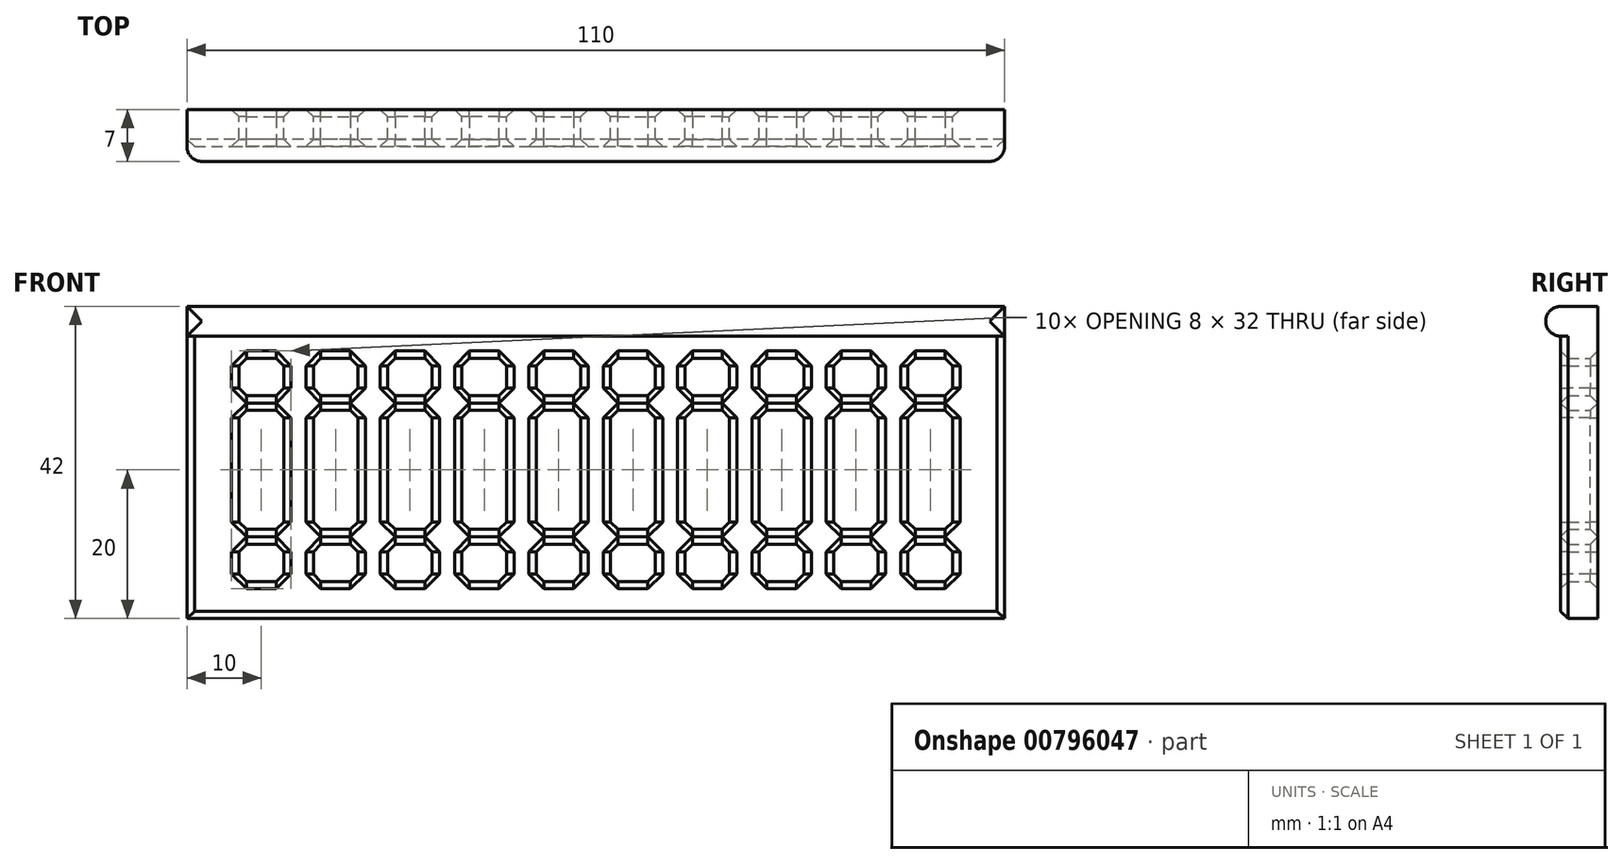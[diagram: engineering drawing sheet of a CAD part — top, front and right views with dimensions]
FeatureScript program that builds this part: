
annotation { "Feature Type Name" : "Feature", "Feature Type Description" : "" }
export const myFeature = defineFeature(function(context is Context, id is Id, definition is map)
    precondition{}
    {
        {
            var Q0;
            Q0=qCreatedBy(makeId("Front.planeOp"),FACE);
            var sketch = newSketch(context, id + "F0", { "sketchPlane" : qUnion([Q0])});
            skLineSegment(sketch, "E0.bottom", {"start": v(0, 0) * mm, "end": v(110, 0) * mm});
            skLineSegment(sketch, "E0.top", {"start": v(0, 40) * mm, "end": v(110, 40) * mm});
            skLineSegment(sketch, "E0.left", {"start": v(0, 0) * mm, "end": v(0, 40) * mm});
            skLineSegment(sketch, "E0.right", {"start": v(110, 0) * mm, "end": v(110, 40) * mm});
            skLineSegment(sketch, "E1.left", {"start": v(7, 35) * mm, "end": v(7, 5) * mm});
            skLineSegment(sketch, "E1.right", {"start": v(103, 35) * mm, "end": v(103, 5) * mm});
            skLineSegment(sketch, "E2.left", {"start": v(13, 35) * mm, "end": v(13, 5) * mm});
            skLineSegment(sketch, "E2.right", {"start": v(17, 35) * mm, "end": v(17, 5) * mm});
            skLineSegment(sketch, "E3.bottom", {"start": v(17, 5) * mm, "end": v(23, 5) * mm});
            skLineSegment(sketch, "E3.left", {"start": v(17, 5) * mm, "end": v(17, 35) * mm});
            skLineSegment(sketch, "E3.right", {"start": v(23, 5) * mm, "end": v(23, 35) * mm});
            skLineSegment(sketch, "E4.right", {"start": v(27, 5) * mm, "end": v(27, 35) * mm});
            skLineSegment(sketch, "E5.right", {"start": v(33, 35) * mm, "end": v(33, 5) * mm});
            skLineSegment(sketch, "E6.top", {"start": v(37, 5) * mm, "end": v(43, 5) * mm});
            skLineSegment(sketch, "E6.left", {"start": v(37, 35) * mm, "end": v(37, 5) * mm});
            skLineSegment(sketch, "E6.right", {"start": v(43, 35) * mm, "end": v(43, 5) * mm});
            skLineSegment(sketch, "E7.right", {"start": v(97, 35) * mm, "end": v(97, 5) * mm});
            skLineSegment(sketch, "E8.left", {"start": v(47, 35) * mm, "end": v(47, 5) * mm});
            skLineSegment(sketch, "E9.right", {"start": v(57, 35) * mm, "end": v(57, 5) * mm});
            skLineSegment(sketch, "E10.bottom", {"start": v(77, 35) * mm, "end": v(83, 35) * mm});
            skLineSegment(sketch, "E10.top", {"start": v(77, 5) * mm, "end": v(83, 5) * mm});
            skLineSegment(sketch, "E10.left", {"start": v(77, 35) * mm, "end": v(77, 5) * mm});
            skLineSegment(sketch, "E10.right", {"start": v(83, 35) * mm, "end": v(83, 5) * mm});
            skLineSegment(sketch, "E11.bottom", {"start": v(87, 35) * mm, "end": v(93, 35) * mm});
            skLineSegment(sketch, "E11.top", {"start": v(87, 5) * mm, "end": v(93, 5) * mm});
            skLineSegment(sketch, "E11.left", {"start": v(87, 35) * mm, "end": v(87, 5) * mm});
            skLineSegment(sketch, "E11.right", {"start": v(93, 35) * mm, "end": v(93, 5) * mm});
            skLineSegment(sketch, "E12.bottom", {"start": v(2, 37) * mm, "end": v(108, 37) * mm});
            skLineSegment(sketch, "E12.top", {"start": v(2, 3) * mm, "end": v(108, 3) * mm});
            skLineSegment(sketch, "E12.left", {"start": v(2, 37) * mm, "end": v(2, 3) * mm});
            skLineSegment(sketch, "E12.right", {"start": v(108, 37) * mm, "end": v(108, 3) * mm});
            skLineSegment(sketch, "E13.bottom", {"start": v(7, 30) * mm, "end": v(103, 30) * mm});
            skLineSegment(sketch, "E13.top", {"start": v(7, 10) * mm, "end": v(103, 10) * mm});
            skLineSegment(sketch, "E13.left", {"start": v(7, 30) * mm, "end": v(7, 10) * mm});
            skLineSegment(sketch, "E13.right", {"start": v(103, 30) * mm, "end": v(103, 10) * mm});
            skLineSegment(sketch, "E14.bottom", {"start": v(7, 28) * mm, "end": v(103, 28) * mm});
            skLineSegment(sketch, "E14.top", {"start": v(7, 12) * mm, "end": v(103, 12) * mm});
            skLineSegment(sketch, "E14.left", {"start": v(7, 28) * mm, "end": v(7, 12) * mm});
            skLineSegment(sketch, "E14.right", {"start": v(103, 28) * mm, "end": v(103, 12) * mm});
            skLineSegment(sketch, "E15", {"start": v(67, 35) * mm, "end": v(67, 5) * mm});
            skLineSegment(sketch, "E16", {"start": v(53, 35) * mm, "end": v(53, 5) * mm});
            skLineSegment(sketch, "E17", {"start": v(47, 35) * mm, "end": v(53, 35) * mm});
            skLineSegment(sketch, "E18", {"start": v(7, 35) * mm, "end": v(13, 35) * mm});
            skLineSegment(sketch, "E19", {"start": v(17, 35) * mm, "end": v(23, 35) * mm});
            skLineSegment(sketch, "E20", {"start": v(27, 35) * mm, "end": v(33, 35) * mm});
            skLineSegment(sketch, "E21", {"start": v(37, 35) * mm, "end": v(43, 35) * mm});
            skLineSegment(sketch, "E22", {"start": v(97, 35) * mm, "end": v(103, 35) * mm});
            skLineSegment(sketch, "E23", {"start": v(63, 35) * mm, "end": v(63, 5) * mm});
            skLineSegment(sketch, "E24", {"start": v(73, 35) * mm, "end": v(73, 5) * mm});
            skLineSegment(sketch, "E25", {"start": v(57, 35) * mm, "end": v(63, 35) * mm});
            skLineSegment(sketch, "E26", {"start": v(67, 35) * mm, "end": v(73, 35) * mm});
            skLineSegment(sketch, "E27", {"start": v(47, 5) * mm, "end": v(53, 5) * mm});
            skLineSegment(sketch, "E28", {"start": v(27, 5) * mm, "end": v(33, 5) * mm});
            skLineSegment(sketch, "E29", {"start": v(7, 5) * mm, "end": v(13, 5) * mm});
            skLineSegment(sketch, "E30", {"start": v(57, 5) * mm, "end": v(63, 5) * mm});
            skLineSegment(sketch, "E31", {"start": v(67, 5) * mm, "end": v(73, 5) * mm});
            skLineSegment(sketch, "E32", {"start": v(97, 5) * mm, "end": v(103, 5) * mm});
            skSolve(sketch);
        }
        {
            var Q0;
            {var subQ0=sQuery(id+"F0.wireOp",EDGE,"E2.top");Q0=makeQuery(id+"F0.imprint","IMPRINT",FACE,{"disambiguationData":[TD([[makeQuery(id+"F0.imprint","IMPRINT",EDGE,{"derivedFrom":subQ0}),1.0]])]});}
            var Q1;
            {var subQ0=sQuery(id+"F0.wireOp",EDGE,"E4.bottom");Q1=makeQuery(id+"F0.imprint","IMPRINT",FACE,{"disambiguationData":[TD([[makeQuery(id+"F0.imprint","IMPRINT",EDGE,{"derivedFrom":subQ0}),1.0]])]});}
            var Q2;
            {var subQ76=sQuery(id+"F0.wireOp",EDGE,"E3.bottom");Q2=makeQuery(id+"F0.imprint","IMPRINT",FACE,{"disambiguationData":[TD([[makeQuery(id+"F0.imprint","IMPRINT",EDGE,{"derivedFrom":subQ76}),-1.0]])]});}
            var Q3;
            {var subQ76=sQuery(id+"F0.wireOp",EDGE,"E3.bottom");Q3=makeQuery(id+"F0.imprint","IMPRINT",FACE,{"disambiguationData":[TD([[makeQuery(id+"F0.imprint","IMPRINT",EDGE,{"derivedFrom":subQ76}),-1.0]])]});}
            var Q4;
            {var subQ76=sQuery(id+"F0.wireOp",EDGE,"E3.bottom");Q4=makeQuery(id+"F0.imprint","IMPRINT",FACE,{"disambiguationData":[TD([[makeQuery(id+"F0.imprint","IMPRINT",EDGE,{"derivedFrom":subQ76}),-1.0]])]});}
            var Q5;
            {var subQ76=sQuery(id+"F0.wireOp",EDGE,"E3.bottom");Q5=makeQuery(id+"F0.imprint","IMPRINT",FACE,{"disambiguationData":[TD([[makeQuery(id+"F0.imprint","IMPRINT",EDGE,{"derivedFrom":subQ76}),-1.0]])]});}
            var Q6;
            {var subQ0=sQuery(id+"F0.wireOp",EDGE,"E15");var subQ1=sQuery(id+"F0.wireOp",EDGE,"E9.top");var subQ2=makeQuery(id+"F0.imprint","INTERSECT",VERTEX,{"derivedFrom":[subQ1,subQ0]});Q6=makeQuery(id+"F0.imprint","IMPRINT",FACE,{"disambiguationData":[TD([[makeQuery(id+"F0.imprint","IMPRINT",EDGE,{"disambiguationData":[TD([[subQ2,-1.0]])],"derivedFrom":subQ1}),-1.0]])]});}
            var Q7;
            Q7=makeQuery(id+"F0.imprint","IMPRINT",FACE,{"disambiguationData":[TD([[makeQuery(id+"F0.imprint","IMPRINT",EDGE,{"derivedFrom":sQuery(id+"F0.wireOp",EDGE,"E0.bottom")}),1.0]])]});
            var Q8;
            {var subQ0=sQuery(id+"F0.wireOp",EDGE,"E14.bottom");var subQ1=sQuery(id+"F0.wireOp",EDGE,"E2.left");var subQ2=makeQuery(id+"F0.imprint","INTERSECT",VERTEX,{"derivedFrom":[subQ1,subQ0]});Q8=makeQuery(id+"F0.imprint","IMPRINT",FACE,{"disambiguationData":[TD([[makeQuery(id+"F0.imprint","IMPRINT",EDGE,{"disambiguationData":[TD([[subQ2,1.0]])],"derivedFrom":subQ1}),1.0]])]});}
            var Q9;
            {var subQ0=sQuery(id+"F0.wireOp",EDGE,"E14.bottom");var subQ1=sQuery(id+"F0.wireOp",EDGE,"E1.left");var subQ2=makeQuery(id+"F0.imprint","INTERSECT",VERTEX,{"derivedFrom":[subQ1,subQ0]});Q9=makeQuery(id+"F0.imprint","IMPRINT",FACE,{"disambiguationData":[TD([[makeQuery(id+"F0.imprint","IMPRINT",EDGE,{"disambiguationData":[TD([[subQ2,1.0]])],"derivedFrom":subQ1}),1.0]])]});}
            var Q10;
            {var subQ0=sQuery(id+"F0.wireOp",EDGE,"E13.top");var subQ1=sQuery(id+"F0.wireOp",EDGE,"E2.left");var subQ2=makeQuery(id+"F0.imprint","INTERSECT",VERTEX,{"derivedFrom":[subQ1,subQ0]});Q10=makeQuery(id+"F0.imprint","IMPRINT",FACE,{"disambiguationData":[TD([[makeQuery(id+"F0.imprint","IMPRINT",EDGE,{"disambiguationData":[TD([[subQ2,1.0]])],"derivedFrom":subQ1}),1.0]])]});}
            var Q11;
            {var subQ0=sQuery(id+"F0.wireOp",EDGE,"E14.top");var subQ1=sQuery(id+"F0.wireOp",EDGE,"E1.left");var subQ2=makeQuery(id+"F0.imprint","INTERSECT",VERTEX,{"derivedFrom":[subQ1,subQ0]});Q11=makeQuery(id+"F0.imprint","IMPRINT",FACE,{"disambiguationData":[TD([[makeQuery(id+"F0.imprint","IMPRINT",EDGE,{"disambiguationData":[TD([[subQ2,-1.0]])],"derivedFrom":subQ1}),1.0]])]});}
            var Q12;
            {var subQ0=sQuery(id+"F0.wireOp",EDGE,"E14.top");var subQ1=sQuery(id+"F0.wireOp",EDGE,"E2.right");var subQ2=makeQuery(id+"F0.imprint","INTERSECT",VERTEX,{"derivedFrom":[subQ1,subQ0]});Q12=makeQuery(id+"F0.imprint","IMPRINT",FACE,{"disambiguationData":[TD([[makeQuery(id+"F0.imprint","IMPRINT",EDGE,{"disambiguationData":[TD([[subQ2,-1.0]])],"derivedFrom":subQ1}),1.0]])]});}
            var Q13;
            {var subQ0=sQuery(id+"F0.wireOp",EDGE,"E14.top");var subQ1=sQuery(id+"F0.wireOp",EDGE,"E3.right");var subQ2=makeQuery(id+"F0.imprint","INTERSECT",VERTEX,{"derivedFrom":[subQ1,subQ0]});Q13=makeQuery(id+"F0.imprint","IMPRINT",FACE,{"disambiguationData":[TD([[makeQuery(id+"F0.imprint","IMPRINT",EDGE,{"disambiguationData":[TD([[subQ2,1.0]])],"derivedFrom":subQ1}),-1.0]])]});}
            var Q14;
            {var subQ0=sQuery(id+"F0.wireOp",EDGE,"E14.top");var subQ1=sQuery(id+"F0.wireOp",EDGE,"E3.right");var subQ2=makeQuery(id+"F0.imprint","INTERSECT",VERTEX,{"derivedFrom":[subQ1,subQ0]});Q14=makeQuery(id+"F0.imprint","IMPRINT",FACE,{"disambiguationData":[TD([[makeQuery(id+"F0.imprint","IMPRINT",EDGE,{"disambiguationData":[TD([[subQ2,-1.0]])],"derivedFrom":subQ1}),-1.0]])]});}
            var Q15;
            {var subQ0=sQuery(id+"F0.wireOp",EDGE,"E13.bottom");var subQ1=sQuery(id+"F0.wireOp",EDGE,"E3.right");var subQ2=makeQuery(id+"F0.imprint","INTERSECT",VERTEX,{"derivedFrom":[subQ1,subQ0]});Q15=makeQuery(id+"F0.imprint","IMPRINT",FACE,{"disambiguationData":[TD([[makeQuery(id+"F0.imprint","IMPRINT",EDGE,{"disambiguationData":[TD([[subQ2,1.0]])],"derivedFrom":subQ1}),-1.0]])]});}
            var Q16;
            {var subQ0=sQuery(id+"F0.wireOp",EDGE,"E14.bottom");var subQ1=sQuery(id+"F0.wireOp",EDGE,"E2.right");var subQ2=makeQuery(id+"F0.imprint","INTERSECT",VERTEX,{"derivedFrom":[subQ1,subQ0]});Q16=makeQuery(id+"F0.imprint","IMPRINT",FACE,{"disambiguationData":[TD([[makeQuery(id+"F0.imprint","IMPRINT",EDGE,{"disambiguationData":[TD([[subQ2,1.0]])],"derivedFrom":subQ1}),1.0]])]});}
            var Q17;
            {var subQ0=sQuery(id+"F0.wireOp",EDGE,"E14.bottom");var subQ1=sQuery(id+"F0.wireOp",EDGE,"E2.left");var subQ2=makeQuery(id+"F0.imprint","INTERSECT",VERTEX,{"derivedFrom":[subQ1,subQ0]});Q17=makeQuery(id+"F0.imprint","IMPRINT",FACE,{"disambiguationData":[TD([[makeQuery(id+"F0.imprint","IMPRINT",EDGE,{"disambiguationData":[TD([[subQ2,-1.0]])],"derivedFrom":subQ1}),1.0]])]});}
            var Q18;
            {var subQ0=sQuery(id+"F0.wireOp",EDGE,"E14.top");var subQ1=sQuery(id+"F0.wireOp",EDGE,"E4.right");var subQ2=makeQuery(id+"F0.imprint","INTERSECT",VERTEX,{"derivedFrom":[subQ1,subQ0]});Q18=makeQuery(id+"F0.imprint","IMPRINT",FACE,{"disambiguationData":[TD([[makeQuery(id+"F0.imprint","IMPRINT",EDGE,{"disambiguationData":[TD([[subQ2,1.0]])],"derivedFrom":subQ1}),-1.0]])]});}
            var Q19;
            {var subQ0=sQuery(id+"F0.wireOp",EDGE,"E13.top");var subQ1=sQuery(id+"F0.wireOp",EDGE,"E5.right");var subQ2=makeQuery(id+"F0.imprint","INTERSECT",VERTEX,{"derivedFrom":[subQ1,subQ0]});Q19=makeQuery(id+"F0.imprint","IMPRINT",FACE,{"disambiguationData":[TD([[makeQuery(id+"F0.imprint","IMPRINT",EDGE,{"disambiguationData":[TD([[subQ2,1.0]])],"derivedFrom":subQ1}),1.0]])]});}
            var Q20;
            {var subQ0=sQuery(id+"F0.wireOp",EDGE,"E14.bottom");var subQ1=sQuery(id+"F0.wireOp",EDGE,"E5.right");var subQ2=makeQuery(id+"F0.imprint","INTERSECT",VERTEX,{"derivedFrom":[subQ1,subQ0]});Q20=makeQuery(id+"F0.imprint","IMPRINT",FACE,{"disambiguationData":[TD([[makeQuery(id+"F0.imprint","IMPRINT",EDGE,{"disambiguationData":[TD([[subQ2,-1.0]])],"derivedFrom":subQ1}),1.0]])]});}
            var Q21;
            {var subQ0=sQuery(id+"F0.wireOp",EDGE,"E14.bottom");var subQ1=sQuery(id+"F0.wireOp",EDGE,"E5.right");var subQ2=makeQuery(id+"F0.imprint","INTERSECT",VERTEX,{"derivedFrom":[subQ1,subQ0]});Q21=makeQuery(id+"F0.imprint","IMPRINT",FACE,{"disambiguationData":[TD([[makeQuery(id+"F0.imprint","IMPRINT",EDGE,{"disambiguationData":[TD([[subQ2,1.0]])],"derivedFrom":subQ1}),1.0]])]});}
            var Q22;
            {var subQ0=sQuery(id+"F0.wireOp",EDGE,"E13.bottom");var subQ1=sQuery(id+"F0.wireOp",EDGE,"E4.right");var subQ2=makeQuery(id+"F0.imprint","INTERSECT",VERTEX,{"derivedFrom":[subQ1,subQ0]});Q22=makeQuery(id+"F0.imprint","IMPRINT",FACE,{"disambiguationData":[TD([[makeQuery(id+"F0.imprint","IMPRINT",EDGE,{"disambiguationData":[TD([[subQ2,1.0]])],"derivedFrom":subQ1}),-1.0]])]});}
            var Q23;
            {var subQ0=sQuery(id+"F0.wireOp",EDGE,"E14.bottom");var subQ1=sQuery(id+"F0.wireOp",EDGE,"E6.left");var subQ2=makeQuery(id+"F0.imprint","INTERSECT",VERTEX,{"derivedFrom":[subQ1,subQ0]});Q23=makeQuery(id+"F0.imprint","IMPRINT",FACE,{"disambiguationData":[TD([[makeQuery(id+"F0.imprint","IMPRINT",EDGE,{"disambiguationData":[TD([[subQ2,1.0]])],"derivedFrom":subQ1}),1.0]])]});}
            var Q24;
            {var subQ0=sQuery(id+"F0.wireOp",EDGE,"E14.bottom");var subQ1=sQuery(id+"F0.wireOp",EDGE,"E6.right");var subQ2=makeQuery(id+"F0.imprint","INTERSECT",VERTEX,{"derivedFrom":[subQ1,subQ0]});Q24=makeQuery(id+"F0.imprint","IMPRINT",FACE,{"disambiguationData":[TD([[makeQuery(id+"F0.imprint","IMPRINT",EDGE,{"disambiguationData":[TD([[subQ2,1.0]])],"derivedFrom":subQ1}),1.0]])]});}
            var Q25;
            {var subQ0=sQuery(id+"F0.wireOp",EDGE,"E14.bottom");var subQ1=sQuery(id+"F0.wireOp",EDGE,"E6.right");var subQ2=makeQuery(id+"F0.imprint","INTERSECT",VERTEX,{"derivedFrom":[subQ1,subQ0]});Q25=makeQuery(id+"F0.imprint","IMPRINT",FACE,{"disambiguationData":[TD([[makeQuery(id+"F0.imprint","IMPRINT",EDGE,{"disambiguationData":[TD([[subQ2,-1.0]])],"derivedFrom":subQ1}),1.0]])]});}
            var Q26;
            {var subQ0=sQuery(id+"F0.wireOp",EDGE,"E14.top");var subQ1=sQuery(id+"F0.wireOp",EDGE,"E6.right");var subQ2=makeQuery(id+"F0.imprint","INTERSECT",VERTEX,{"derivedFrom":[subQ1,subQ0]});Q26=makeQuery(id+"F0.imprint","IMPRINT",FACE,{"disambiguationData":[TD([[makeQuery(id+"F0.imprint","IMPRINT",EDGE,{"disambiguationData":[TD([[subQ2,-1.0]])],"derivedFrom":subQ1}),1.0]])]});}
            var Q27;
            {var subQ0=sQuery(id+"F0.wireOp",EDGE,"E14.top");var subQ1=sQuery(id+"F0.wireOp",EDGE,"E6.left");var subQ2=makeQuery(id+"F0.imprint","INTERSECT",VERTEX,{"derivedFrom":[subQ1,subQ0]});Q27=makeQuery(id+"F0.imprint","IMPRINT",FACE,{"disambiguationData":[TD([[makeQuery(id+"F0.imprint","IMPRINT",EDGE,{"disambiguationData":[TD([[subQ2,-1.0]])],"derivedFrom":subQ1}),1.0]])]});}
            var Q28;
            {var subQ76=sQuery(id+"F0.wireOp",EDGE,"E3.bottom");Q28=makeQuery(id+"F0.imprint","IMPRINT",FACE,{"disambiguationData":[TD([[makeQuery(id+"F0.imprint","IMPRINT",EDGE,{"derivedFrom":subQ76}),-1.0]])]});}
            var Q29;
            {var subQ0=sQuery(id+"F0.wireOp",EDGE,"E13.top");var subQ1=sQuery(id+"F0.wireOp",EDGE,"E8.left");var subQ2=makeQuery(id+"F0.imprint","INTERSECT",VERTEX,{"derivedFrom":[subQ1,subQ0]});Q29=makeQuery(id+"F0.imprint","IMPRINT",FACE,{"disambiguationData":[TD([[makeQuery(id+"F0.imprint","IMPRINT",EDGE,{"disambiguationData":[TD([[subQ2,1.0]])],"derivedFrom":subQ1}),1.0]])]});}
            var Q30;
            {var subQ0=sQuery(id+"F0.wireOp",EDGE,"E14.bottom");var subQ1=sQuery(id+"F0.wireOp",EDGE,"E8.left");var subQ2=makeQuery(id+"F0.imprint","INTERSECT",VERTEX,{"derivedFrom":[subQ1,subQ0]});Q30=makeQuery(id+"F0.imprint","IMPRINT",FACE,{"disambiguationData":[TD([[makeQuery(id+"F0.imprint","IMPRINT",EDGE,{"disambiguationData":[TD([[subQ2,1.0]])],"derivedFrom":subQ1}),1.0]])]});}
            var Q31;
            {var subQ0=sQuery(id+"F0.wireOp",EDGE,"E14.bottom");var subQ1=sQuery(id+"F0.wireOp",EDGE,"E10.left");var subQ2=makeQuery(id+"F0.imprint","INTERSECT",VERTEX,{"derivedFrom":[subQ1,subQ0]});Q31=makeQuery(id+"F0.imprint","IMPRINT",FACE,{"disambiguationData":[TD([[makeQuery(id+"F0.imprint","IMPRINT",EDGE,{"disambiguationData":[TD([[subQ2,1.0]])],"derivedFrom":subQ1}),1.0]])]});}
            var Q32;
            {var subQ0=sQuery(id+"F0.wireOp",EDGE,"E14.bottom");var subQ1=sQuery(id+"F0.wireOp",EDGE,"E10.right");var subQ2=makeQuery(id+"F0.imprint","INTERSECT",VERTEX,{"derivedFrom":[subQ1,subQ0]});Q32=makeQuery(id+"F0.imprint","IMPRINT",FACE,{"disambiguationData":[TD([[makeQuery(id+"F0.imprint","IMPRINT",EDGE,{"disambiguationData":[TD([[subQ2,1.0]])],"derivedFrom":subQ1}),1.0]])]});}
            var Q33;
            {var subQ0=sQuery(id+"F0.wireOp",EDGE,"E14.bottom");var subQ1=sQuery(id+"F0.wireOp",EDGE,"E10.right");var subQ2=makeQuery(id+"F0.imprint","INTERSECT",VERTEX,{"derivedFrom":[subQ1,subQ0]});Q33=makeQuery(id+"F0.imprint","IMPRINT",FACE,{"disambiguationData":[TD([[makeQuery(id+"F0.imprint","IMPRINT",EDGE,{"disambiguationData":[TD([[subQ2,-1.0]])],"derivedFrom":subQ1}),1.0]])]});}
            var Q34;
            {var subQ0=sQuery(id+"F0.wireOp",EDGE,"E14.top");var subQ1=sQuery(id+"F0.wireOp",EDGE,"E10.right");var subQ2=makeQuery(id+"F0.imprint","INTERSECT",VERTEX,{"derivedFrom":[subQ1,subQ0]});Q34=makeQuery(id+"F0.imprint","IMPRINT",FACE,{"disambiguationData":[TD([[makeQuery(id+"F0.imprint","IMPRINT",EDGE,{"disambiguationData":[TD([[subQ2,-1.0]])],"derivedFrom":subQ1}),1.0]])]});}
            var Q35;
            {var subQ0=sQuery(id+"F0.wireOp",EDGE,"E14.top");var subQ1=sQuery(id+"F0.wireOp",EDGE,"E10.left");var subQ2=makeQuery(id+"F0.imprint","INTERSECT",VERTEX,{"derivedFrom":[subQ1,subQ0]});Q35=makeQuery(id+"F0.imprint","IMPRINT",FACE,{"disambiguationData":[TD([[makeQuery(id+"F0.imprint","IMPRINT",EDGE,{"disambiguationData":[TD([[subQ2,-1.0]])],"derivedFrom":subQ1}),1.0]])]});}
            var Q36;
            {var subQ0=sQuery(id+"F0.wireOp",EDGE,"E13.top");var subQ1=sQuery(id+"F0.wireOp",EDGE,"E11.left");var subQ2=makeQuery(id+"F0.imprint","INTERSECT",VERTEX,{"derivedFrom":[subQ1,subQ0]});Q36=makeQuery(id+"F0.imprint","IMPRINT",FACE,{"disambiguationData":[TD([[makeQuery(id+"F0.imprint","IMPRINT",EDGE,{"disambiguationData":[TD([[subQ2,1.0]])],"derivedFrom":subQ1}),1.0]])]});}
            var Q37;
            {var subQ0=sQuery(id+"F0.wireOp",EDGE,"E14.bottom");var subQ1=sQuery(id+"F0.wireOp",EDGE,"E11.left");var subQ2=makeQuery(id+"F0.imprint","INTERSECT",VERTEX,{"derivedFrom":[subQ1,subQ0]});Q37=makeQuery(id+"F0.imprint","IMPRINT",FACE,{"disambiguationData":[TD([[makeQuery(id+"F0.imprint","IMPRINT",EDGE,{"disambiguationData":[TD([[subQ2,1.0]])],"derivedFrom":subQ1}),1.0]])]});}
            var Q38;
            {var subQ0=sQuery(id+"F0.wireOp",EDGE,"E14.bottom");var subQ1=sQuery(id+"F0.wireOp",EDGE,"E7.right");var subQ2=makeQuery(id+"F0.imprint","INTERSECT",VERTEX,{"derivedFrom":[subQ1,subQ0]});Q38=makeQuery(id+"F0.imprint","IMPRINT",FACE,{"disambiguationData":[TD([[makeQuery(id+"F0.imprint","IMPRINT",EDGE,{"disambiguationData":[TD([[subQ2,1.0]])],"derivedFrom":subQ1}),-1.0]])]});}
            var Q39;
            {var subQ0=sQuery(id+"F0.wireOp",EDGE,"E14.bottom");var subQ1=sQuery(id+"F0.wireOp",EDGE,"E7.right");var subQ2=makeQuery(id+"F0.imprint","INTERSECT",VERTEX,{"derivedFrom":[subQ1,subQ0]});Q39=makeQuery(id+"F0.imprint","IMPRINT",FACE,{"disambiguationData":[TD([[makeQuery(id+"F0.imprint","IMPRINT",EDGE,{"disambiguationData":[TD([[subQ2,-1.0]])],"derivedFrom":subQ1}),-1.0]])]});}
            var Q40;
            {var subQ0=sQuery(id+"F0.wireOp",EDGE,"E13.top");var subQ1=sQuery(id+"F0.wireOp",EDGE,"E7.right");var subQ2=makeQuery(id+"F0.imprint","INTERSECT",VERTEX,{"derivedFrom":[subQ1,subQ0]});Q40=makeQuery(id+"F0.imprint","IMPRINT",FACE,{"disambiguationData":[TD([[makeQuery(id+"F0.imprint","IMPRINT",EDGE,{"disambiguationData":[TD([[subQ2,1.0]])],"derivedFrom":subQ1}),-1.0]])]});}
            var Q41;
            {var subQ0=sQuery(id+"F0.wireOp",EDGE,"E14.bottom");var subQ1=sQuery(id+"F0.wireOp",EDGE,"E1.right");var subQ2=makeQuery(id+"F0.imprint","INTERSECT",VERTEX,{"derivedFrom":[subQ1,subQ0]});Q41=makeQuery(id+"F0.imprint","IMPRINT",FACE,{"disambiguationData":[TD([[makeQuery(id+"F0.imprint","IMPRINT",EDGE,{"disambiguationData":[TD([[subQ2,1.0]])],"derivedFrom":subQ1}),-1.0]])]});}
            var Q42;
            {var subQ0=sQuery(id+"F0.wireOp",EDGE,"E13.top");var subQ1=sQuery(id+"F0.wireOp",EDGE,"E1.right");var subQ2=makeQuery(id+"F0.imprint","INTERSECT",VERTEX,{"derivedFrom":[subQ1,subQ0]});Q42=makeQuery(id+"F0.imprint","IMPRINT",FACE,{"disambiguationData":[TD([[makeQuery(id+"F0.imprint","IMPRINT",EDGE,{"disambiguationData":[TD([[subQ2,1.0]])],"derivedFrom":subQ1}),-1.0]])]});}
            var Q43;
            {var subQ0=sQuery(id+"F0.wireOp",EDGE,"E14.bottom");var subQ1=sQuery(id+"F0.wireOp",EDGE,"E9.right");var subQ2=makeQuery(id+"F0.imprint","INTERSECT",VERTEX,{"derivedFrom":[subQ1,subQ0]});Q43=makeQuery(id+"F0.imprint","IMPRINT",FACE,{"disambiguationData":[TD([[makeQuery(id+"F0.imprint","IMPRINT",EDGE,{"disambiguationData":[TD([[subQ2,-1.0]])],"derivedFrom":subQ1}),-1.0]])]});}
            var Q44;
            {var subQ0=sQuery(id+"F0.wireOp",EDGE,"E14.bottom");var subQ1=sQuery(id+"F0.wireOp",EDGE,"E9.right");var subQ2=makeQuery(id+"F0.imprint","INTERSECT",VERTEX,{"derivedFrom":[subQ1,subQ0]});Q44=makeQuery(id+"F0.imprint","IMPRINT",FACE,{"disambiguationData":[TD([[makeQuery(id+"F0.imprint","IMPRINT",EDGE,{"disambiguationData":[TD([[subQ2,1.0]])],"derivedFrom":subQ1}),-1.0]])]});}
            var Q45;
            {var subQ0=sQuery(id+"F0.wireOp",EDGE,"E14.bottom");var subQ1=sQuery(id+"F0.wireOp",EDGE,"E9.right");var subQ2=makeQuery(id+"F0.imprint","INTERSECT",VERTEX,{"derivedFrom":[subQ1,subQ0]});Q45=makeQuery(id+"F0.imprint","IMPRINT",FACE,{"disambiguationData":[TD([[makeQuery(id+"F0.imprint","IMPRINT",EDGE,{"disambiguationData":[TD([[subQ2,1.0]])],"derivedFrom":subQ1}),1.0]])]});}
            var Q46;
            {var subQ0=sQuery(id+"F0.wireOp",EDGE,"E14.top");var subQ1=sQuery(id+"F0.wireOp",EDGE,"E9.right");var subQ2=makeQuery(id+"F0.imprint","INTERSECT",VERTEX,{"derivedFrom":[subQ1,subQ0]});Q46=makeQuery(id+"F0.imprint","IMPRINT",FACE,{"disambiguationData":[TD([[makeQuery(id+"F0.imprint","IMPRINT",EDGE,{"disambiguationData":[TD([[subQ2,-1.0]])],"derivedFrom":subQ1}),-1.0]])]});}
            var Q47;
            {var subQ0=sQuery(id+"F0.wireOp",EDGE,"E14.top");var subQ1=sQuery(id+"F0.wireOp",EDGE,"E9.right");var subQ2=makeQuery(id+"F0.imprint","INTERSECT",VERTEX,{"derivedFrom":[subQ1,subQ0]});Q47=makeQuery(id+"F0.imprint","IMPRINT",FACE,{"disambiguationData":[TD([[makeQuery(id+"F0.imprint","IMPRINT",EDGE,{"disambiguationData":[TD([[subQ2,-1.0]])],"derivedFrom":subQ1}),1.0]])]});}
            var Q48;
            {var subQ1=sQuery(id+"F0.wireOp",EDGE,"E7.top");var subQ7=sQuery(id+"F0.wireOp",EDGE,"E8.top");var subQ8=makeQuery(id+"F0.imprint","INTERSECT",VERTEX,{"derivedFrom":[subQ1,subQ7]});Q48=makeQuery(id+"F0.imprint","IMPRINT",FACE,{"disambiguationData":[TD([[makeQuery(id+"F0.imprint","IMPRINT",EDGE,{"disambiguationData":[TD([[subQ8,1.0]])],"derivedFrom":subQ7}),1.0]])]});}
            var Q49;
            {var subQ0=sQuery(id+"F0.wireOp",EDGE,"E15");var subQ1=sQuery(id+"F0.wireOp",EDGE,"E13.top");var subQ2=makeQuery(id+"F0.imprint","INTERSECT",VERTEX,{"derivedFrom":[subQ1,subQ0]});Q49=makeQuery(id+"F0.imprint","IMPRINT",FACE,{"disambiguationData":[TD([[makeQuery(id+"F0.imprint","IMPRINT",EDGE,{"disambiguationData":[TD([[subQ2,1.0]])],"derivedFrom":subQ1}),1.0]])]});}
            var Q50;
            {var subQ0=sQuery(id+"F0.wireOp",EDGE,"E15");var subQ1=sQuery(id+"F0.wireOp",EDGE,"E13.top");var subQ2=makeQuery(id+"F0.imprint","INTERSECT",VERTEX,{"derivedFrom":[subQ1,subQ0]});Q50=makeQuery(id+"F0.imprint","IMPRINT",FACE,{"disambiguationData":[TD([[makeQuery(id+"F0.imprint","IMPRINT",EDGE,{"disambiguationData":[TD([[subQ2,-1.0]])],"derivedFrom":subQ1}),1.0]])]});}
            var Q51;
            {var subQ0=sQuery(id+"F0.wireOp",EDGE,"E14.top");var subQ1=sQuery(id+"F0.wireOp",EDGE,"E10.left");var subQ2=makeQuery(id+"F0.imprint","INTERSECT",VERTEX,{"derivedFrom":[subQ1,subQ0]});Q51=makeQuery(id+"F0.imprint","IMPRINT",FACE,{"disambiguationData":[TD([[makeQuery(id+"F0.imprint","IMPRINT",EDGE,{"disambiguationData":[TD([[subQ2,-1.0]])],"derivedFrom":subQ1}),-1.0]])]});}
            var Q52;
            {var subQ0=sQuery(id+"F0.wireOp",EDGE,"E15");var subQ1=sQuery(id+"F0.wireOp",EDGE,"E14.bottom");var subQ2=makeQuery(id+"F0.imprint","INTERSECT",VERTEX,{"derivedFrom":[subQ1,subQ0]});Q52=makeQuery(id+"F0.imprint","IMPRINT",FACE,{"disambiguationData":[TD([[makeQuery(id+"F0.imprint","IMPRINT",EDGE,{"disambiguationData":[TD([[subQ2,1.0]])],"derivedFrom":subQ1}),-1.0]])]});}
            var Q53;
            {var subQ0=sQuery(id+"F0.wireOp",EDGE,"E14.bottom");var subQ1=sQuery(id+"F0.wireOp",EDGE,"E10.left");var subQ2=makeQuery(id+"F0.imprint","INTERSECT",VERTEX,{"derivedFrom":[subQ1,subQ0]});Q53=makeQuery(id+"F0.imprint","IMPRINT",FACE,{"disambiguationData":[TD([[makeQuery(id+"F0.imprint","IMPRINT",EDGE,{"disambiguationData":[TD([[subQ2,-1.0]])],"derivedFrom":subQ1}),-1.0]])]});}
            var Q54;
            {var subQ0=sQuery(id+"F0.wireOp",EDGE,"E15");var subQ1=sQuery(id+"F0.wireOp",EDGE,"E13.bottom");var subQ2=makeQuery(id+"F0.imprint","INTERSECT",VERTEX,{"derivedFrom":[subQ1,subQ0]});Q54=makeQuery(id+"F0.imprint","IMPRINT",FACE,{"disambiguationData":[TD([[makeQuery(id+"F0.imprint","IMPRINT",EDGE,{"disambiguationData":[TD([[subQ2,1.0]])],"derivedFrom":subQ1}),-1.0]])]});}
            var Q55;
            {var subQ76=sQuery(id+"F0.wireOp",EDGE,"E3.bottom");Q55=makeQuery(id+"F0.imprint","IMPRINT",FACE,{"disambiguationData":[TD([[makeQuery(id+"F0.imprint","IMPRINT",EDGE,{"derivedFrom":subQ76}),-1.0]])]});}
            var Q56;
            {var subQ0=sQuery(id+"F0.wireOp",EDGE,"E14.bottom");var subQ1=sQuery(id+"F0.wireOp",EDGE,"E2.right");var subQ2=makeQuery(id+"F0.imprint","INTERSECT",VERTEX,{"derivedFrom":[subQ1,subQ0]});var subQ3=sQuery(id+"F0.wireOp",EDGE,"E13.bottom");var subQ5=makeQuery(id+"F0.imprint","IMPRINT",EDGE,{"disambiguationData":[TD([[subQ2,1.0]])],"derivedFrom":subQ1});var subQ6=sQuery(id+"F0.wireOp",EDGE,"E3.right");var subQ8=makeQuery(id+"F0.imprint","INTERSECT",VERTEX,{"derivedFrom":[subQ6,subQ3]});var subQ9=makeQuery(id+"F0.imprint","IMPRINT",EDGE,{"disambiguationData":[TD([[subQ8,1.0]])],"derivedFrom":subQ6});var subQ10=sQuery(id+"F0.wireOp",EDGE,"E10.left");var subQ11=makeQuery(id+"F0.imprint","INTERSECT",VERTEX,{"derivedFrom":[subQ10,subQ0]});var subQ13=makeQuery(id+"F0.imprint","IMPRINT",EDGE,{"disambiguationData":[TD([[subQ11,1.0]])],"derivedFrom":subQ10});var subQ14=sQuery(id+"F0.wireOp",EDGE,"E10.right");var subQ15=makeQuery(id+"F0.imprint","INTERSECT",VERTEX,{"derivedFrom":[subQ14,subQ0]});var subQ17=makeQuery(id+"F0.imprint","IMPRINT",EDGE,{"disambiguationData":[TD([[subQ15,1.0]])],"derivedFrom":subQ14});var subQ18=sQuery(id+"F0.wireOp",EDGE,"E4.right");var subQ19=makeQuery(id+"F0.imprint","INTERSECT",VERTEX,{"derivedFrom":[subQ18,subQ3]});var subQ21=makeQuery(id+"F0.imprint","IMPRINT",EDGE,{"disambiguationData":[TD([[subQ19,1.0]])],"derivedFrom":subQ18});var subQ22=sQuery(id+"F0.wireOp",EDGE,"E5.right");var subQ23=makeQuery(id+"F0.imprint","INTERSECT",VERTEX,{"derivedFrom":[subQ22,subQ0]});var subQ25=makeQuery(id+"F0.imprint","IMPRINT",EDGE,{"disambiguationData":[TD([[subQ23,1.0]])],"derivedFrom":subQ22});var subQ26=sQuery(id+"F0.wireOp",EDGE,"E15");var subQ27=makeQuery(id+"F0.imprint","INTERSECT",VERTEX,{"derivedFrom":[subQ3,subQ26]});var subQ34=sQuery(id+"F0.wireOp",EDGE,"E7.right");var subQ35=makeQuery(id+"F0.imprint","INTERSECT",VERTEX,{"derivedFrom":[subQ34,subQ0]});var subQ41=sQuery(id+"F0.wireOp",EDGE,"E1.left");var subQ42=makeQuery(id+"F0.imprint","INTERSECT",VERTEX,{"derivedFrom":[subQ41,subQ0]});var subQ44=sQuery(id+"F0.wireOp",EDGE,"E2.left");var subQ45=makeQuery(id+"F0.imprint","INTERSECT",VERTEX,{"derivedFrom":[subQ44,subQ0]});var subQ47=makeQuery(id+"F0.imprint","IMPRINT",EDGE,{"disambiguationData":[TD([[subQ45,1.0]])],"derivedFrom":subQ44});var subQ52=sQuery(id+"F0.wireOp",EDGE,"E6.right");var subQ53=makeQuery(id+"F0.imprint","INTERSECT",VERTEX,{"derivedFrom":[subQ52,subQ0]});var subQ55=makeQuery(id+"F0.imprint","IMPRINT",EDGE,{"disambiguationData":[TD([[subQ53,1.0]])],"derivedFrom":subQ52});var subQ56=sQuery(id+"F0.wireOp",EDGE,"E8.left");var subQ57=makeQuery(id+"F0.imprint","INTERSECT",VERTEX,{"derivedFrom":[subQ56,subQ0]});var subQ59=makeQuery(id+"F0.imprint","IMPRINT",EDGE,{"disambiguationData":[TD([[subQ57,1.0]])],"derivedFrom":subQ56});var subQ60=sQuery(id+"F0.wireOp",EDGE,"E6.left");var subQ61=makeQuery(id+"F0.imprint","INTERSECT",VERTEX,{"derivedFrom":[subQ60,subQ0]});var subQ63=makeQuery(id+"F0.imprint","IMPRINT",EDGE,{"disambiguationData":[TD([[subQ61,1.0]])],"derivedFrom":subQ60});var subQ64=sQuery(id+"F0.wireOp",EDGE,"E11.left");var subQ65=makeQuery(id+"F0.imprint","INTERSECT",VERTEX,{"derivedFrom":[subQ64,subQ0]});var subQ67=makeQuery(id+"F0.imprint","IMPRINT",EDGE,{"disambiguationData":[TD([[subQ65,1.0]])],"derivedFrom":subQ64});var subQ68=sQuery(id+"F0.wireOp",EDGE,"E9.right");var subQ69=makeQuery(id+"F0.imprint","INTERSECT",VERTEX,{"derivedFrom":[subQ68,subQ0]});var subQ71=makeQuery(id+"F0.imprint","IMPRINT",EDGE,{"disambiguationData":[TD([[subQ69,1.0]])],"derivedFrom":subQ68});Q56=qUnion([makeQuery(id+"F0.imprint","IMPRINT",FACE,{"disambiguationData":[TD([[subQ67,1.0]])]}),makeQuery(id+"F0.imprint","IMPRINT",FACE,{"disambiguationData":[TD([[subQ63,1.0]])]}),makeQuery(id+"F0.imprint","IMPRINT",FACE,{"disambiguationData":[TD([[subQ47,1.0]])]}),makeQuery(id+"F0.imprint","IMPRINT",FACE,{"disambiguationData":[TD([[subQ71,-1.0]])]}),makeQuery(id+"F0.imprint","IMPRINT",FACE,{"disambiguationData":[TD([[subQ59,1.0]])]}),makeQuery(id+"F0.imprint","IMPRINT",FACE,{"disambiguationData":[TD([[subQ71,1.0]])]}),makeQuery(id+"F0.imprint","IMPRINT",FACE,{"disambiguationData":[TD([[subQ17,1.0]])]}),makeQuery(id+"F0.imprint","IMPRINT",FACE,{"disambiguationData":[TD([[subQ9,-1.0]])]}),makeQuery(id+"F0.imprint","IMPRINT",FACE,{"disambiguationData":[TD([[subQ25,1.0]])]}),makeQuery(id+"F0.imprint","IMPRINT",FACE,{"disambiguationData":[TD([[subQ55,1.0]])]}),makeQuery(id+"F0.imprint","IMPRINT",FACE,{"disambiguationData":[TD([[makeQuery(id+"F0.imprint","IMPRINT",EDGE,{"disambiguationData":[TD([[subQ27,1.0]])],"derivedFrom":subQ3}),-1.0]])]}),makeQuery(id+"F0.imprint","IMPRINT",FACE,{"disambiguationData":[TD([[subQ13,-1.0]])]}),makeQuery(id+"F0.imprint","IMPRINT",FACE,{"disambiguationData":[TD([[makeQuery(id+"F0.imprint","IMPRINT",EDGE,{"disambiguationData":[TD([[subQ42,1.0]])],"derivedFrom":subQ41}),1.0]])]}),makeQuery(id+"F0.imprint","IMPRINT",FACE,{"disambiguationData":[TD([[makeQuery(id+"F0.imprint","IMPRINT",EDGE,{"disambiguationData":[TD([[subQ35,1.0]])],"derivedFrom":subQ34}),-1.0]])]}),makeQuery(id+"F0.imprint","IMPRINT",FACE,{"disambiguationData":[TD([[makeQuery(id+"F0.imprint","IMPRINT",EDGE,{"disambiguationData":[TD([[subQ27,-1.0]])],"derivedFrom":subQ3}),-1.0]])]}),makeQuery(id+"F0.imprint","IMPRINT",FACE,{"disambiguationData":[TD([[subQ21,-1.0]])]}),makeQuery(id+"F0.imprint","IMPRINT",FACE,{"disambiguationData":[TD([[subQ13,1.0]])]}),makeQuery(id+"F0.imprint","IMPRINT",FACE,{"disambiguationData":[TD([[subQ5,1.0]])]})]);}
            var Q57;
            {var subQ0=sQuery(id+"F0.wireOp",EDGE,"E14.bottom");var subQ1=sQuery(id+"F0.wireOp",EDGE,"E10.left");var subQ2=makeQuery(id+"F0.imprint","INTERSECT",VERTEX,{"derivedFrom":[subQ1,subQ0]});Q57=makeQuery(id+"F0.imprint","IMPRINT",FACE,{"disambiguationData":[TD([[makeQuery(id+"F0.imprint","IMPRINT",EDGE,{"disambiguationData":[TD([[subQ2,1.0]])],"derivedFrom":subQ1}),-1.0]])]});}
            extrude(context, id + "F1", {"entities" : qUnion([Q0, Q1, Q2, Q3, Q4, Q5, Q6, Q7, Q8, Q9, Q10, Q11, Q12, Q13, Q14, Q15, Q16, Q17, Q18, Q19, Q20, Q21, Q22, Q23, Q24, Q25, Q26, Q27, Q28, Q29, Q30, Q31, Q32, Q33, Q34, Q35, Q36, Q37, Q38, Q39, Q40, Q41, Q42, Q43, Q44, Q45, Q46, Q47, Q48, Q49, Q50, Q51, Q52, Q53, Q54, Q55, Q56, Q57]), "depth" : 5 * mm, "offsetDistance" : 25 * mm});
        }
        {
            var Q0;
            {var subQ0=sQuery(id+"F0.wireOp",EDGE,"E8.left");Q0=makeQuery(id+"F1.opExtrude","CAP_EDGE",EDGE,{"disambiguationData":[OSD([subQ0]),TDD([makeQuery(id+"F0.imprint","IMPRINT",EDGE,{"disambiguationData":[TD([[makeQuery(id+"F0.imprint","INTERSECT",VERTEX,{"derivedFrom":[subQ0,sQuery(id+"F0.wireOp",EDGE,"E17")]}),-1.0]])],"derivedFrom":subQ0})])],"isStart":true});}
            var Q1;
            {var subQ0=sQuery(id+"F0.wireOp",EDGE,"E14.bottom");Q1=makeQuery(id+"F1.opExtrude","CAP_EDGE",EDGE,{"disambiguationData":[OSD([subQ0]),TDD([makeQuery(id+"F0.imprint","IMPRINT",EDGE,{"disambiguationData":[TD([[makeQuery(id+"F0.imprint","INTERSECT",VERTEX,{"derivedFrom":[sQuery(id+"F0.wireOp",EDGE,"E9.right"),subQ0]}),-1.0]])],"derivedFrom":subQ0})])],"isStart":true});}
            var Q2;
            {var subQ0=sQuery(id+"F0.wireOp",EDGE,"E14.bottom");Q2=makeQuery(id+"F1.opExtrude","CAP_EDGE",EDGE,{"disambiguationData":[OSD([subQ0]),TDD([makeQuery(id+"F0.imprint","IMPRINT",EDGE,{"disambiguationData":[TD([[makeQuery(id+"F0.imprint","INTERSECT",VERTEX,{"derivedFrom":[sQuery(id+"F0.wireOp",EDGE,"E8.left"),subQ0]}),-1.0]])],"derivedFrom":subQ0})])],"isStart":true});}
            var Q3;
            {var subQ0=sQuery(id+"F0.wireOp",EDGE,"E14.bottom");Q3=makeQuery(id+"F1.opExtrude","CAP_EDGE",EDGE,{"disambiguationData":[OSD([subQ0]),TDD([makeQuery(id+"F0.imprint","IMPRINT",EDGE,{"disambiguationData":[TD([[makeQuery(id+"F0.imprint","INTERSECT",VERTEX,{"derivedFrom":[sQuery(id+"F0.wireOp",EDGE,"E8.left"),subQ0]}),-1.0]])],"derivedFrom":subQ0})])],"isStart":false});}
            var Q4;
            {var subQ0=sQuery(id+"F0.wireOp",EDGE,"E8.left");Q4=makeQuery(id+"F1.opExtrude","CAP_EDGE",EDGE,{"disambiguationData":[OSD([subQ0]),TDD([makeQuery(id+"F0.imprint","IMPRINT",EDGE,{"disambiguationData":[TD([[makeQuery(id+"F0.imprint","INTERSECT",VERTEX,{"derivedFrom":[subQ0,sQuery(id+"F0.wireOp",EDGE,"E14.bottom")]}),-1.0]])],"derivedFrom":subQ0})])],"isStart":false});}
            var Q5;
            {var subQ0=sQuery(id+"F0.wireOp",EDGE,"E14.top");Q5=makeQuery(id+"F1.opExtrude","CAP_EDGE",EDGE,{"disambiguationData":[OSD([subQ0]),TDD([makeQuery(id+"F0.imprint","IMPRINT",EDGE,{"disambiguationData":[TD([[makeQuery(id+"F0.imprint","INTERSECT",VERTEX,{"derivedFrom":[sQuery(id+"F0.wireOp",EDGE,"E8.left"),subQ0]}),-1.0]])],"derivedFrom":subQ0})])],"isStart":false});}
            var Q6;
            {var subQ0=sQuery(id+"F0.wireOp",EDGE,"E16");Q6=makeQuery(id+"F1.opExtrude","CAP_EDGE",EDGE,{"disambiguationData":[OSD([subQ0]),TDD([makeQuery(id+"F0.imprint","IMPRINT",EDGE,{"disambiguationData":[TD([[makeQuery(id+"F0.imprint","INTERSECT",VERTEX,{"derivedFrom":[sQuery(id+"F0.wireOp",EDGE,"E14.bottom"),subQ0]}),-1.0]])],"derivedFrom":subQ0})])],"isStart":false});}
            var Q7;
            {var subQ0=sQuery(id+"F0.wireOp",EDGE,"E13.bottom");Q7=makeQuery(id+"F1.opExtrude","CAP_EDGE",EDGE,{"disambiguationData":[OSD([subQ0]),TDD([makeQuery(id+"F0.imprint","IMPRINT",EDGE,{"disambiguationData":[TD([[makeQuery(id+"F0.imprint","INTERSECT",VERTEX,{"derivedFrom":[sQuery(id+"F0.wireOp",EDGE,"E8.left"),subQ0]}),-1.0]])],"derivedFrom":subQ0})])],"isStart":false});}
            var Q8;
            {var subQ0=sQuery(id+"F0.wireOp",EDGE,"E16");Q8=makeQuery(id+"F1.opExtrude","CAP_EDGE",EDGE,{"disambiguationData":[OSD([subQ0]),TDD([makeQuery(id+"F0.imprint","IMPRINT",EDGE,{"disambiguationData":[TD([[makeQuery(id+"F0.imprint","INTERSECT",VERTEX,{"derivedFrom":[subQ0,sQuery(id+"F0.wireOp",EDGE,"E17")]}),-1.0]])],"derivedFrom":subQ0})])],"isStart":false});}
            var Q9;
            Q9=makeQuery(id+"F1.opExtrude","CAP_EDGE",EDGE,{"disambiguationData":[OSD([sQuery(id+"F0.wireOp",EDGE,"E17")])],"isStart":false});
            var Q10;
            {var subQ0=sQuery(id+"F0.wireOp",EDGE,"E8.left");Q10=makeQuery(id+"F1.opExtrude","CAP_EDGE",EDGE,{"disambiguationData":[OSD([subQ0]),TDD([makeQuery(id+"F0.imprint","IMPRINT",EDGE,{"disambiguationData":[TD([[makeQuery(id+"F0.imprint","INTERSECT",VERTEX,{"derivedFrom":[subQ0,sQuery(id+"F0.wireOp",EDGE,"E17")]}),-1.0]])],"derivedFrom":subQ0})])],"isStart":false});}
            var Q11;
            {var subQ0=sQuery(id+"F0.wireOp",EDGE,"E13.top");Q11=makeQuery(id+"F1.opExtrude","CAP_EDGE",EDGE,{"disambiguationData":[OSD([subQ0]),TDD([makeQuery(id+"F0.imprint","IMPRINT",EDGE,{"disambiguationData":[TD([[makeQuery(id+"F0.imprint","INTERSECT",VERTEX,{"derivedFrom":[sQuery(id+"F0.wireOp",EDGE,"E8.left"),subQ0]}),-1.0]])],"derivedFrom":subQ0})])],"isStart":false});}
            var Q12;
            {var subQ0=sQuery(id+"F0.wireOp",EDGE,"E16");Q12=makeQuery(id+"F1.opExtrude","CAP_EDGE",EDGE,{"disambiguationData":[OSD([subQ0]),TDD([makeQuery(id+"F0.imprint","IMPRINT",EDGE,{"disambiguationData":[TD([[makeQuery(id+"F0.imprint","INTERSECT",VERTEX,{"derivedFrom":[subQ0,sQuery(id+"F0.wireOp",EDGE,"E27")]}),1.0]])],"derivedFrom":subQ0})])],"isStart":false});}
            var Q13;
            Q13=makeQuery(id+"F1.opExtrude","CAP_EDGE",EDGE,{"disambiguationData":[OSD([sQuery(id+"F0.wireOp",EDGE,"E27")])],"isStart":false});
            var Q14;
            {var subQ0=sQuery(id+"F0.wireOp",EDGE,"E8.left");Q14=makeQuery(id+"F1.opExtrude","CAP_EDGE",EDGE,{"disambiguationData":[OSD([subQ0]),TDD([makeQuery(id+"F0.imprint","IMPRINT",EDGE,{"disambiguationData":[TD([[makeQuery(id+"F0.imprint","INTERSECT",VERTEX,{"derivedFrom":[subQ0,sQuery(id+"F0.wireOp",EDGE,"E13.top")]}),-1.0]])],"derivedFrom":subQ0})])],"isStart":false});}
            var Q15;
            {var subQ0=sQuery(id+"F0.wireOp",EDGE,"E6.right");Q15=makeQuery(id+"F1.opExtrude","CAP_EDGE",EDGE,{"disambiguationData":[OSD([subQ0]),TDD([makeQuery(id+"F0.imprint","IMPRINT",EDGE,{"disambiguationData":[TD([[makeQuery(id+"F0.imprint","INTERSECT",VERTEX,{"derivedFrom":[sQuery(id+"F0.wireOp",EDGE,"E6.top"),subQ0]}),1.0]])],"derivedFrom":subQ0})])],"isStart":false});}
            var Q16;
            {var subQ0=sQuery(id+"F0.wireOp",EDGE,"E6.left");Q16=makeQuery(id+"F1.opExtrude","CAP_EDGE",EDGE,{"disambiguationData":[OSD([subQ0]),TDD([makeQuery(id+"F0.imprint","IMPRINT",EDGE,{"disambiguationData":[TD([[makeQuery(id+"F0.imprint","INTERSECT",VERTEX,{"derivedFrom":[sQuery(id+"F0.wireOp",EDGE,"E6.top"),subQ0]}),1.0]])],"derivedFrom":subQ0})])],"isStart":false});}
            var Q17;
            {var subQ0=sQuery(id+"F0.wireOp",EDGE,"E13.top");Q17=makeQuery(id+"F1.opExtrude","CAP_EDGE",EDGE,{"disambiguationData":[OSD([subQ0]),TDD([makeQuery(id+"F0.imprint","IMPRINT",EDGE,{"disambiguationData":[TD([[makeQuery(id+"F0.imprint","INTERSECT",VERTEX,{"derivedFrom":[sQuery(id+"F0.wireOp",EDGE,"E6.left"),subQ0]}),-1.0]])],"derivedFrom":subQ0})])],"isStart":false});}
            var Q18;
            Q18=makeQuery(id+"F1.opExtrude","CAP_EDGE",EDGE,{"disambiguationData":[OSD([sQuery(id+"F0.wireOp",EDGE,"E6.top")])],"isStart":false});
            var Q19;
            {var subQ0=sQuery(id+"F0.wireOp",EDGE,"E14.top");Q19=makeQuery(id+"F1.opExtrude","CAP_EDGE",EDGE,{"disambiguationData":[OSD([subQ0]),TDD([makeQuery(id+"F0.imprint","IMPRINT",EDGE,{"disambiguationData":[TD([[makeQuery(id+"F0.imprint","INTERSECT",VERTEX,{"derivedFrom":[sQuery(id+"F0.wireOp",EDGE,"E6.left"),subQ0]}),-1.0]])],"derivedFrom":subQ0})])],"isStart":false});}
            var Q20;
            {var subQ0=sQuery(id+"F0.wireOp",EDGE,"E6.right");Q20=makeQuery(id+"F1.opExtrude","CAP_EDGE",EDGE,{"disambiguationData":[OSD([subQ0]),TDD([makeQuery(id+"F0.imprint","IMPRINT",EDGE,{"disambiguationData":[TD([[makeQuery(id+"F0.imprint","INTERSECT",VERTEX,{"derivedFrom":[subQ0,sQuery(id+"F0.wireOp",EDGE,"E14.bottom")]}),-1.0]])],"derivedFrom":subQ0})])],"isStart":false});}
            var Q21;
            {var subQ0=sQuery(id+"F0.wireOp",EDGE,"E6.left");Q21=makeQuery(id+"F1.opExtrude","CAP_EDGE",EDGE,{"disambiguationData":[OSD([subQ0]),TDD([makeQuery(id+"F0.imprint","IMPRINT",EDGE,{"disambiguationData":[TD([[makeQuery(id+"F0.imprint","INTERSECT",VERTEX,{"derivedFrom":[subQ0,sQuery(id+"F0.wireOp",EDGE,"E14.bottom")]}),-1.0]])],"derivedFrom":subQ0})])],"isStart":false});}
            var Q22;
            {var subQ0=sQuery(id+"F0.wireOp",EDGE,"E14.bottom");Q22=makeQuery(id+"F1.opExtrude","CAP_EDGE",EDGE,{"disambiguationData":[OSD([subQ0]),TDD([makeQuery(id+"F0.imprint","IMPRINT",EDGE,{"disambiguationData":[TD([[makeQuery(id+"F0.imprint","INTERSECT",VERTEX,{"derivedFrom":[sQuery(id+"F0.wireOp",EDGE,"E6.left"),subQ0]}),-1.0]])],"derivedFrom":subQ0})])],"isStart":false});}
            var Q23;
            {var subQ0=sQuery(id+"F0.wireOp",EDGE,"E13.bottom");Q23=makeQuery(id+"F1.opExtrude","CAP_EDGE",EDGE,{"disambiguationData":[OSD([subQ0]),TDD([makeQuery(id+"F0.imprint","IMPRINT",EDGE,{"disambiguationData":[TD([[makeQuery(id+"F0.imprint","INTERSECT",VERTEX,{"derivedFrom":[sQuery(id+"F0.wireOp",EDGE,"E6.left"),subQ0]}),-1.0]])],"derivedFrom":subQ0})])],"isStart":false});}
            var Q24;
            {var subQ0=sQuery(id+"F0.wireOp",EDGE,"E5.right");Q24=makeQuery(id+"F1.opExtrude","CAP_EDGE",EDGE,{"disambiguationData":[OSD([subQ0]),TDD([makeQuery(id+"F0.imprint","IMPRINT",EDGE,{"disambiguationData":[TD([[makeQuery(id+"F0.imprint","INTERSECT",VERTEX,{"derivedFrom":[subQ0,sQuery(id+"F0.wireOp",EDGE,"E13.top")]}),-1.0]])],"derivedFrom":subQ0})])],"isStart":false});}
            var Q25;
            Q25=makeQuery(id+"F1.opExtrude","CAP_EDGE",EDGE,{"disambiguationData":[OSD([sQuery(id+"F0.wireOp",EDGE,"E28")])],"isStart":false});
            var Q26;
            {var subQ0=sQuery(id+"F0.wireOp",EDGE,"E4.right");Q26=makeQuery(id+"F1.opExtrude","CAP_EDGE",EDGE,{"disambiguationData":[OSD([subQ0]),TDD([makeQuery(id+"F0.imprint","IMPRINT",EDGE,{"disambiguationData":[TD([[makeQuery(id+"F0.imprint","INTERSECT",VERTEX,{"derivedFrom":[subQ0,sQuery(id+"F0.wireOp",EDGE,"E28")]}),-1.0]])],"derivedFrom":subQ0})])],"isStart":false});}
            var Q27;
            {var subQ0=sQuery(id+"F0.wireOp",EDGE,"E13.top");Q27=makeQuery(id+"F1.opExtrude","CAP_EDGE",EDGE,{"disambiguationData":[OSD([subQ0]),TDD([makeQuery(id+"F0.imprint","IMPRINT",EDGE,{"disambiguationData":[TD([[makeQuery(id+"F0.imprint","INTERSECT",VERTEX,{"derivedFrom":[sQuery(id+"F0.wireOp",EDGE,"E5.right"),subQ0]}),1.0]])],"derivedFrom":subQ0})])],"isStart":false});}
            var Q28;
            {var subQ0=sQuery(id+"F0.wireOp",EDGE,"E14.top");Q28=makeQuery(id+"F1.opExtrude","CAP_EDGE",EDGE,{"disambiguationData":[OSD([subQ0]),TDD([makeQuery(id+"F0.imprint","IMPRINT",EDGE,{"disambiguationData":[TD([[makeQuery(id+"F0.imprint","INTERSECT",VERTEX,{"derivedFrom":[sQuery(id+"F0.wireOp",EDGE,"E4.right"),subQ0]}),-1.0]])],"derivedFrom":subQ0})])],"isStart":false});}
            var Q29;
            {var subQ0=sQuery(id+"F0.wireOp",EDGE,"E5.right");Q29=makeQuery(id+"F1.opExtrude","CAP_EDGE",EDGE,{"disambiguationData":[OSD([subQ0]),TDD([makeQuery(id+"F0.imprint","IMPRINT",EDGE,{"disambiguationData":[TD([[makeQuery(id+"F0.imprint","INTERSECT",VERTEX,{"derivedFrom":[subQ0,sQuery(id+"F0.wireOp",EDGE,"E14.bottom")]}),-1.0]])],"derivedFrom":subQ0})])],"isStart":false});}
            var Q30;
            {var subQ0=sQuery(id+"F0.wireOp",EDGE,"E4.right");Q30=makeQuery(id+"F1.opExtrude","CAP_EDGE",EDGE,{"disambiguationData":[OSD([subQ0]),TDD([makeQuery(id+"F0.imprint","IMPRINT",EDGE,{"disambiguationData":[TD([[makeQuery(id+"F0.imprint","INTERSECT",VERTEX,{"derivedFrom":[subQ0,sQuery(id+"F0.wireOp",EDGE,"E14.top")]}),-1.0]])],"derivedFrom":subQ0})])],"isStart":false});}
            var Q31;
            {var subQ0=sQuery(id+"F0.wireOp",EDGE,"E14.bottom");Q31=makeQuery(id+"F1.opExtrude","CAP_EDGE",EDGE,{"disambiguationData":[OSD([subQ0]),TDD([makeQuery(id+"F0.imprint","IMPRINT",EDGE,{"disambiguationData":[TD([[makeQuery(id+"F0.imprint","INTERSECT",VERTEX,{"derivedFrom":[sQuery(id+"F0.wireOp",EDGE,"E5.right"),subQ0]}),1.0]])],"derivedFrom":subQ0})])],"isStart":false});}
            var Q32;
            {var subQ0=sQuery(id+"F0.wireOp",EDGE,"E13.bottom");Q32=makeQuery(id+"F1.opExtrude","CAP_EDGE",EDGE,{"disambiguationData":[OSD([subQ0]),TDD([makeQuery(id+"F0.imprint","IMPRINT",EDGE,{"disambiguationData":[TD([[makeQuery(id+"F0.imprint","INTERSECT",VERTEX,{"derivedFrom":[sQuery(id+"F0.wireOp",EDGE,"E4.right"),subQ0]}),-1.0]])],"derivedFrom":subQ0})])],"isStart":false});}
            var Q33;
            Q33=makeQuery(id+"F1.opExtrude","CAP_EDGE",EDGE,{"disambiguationData":[OSD([sQuery(id+"F0.wireOp",EDGE,"E0.right")])],"isStart":false});
            var Q34;
            Q34=makeQuery(id+"F1.opExtrude","CAP_EDGE",EDGE,{"disambiguationData":[OSD([sQuery(id+"F0.wireOp",EDGE,"E0.top")])],"isStart":false});
            var Q35;
            Q35=makeQuery(id+"F1.opExtrude","CAP_EDGE",EDGE,{"disambiguationData":[OSD([sQuery(id+"F0.wireOp",EDGE,"E0.left")])],"isStart":false});
            var Q36;
            Q36=makeQuery(id+"F1.opExtrude","CAP_EDGE",EDGE,{"disambiguationData":[OSD([sQuery(id+"F0.wireOp",EDGE,"E0.bottom")])],"isStart":false});
            var Q37;
            {var subQ0=sQuery(id+"F0.wireOp",EDGE,"E14.top");Q37=makeQuery(id+"F1.opExtrude","CAP_EDGE",EDGE,{"disambiguationData":[OSD([subQ0]),TDD([makeQuery(id+"F0.imprint","IMPRINT",EDGE,{"disambiguationData":[TD([[makeQuery(id+"F0.imprint","INTERSECT",VERTEX,{"derivedFrom":[sQuery(id+"F0.wireOp",EDGE,"E3.right"),subQ0]}),1.0]])],"derivedFrom":subQ0})])],"isStart":false});}
            var Q38;
            Q38=makeQuery(id+"F1.opExtrude","SWEPT_EDGE",EDGE,{"disambiguationData":[OSD([sQuery(id+"F0.wireOp",EDGE,"E10.right"),sQuery(id+"F0.wireOp",EDGE,"E14.bottom")])]});
            var Q39;
            {var subQ0=sQuery(id+"F0.wireOp",EDGE,"E23");Q39=makeQuery(id+"F1.opExtrude","CAP_EDGE",EDGE,{"disambiguationData":[OSD([subQ0]),TDD([makeQuery(id+"F0.imprint","IMPRINT",EDGE,{"disambiguationData":[TD([[makeQuery(id+"F0.imprint","INTERSECT",VERTEX,{"derivedFrom":[subQ0,sQuery(id+"F0.wireOp",EDGE,"E30")]}),1.0]])],"derivedFrom":subQ0})])],"isStart":false});}
            var Q40;
            {var subQ0=sQuery(id+"F0.wireOp",EDGE,"E2.right");Q40=makeQuery(id+"F1.opExtrude","CAP_EDGE",EDGE,{"disambiguationData":[OSD([subQ0]),TDD([makeQuery(id+"F0.imprint","IMPRINT",EDGE,{"disambiguationData":[TD([[makeQuery(id+"F0.imprint","INTERSECT",VERTEX,{"derivedFrom":[subQ0,sQuery(id+"F0.wireOp",EDGE,"E3.bottom")]}),1.0]])],"derivedFrom":subQ0})])],"isStart":false});}
            var Q41;
            {var subQ0=sQuery(id+"F0.wireOp",EDGE,"E1.left");Q41=makeQuery(id+"F1.opExtrude","CAP_EDGE",EDGE,{"disambiguationData":[OSD([subQ0]),TDD([makeQuery(id+"F0.imprint","IMPRINT",EDGE,{"disambiguationData":[TD([[makeQuery(id+"F0.imprint","INTERSECT",VERTEX,{"derivedFrom":[subQ0,sQuery(id+"F0.wireOp",EDGE,"E13.bottom")]}),1.0]])],"derivedFrom":subQ0})])],"isStart":false});}
            var Q42;
            {var subQ0=sQuery(id+"F0.wireOp",EDGE,"E2.right");Q42=makeQuery(id+"F1.opExtrude","CAP_EDGE",EDGE,{"disambiguationData":[OSD([subQ0]),TDD([makeQuery(id+"F0.imprint","IMPRINT",EDGE,{"disambiguationData":[TD([[makeQuery(id+"F0.imprint","INTERSECT",VERTEX,{"derivedFrom":[subQ0,sQuery(id+"F0.wireOp",EDGE,"E14.bottom")]}),-1.0]])],"derivedFrom":subQ0})])],"isStart":false});}
            var Q43;
            Q43=makeQuery(id+"F1.opExtrude","CAP_EDGE",EDGE,{"disambiguationData":[OSD([sQuery(id+"F0.wireOp",EDGE,"E3.bottom")])],"isStart":false});
            var Q44;
            Q44=makeQuery(id+"F1.opExtrude","SWEPT_EDGE",EDGE,{"disambiguationData":[OSD([sQuery(id+"F0.wireOp",EDGE,"E9.right"),sQuery(id+"F0.wireOp",EDGE,"E13.top")])]});
            var Q45;
            {var subQ0=sQuery(id+"F0.wireOp",EDGE,"E13.top");Q45=makeQuery(id+"F1.opExtrude","CAP_EDGE",EDGE,{"disambiguationData":[OSD([subQ0]),TDD([makeQuery(id+"F0.imprint","IMPRINT",EDGE,{"disambiguationData":[TD([[makeQuery(id+"F0.imprint","INTERSECT",VERTEX,{"derivedFrom":[sQuery(id+"F0.wireOp",EDGE,"E9.right"),subQ0]}),-1.0]])],"derivedFrom":subQ0})])],"isStart":false});}
            var Q46;
            {var subQ0=sQuery(id+"F0.wireOp",EDGE,"E11.left");Q46=makeQuery(id+"F1.opExtrude","CAP_EDGE",EDGE,{"disambiguationData":[OSD([subQ0]),TDD([makeQuery(id+"F0.imprint","IMPRINT",EDGE,{"disambiguationData":[TD([[makeQuery(id+"F0.imprint","INTERSECT",VERTEX,{"derivedFrom":[subQ0,sQuery(id+"F0.wireOp",EDGE,"E14.bottom")]}),-1.0]])],"derivedFrom":subQ0})])],"isStart":false});}
            var Q47;
            {var subQ0=sQuery(id+"F0.wireOp",EDGE,"E10.left");Q47=makeQuery(id+"F1.opExtrude","CAP_EDGE",EDGE,{"disambiguationData":[OSD([subQ0]),TDD([makeQuery(id+"F0.imprint","IMPRINT",EDGE,{"disambiguationData":[TD([[makeQuery(id+"F0.imprint","INTERSECT",VERTEX,{"derivedFrom":[sQuery(id+"F0.wireOp",EDGE,"E10.bottom"),subQ0]}),-1.0]])],"derivedFrom":subQ0})])],"isStart":false});}
            var Q48;
            {var subQ0=sQuery(id+"F0.wireOp",EDGE,"E9.right");Q48=makeQuery(id+"F1.opExtrude","CAP_EDGE",EDGE,{"disambiguationData":[OSD([subQ0]),TDD([makeQuery(id+"F0.imprint","IMPRINT",EDGE,{"disambiguationData":[TD([[makeQuery(id+"F0.imprint","INTERSECT",VERTEX,{"derivedFrom":[subQ0,sQuery(id+"F0.wireOp",EDGE,"E30")]}),1.0]])],"derivedFrom":subQ0})])],"isStart":false});}
            var Q49;
            Q49=makeQuery(id+"F1.opExtrude","CAP_EDGE",EDGE,{"disambiguationData":[OSD([sQuery(id+"F0.wireOp",EDGE,"E22")])],"isStart":false});
            var Q50;
            {var subQ0=sQuery(id+"F0.wireOp",EDGE,"E6.right");Q50=makeQuery(id+"F1.opExtrude","CAP_EDGE",EDGE,{"disambiguationData":[OSD([subQ0]),TDD([makeQuery(id+"F0.imprint","IMPRINT",EDGE,{"disambiguationData":[TD([[makeQuery(id+"F0.imprint","INTERSECT",VERTEX,{"derivedFrom":[subQ0,sQuery(id+"F0.wireOp",EDGE,"E21")]}),-1.0]])],"derivedFrom":subQ0})])],"isStart":false});}
            var Q51;
            Q51=makeQuery(id+"F1.opExtrude","CAP_EDGE",EDGE,{"disambiguationData":[OSD([sQuery(id+"F0.wireOp",EDGE,"E20")])],"isStart":false});
            var Q52;
            {var subQ0=sQuery(id+"F0.wireOp",EDGE,"E3.right");Q52=makeQuery(id+"F1.opExtrude","CAP_EDGE",EDGE,{"disambiguationData":[OSD([subQ0]),TDD([makeQuery(id+"F0.imprint","IMPRINT",EDGE,{"disambiguationData":[TD([[makeQuery(id+"F0.imprint","INTERSECT",VERTEX,{"derivedFrom":[subQ0,sQuery(id+"F0.wireOp",EDGE,"E14.top")]}),-1.0]])],"derivedFrom":subQ0})])],"isStart":false});}
            var Q53;
            {var subQ0=sQuery(id+"F0.wireOp",EDGE,"E13.top");Q53=makeQuery(id+"F1.opExtrude","CAP_EDGE",EDGE,{"disambiguationData":[OSD([subQ0]),TDD([makeQuery(id+"F0.imprint","IMPRINT",EDGE,{"disambiguationData":[TD([[makeQuery(id+"F0.imprint","INTERSECT",VERTEX,{"derivedFrom":[sQuery(id+"F0.wireOp",EDGE,"E10.left"),subQ0]}),-1.0]])],"derivedFrom":subQ0})])],"isStart":false});}
            var Q54;
            Q54=makeQuery(id+"F1.opExtrude","CAP_EDGE",EDGE,{"disambiguationData":[OSD([sQuery(id+"F0.wireOp",EDGE,"E31")])],"isStart":false});
            var Q55;
            {var subQ0=sQuery(id+"F0.wireOp",EDGE,"E14.bottom");Q55=makeQuery(id+"F1.opExtrude","CAP_EDGE",EDGE,{"disambiguationData":[OSD([subQ0]),TDD([makeQuery(id+"F0.imprint","IMPRINT",EDGE,{"disambiguationData":[TD([[makeQuery(id+"F0.imprint","INTERSECT",VERTEX,{"derivedFrom":[sQuery(id+"F0.wireOp",EDGE,"E10.left"),subQ0]}),-1.0]])],"derivedFrom":subQ0})])],"isStart":false});}
            var Q56;
            {var subQ0=sQuery(id+"F0.wireOp",EDGE,"E24");Q56=makeQuery(id+"F1.opExtrude","CAP_EDGE",EDGE,{"disambiguationData":[OSD([subQ0]),TDD([makeQuery(id+"F0.imprint","IMPRINT",EDGE,{"disambiguationData":[TD([[makeQuery(id+"F0.imprint","INTERSECT",VERTEX,{"derivedFrom":[subQ0,sQuery(id+"F0.wireOp",EDGE,"E31")]}),1.0]])],"derivedFrom":subQ0})])],"isStart":false});}
            var Q57;
            Q57=makeQuery(id+"F1.opExtrude","SWEPT_EDGE",EDGE,{"disambiguationData":[OSD([sQuery(id+"F0.wireOp",EDGE,"E3.right"),sQuery(id+"F0.wireOp",EDGE,"E14.top")])]});
            var Q58;
            {var subQ0=sQuery(id+"F0.wireOp",EDGE,"E10.right");Q58=makeQuery(id+"F1.opExtrude","CAP_EDGE",EDGE,{"disambiguationData":[OSD([subQ0]),TDD([makeQuery(id+"F0.imprint","IMPRINT",EDGE,{"disambiguationData":[TD([[makeQuery(id+"F0.imprint","INTERSECT",VERTEX,{"derivedFrom":[sQuery(id+"F0.wireOp",EDGE,"E10.bottom"),subQ0]}),-1.0]])],"derivedFrom":subQ0})])],"isStart":false});}
            var Q59;
            {var subQ0=sQuery(id+"F0.wireOp",EDGE,"E13.bottom");Q59=makeQuery(id+"F1.opExtrude","CAP_EDGE",EDGE,{"disambiguationData":[OSD([subQ0]),TDD([makeQuery(id+"F0.imprint","IMPRINT",EDGE,{"disambiguationData":[TD([[makeQuery(id+"F0.imprint","INTERSECT",VERTEX,{"derivedFrom":[subQ0,sQuery(id+"F0.wireOp",EDGE,"E15")]}),-1.0]])],"derivedFrom":subQ0})])],"isStart":false});}
            var Q60;
            {var subQ0=sQuery(id+"F0.wireOp",EDGE,"E4.right");Q60=makeQuery(id+"F1.opExtrude","CAP_EDGE",EDGE,{"disambiguationData":[OSD([subQ0]),TDD([makeQuery(id+"F0.imprint","IMPRINT",EDGE,{"disambiguationData":[TD([[makeQuery(id+"F0.imprint","INTERSECT",VERTEX,{"derivedFrom":[subQ0,sQuery(id+"F0.wireOp",EDGE,"E13.bottom")]}),-1.0]])],"derivedFrom":subQ0})])],"isStart":false});}
            var Q61;
            {var subQ0=sQuery(id+"F0.wireOp",EDGE,"E15");Q61=makeQuery(id+"F1.opExtrude","CAP_EDGE",EDGE,{"disambiguationData":[OSD([subQ0]),TDD([makeQuery(id+"F0.imprint","IMPRINT",EDGE,{"disambiguationData":[TD([[makeQuery(id+"F0.imprint","INTERSECT",VERTEX,{"derivedFrom":[sQuery(id+"F0.wireOp",EDGE,"E14.bottom"),subQ0]}),-1.0]])],"derivedFrom":subQ0})])],"isStart":false});}
            var Q62;
            {var subQ0=sQuery(id+"F0.wireOp",EDGE,"E2.left");Q62=makeQuery(id+"F1.opExtrude","CAP_EDGE",EDGE,{"disambiguationData":[OSD([subQ0]),TDD([makeQuery(id+"F0.imprint","IMPRINT",EDGE,{"disambiguationData":[TD([[makeQuery(id+"F0.imprint","INTERSECT",VERTEX,{"derivedFrom":[subQ0,sQuery(id+"F0.wireOp",EDGE,"E14.bottom")]}),-1.0]])],"derivedFrom":subQ0})])],"isStart":false});}
            var Q63;
            {var subQ0=sQuery(id+"F0.wireOp",EDGE,"E11.right");Q63=makeQuery(id+"F1.opExtrude","CAP_EDGE",EDGE,{"disambiguationData":[OSD([subQ0]),TDD([makeQuery(id+"F0.imprint","IMPRINT",EDGE,{"disambiguationData":[TD([[makeQuery(id+"F0.imprint","INTERSECT",VERTEX,{"derivedFrom":[subQ0,sQuery(id+"F0.wireOp",EDGE,"E14.bottom")]}),-1.0]])],"derivedFrom":subQ0})])],"isStart":false});}
            var Q64;
            {var subQ0=sQuery(id+"F0.wireOp",EDGE,"E14.top");Q64=makeQuery(id+"F1.opExtrude","CAP_EDGE",EDGE,{"disambiguationData":[OSD([subQ0]),TDD([makeQuery(id+"F0.imprint","IMPRINT",EDGE,{"disambiguationData":[TD([[makeQuery(id+"F0.imprint","INTERSECT",VERTEX,{"derivedFrom":[sQuery(id+"F0.wireOp",EDGE,"E10.left"),subQ0]}),-1.0]])],"derivedFrom":subQ0})])],"isStart":false});}
            var Q65;
            {var subQ0=sQuery(id+"F0.wireOp",EDGE,"E2.right");Q65=makeQuery(id+"F1.opExtrude","CAP_EDGE",EDGE,{"disambiguationData":[OSD([subQ0]),TDD([makeQuery(id+"F0.imprint","IMPRINT",EDGE,{"disambiguationData":[TD([[makeQuery(id+"F0.imprint","INTERSECT",VERTEX,{"derivedFrom":[subQ0,sQuery(id+"F0.wireOp",EDGE,"E19")]}),-1.0]])],"derivedFrom":subQ0})])],"isStart":false});}
            var Q66;
            {var subQ0=sQuery(id+"F0.wireOp",EDGE,"E11.right");Q66=makeQuery(id+"F1.opExtrude","CAP_EDGE",EDGE,{"disambiguationData":[OSD([subQ0]),TDD([makeQuery(id+"F0.imprint","IMPRINT",EDGE,{"disambiguationData":[TD([[makeQuery(id+"F0.imprint","INTERSECT",VERTEX,{"derivedFrom":[sQuery(id+"F0.wireOp",EDGE,"E11.bottom"),subQ0]}),-1.0]])],"derivedFrom":subQ0})])],"isStart":false});}
            var Q67;
            {var subQ0=sQuery(id+"F0.wireOp",EDGE,"E5.right");Q67=makeQuery(id+"F1.opExtrude","CAP_EDGE",EDGE,{"disambiguationData":[OSD([subQ0]),TDD([makeQuery(id+"F0.imprint","IMPRINT",EDGE,{"disambiguationData":[TD([[makeQuery(id+"F0.imprint","INTERSECT",VERTEX,{"derivedFrom":[subQ0,sQuery(id+"F0.wireOp",EDGE,"E20")]}),-1.0]])],"derivedFrom":subQ0})])],"isStart":false});}
            var Q68;
            {var subQ0=sQuery(id+"F0.wireOp",EDGE,"E14.bottom");Q68=makeQuery(id+"F1.opExtrude","CAP_EDGE",EDGE,{"disambiguationData":[OSD([subQ0]),TDD([makeQuery(id+"F0.imprint","IMPRINT",EDGE,{"disambiguationData":[TD([[makeQuery(id+"F0.imprint","INTERSECT",VERTEX,{"derivedFrom":[sQuery(id+"F0.wireOp",EDGE,"E2.right"),subQ0]}),-1.0]])],"derivedFrom":subQ0})])],"isStart":false});}
            var Q69;
            {var subQ0=sQuery(id+"F0.wireOp",EDGE,"E11.right");Q69=makeQuery(id+"F1.opExtrude","CAP_EDGE",EDGE,{"disambiguationData":[OSD([subQ0]),TDD([makeQuery(id+"F0.imprint","IMPRINT",EDGE,{"disambiguationData":[TD([[makeQuery(id+"F0.imprint","INTERSECT",VERTEX,{"derivedFrom":[sQuery(id+"F0.wireOp",EDGE,"E11.top"),subQ0]}),1.0]])],"derivedFrom":subQ0})])],"isStart":false});}
            var Q70;
            {var subQ0=sQuery(id+"F0.wireOp",EDGE,"E14.bottom");Q70=makeQuery(id+"F1.opExtrude","CAP_EDGE",EDGE,{"disambiguationData":[OSD([subQ0]),TDD([makeQuery(id+"F0.imprint","IMPRINT",EDGE,{"disambiguationData":[TD([[makeQuery(id+"F0.imprint","INTERSECT",VERTEX,{"derivedFrom":[sQuery(id+"F0.wireOp",EDGE,"E1.left"),subQ0]}),-1.0]])],"derivedFrom":subQ0})])],"isStart":false});}
            var Q71;
            {var subQ0=sQuery(id+"F0.wireOp",EDGE,"E2.left");Q71=makeQuery(id+"F1.opExtrude","CAP_EDGE",EDGE,{"disambiguationData":[OSD([subQ0]),TDD([makeQuery(id+"F0.imprint","IMPRINT",EDGE,{"disambiguationData":[TD([[makeQuery(id+"F0.imprint","INTERSECT",VERTEX,{"derivedFrom":[subQ0,sQuery(id+"F0.wireOp",EDGE,"E13.top")]}),-1.0]])],"derivedFrom":subQ0})])],"isStart":false});}
            var Q72;
            Q72=makeQuery(id+"F1.opExtrude","SWEPT_EDGE",EDGE,{"disambiguationData":[OSD([sQuery(id+"F0.wireOp",EDGE,"E6.right"),sQuery(id+"F0.wireOp",EDGE,"E14.top")])]});
            var Q73;
            Q73=makeQuery(id+"F1.opExtrude","SWEPT_EDGE",EDGE,{"disambiguationData":[OSD([sQuery(id+"F0.wireOp",EDGE,"E10.right"),sQuery(id+"F0.wireOp",EDGE,"E13.bottom")])]});
            var Q74;
            {var subQ0=sQuery(id+"F0.wireOp",EDGE,"E11.left");Q74=makeQuery(id+"F1.opExtrude","CAP_EDGE",EDGE,{"disambiguationData":[OSD([subQ0]),TDD([makeQuery(id+"F0.imprint","IMPRINT",EDGE,{"disambiguationData":[TD([[makeQuery(id+"F0.imprint","INTERSECT",VERTEX,{"derivedFrom":[sQuery(id+"F0.wireOp",EDGE,"E11.top"),subQ0]}),1.0]])],"derivedFrom":subQ0})])],"isStart":false});}
            var Q75;
            {var subQ0=sQuery(id+"F0.wireOp",EDGE,"E1.right");Q75=makeQuery(id+"F1.opExtrude","CAP_EDGE",EDGE,{"disambiguationData":[OSD([subQ0]),TDD([makeQuery(id+"F0.imprint","IMPRINT",EDGE,{"disambiguationData":[TD([[makeQuery(id+"F0.imprint","INTERSECT",VERTEX,{"derivedFrom":[subQ0,sQuery(id+"F0.wireOp",EDGE,"E13.top")]}),-1.0]])],"derivedFrom":subQ0})])],"isStart":false});}
            var Q76;
            {var subQ0=sQuery(id+"F0.wireOp",EDGE,"E1.right");Q76=makeQuery(id+"F1.opExtrude","CAP_EDGE",EDGE,{"disambiguationData":[OSD([subQ0]),TDD([makeQuery(id+"F0.imprint","IMPRINT",EDGE,{"disambiguationData":[TD([[makeQuery(id+"F0.imprint","INTERSECT",VERTEX,{"derivedFrom":[subQ0,sQuery(id+"F0.wireOp",EDGE,"E14.bottom")]}),-1.0]])],"derivedFrom":subQ0})])],"isStart":false});}
            var Q77;
            {var subQ0=sQuery(id+"F0.wireOp",EDGE,"E13.bottom");Q77=makeQuery(id+"F1.opExtrude","CAP_EDGE",EDGE,{"disambiguationData":[OSD([subQ0]),TDD([makeQuery(id+"F0.imprint","IMPRINT",EDGE,{"disambiguationData":[TD([[makeQuery(id+"F0.imprint","INTERSECT",VERTEX,{"derivedFrom":[sQuery(id+"F0.wireOp",EDGE,"E11.left"),subQ0]}),-1.0]])],"derivedFrom":subQ0})])],"isStart":false});}
            var Q78;
            {var subQ0=sQuery(id+"F0.wireOp",EDGE,"E3.right");Q78=makeQuery(id+"F1.opExtrude","CAP_EDGE",EDGE,{"disambiguationData":[OSD([subQ0]),TDD([makeQuery(id+"F0.imprint","IMPRINT",EDGE,{"disambiguationData":[TD([[makeQuery(id+"F0.imprint","INTERSECT",VERTEX,{"derivedFrom":[sQuery(id+"F0.wireOp",EDGE,"E3.bottom"),subQ0]}),-1.0]])],"derivedFrom":subQ0})])],"isStart":false});}
            var Q79;
            {var subQ0=sQuery(id+"F0.wireOp",EDGE,"E11.left");Q79=makeQuery(id+"F1.opExtrude","CAP_EDGE",EDGE,{"disambiguationData":[OSD([subQ0]),TDD([makeQuery(id+"F0.imprint","IMPRINT",EDGE,{"disambiguationData":[TD([[makeQuery(id+"F0.imprint","INTERSECT",VERTEX,{"derivedFrom":[sQuery(id+"F0.wireOp",EDGE,"E11.bottom"),subQ0]}),-1.0]])],"derivedFrom":subQ0})])],"isStart":false});}
            var Q80;
            {var subQ0=sQuery(id+"F0.wireOp",EDGE,"E15");Q80=makeQuery(id+"F1.opExtrude","CAP_EDGE",EDGE,{"disambiguationData":[OSD([subQ0]),TDD([makeQuery(id+"F0.imprint","IMPRINT",EDGE,{"disambiguationData":[TD([[makeQuery(id+"F0.imprint","INTERSECT",VERTEX,{"derivedFrom":[subQ0,sQuery(id+"F0.wireOp",EDGE,"E26")]}),-1.0]])],"derivedFrom":subQ0})])],"isStart":false});}
            var Q81;
            {var subQ0=sQuery(id+"F0.wireOp",EDGE,"E7.right");Q81=makeQuery(id+"F1.opExtrude","CAP_EDGE",EDGE,{"disambiguationData":[OSD([subQ0]),TDD([makeQuery(id+"F0.imprint","IMPRINT",EDGE,{"disambiguationData":[TD([[makeQuery(id+"F0.imprint","INTERSECT",VERTEX,{"derivedFrom":[subQ0,sQuery(id+"F0.wireOp",EDGE,"E13.top")]}),-1.0]])],"derivedFrom":subQ0})])],"isStart":false});}
            var Q82;
            {var subQ0=sQuery(id+"F0.wireOp",EDGE,"E13.bottom");Q82=makeQuery(id+"F1.opExtrude","CAP_EDGE",EDGE,{"disambiguationData":[OSD([subQ0]),TDD([makeQuery(id+"F0.imprint","IMPRINT",EDGE,{"disambiguationData":[TD([[makeQuery(id+"F0.imprint","INTERSECT",VERTEX,{"derivedFrom":[sQuery(id+"F0.wireOp",EDGE,"E10.left"),subQ0]}),-1.0]])],"derivedFrom":subQ0})])],"isStart":false});}
            var Q83;
            Q83=makeQuery(id+"F1.opExtrude","SWEPT_EDGE",EDGE,{"disambiguationData":[OSD([sQuery(id+"F0.wireOp",EDGE,"E6.right"),sQuery(id+"F0.wireOp",EDGE,"E14.bottom")])]});
            var Q84;
            {var subQ0=sQuery(id+"F0.wireOp",EDGE,"E23");Q84=makeQuery(id+"F1.opExtrude","CAP_EDGE",EDGE,{"disambiguationData":[OSD([subQ0]),TDD([makeQuery(id+"F0.imprint","IMPRINT",EDGE,{"disambiguationData":[TD([[makeQuery(id+"F0.imprint","INTERSECT",VERTEX,{"derivedFrom":[subQ0,sQuery(id+"F0.wireOp",EDGE,"E25")]}),-1.0]])],"derivedFrom":subQ0})])],"isStart":false});}
            var Q85;
            Q85=makeQuery(id+"F1.opExtrude","CAP_EDGE",EDGE,{"disambiguationData":[OSD([sQuery(id+"F0.wireOp",EDGE,"E29")])],"isStart":false});
            var Q86;
            {var subQ0=sQuery(id+"F0.wireOp",EDGE,"E13.top");Q86=makeQuery(id+"F1.opExtrude","CAP_EDGE",EDGE,{"disambiguationData":[OSD([subQ0]),TDD([makeQuery(id+"F0.imprint","IMPRINT",EDGE,{"disambiguationData":[TD([[makeQuery(id+"F0.imprint","INTERSECT",VERTEX,{"derivedFrom":[subQ0,sQuery(id+"F0.wireOp",EDGE,"E15")]}),-1.0]])],"derivedFrom":subQ0})])],"isStart":false});}
            var Q87;
            {var subQ0=sQuery(id+"F0.wireOp",EDGE,"E1.left");Q87=makeQuery(id+"F1.opExtrude","CAP_EDGE",EDGE,{"disambiguationData":[OSD([subQ0]),TDD([makeQuery(id+"F0.imprint","IMPRINT",EDGE,{"disambiguationData":[TD([[makeQuery(id+"F0.imprint","INTERSECT",VERTEX,{"derivedFrom":[subQ0,sQuery(id+"F0.wireOp",EDGE,"E29")]}),1.0]])],"derivedFrom":subQ0})])],"isStart":false});}
            var Q88;
            {var subQ0=sQuery(id+"F0.wireOp",EDGE,"E6.left");Q88=makeQuery(id+"F1.opExtrude","CAP_EDGE",EDGE,{"disambiguationData":[OSD([subQ0]),TDD([makeQuery(id+"F0.imprint","IMPRINT",EDGE,{"disambiguationData":[TD([[makeQuery(id+"F0.imprint","INTERSECT",VERTEX,{"derivedFrom":[subQ0,sQuery(id+"F0.wireOp",EDGE,"E21")]}),-1.0]])],"derivedFrom":subQ0})])],"isStart":false});}
            var Q89;
            {var subQ0=sQuery(id+"F0.wireOp",EDGE,"E10.left");Q89=makeQuery(id+"F1.opExtrude","CAP_EDGE",EDGE,{"disambiguationData":[OSD([subQ0]),TDD([makeQuery(id+"F0.imprint","IMPRINT",EDGE,{"disambiguationData":[TD([[makeQuery(id+"F0.imprint","INTERSECT",VERTEX,{"derivedFrom":[sQuery(id+"F0.wireOp",EDGE,"E10.top"),subQ0]}),1.0]])],"derivedFrom":subQ0})])],"isStart":false});}
            var Q90;
            {var subQ0=sQuery(id+"F0.wireOp",EDGE,"E14.bottom");Q90=makeQuery(id+"F1.opExtrude","CAP_EDGE",EDGE,{"disambiguationData":[OSD([subQ0]),TDD([makeQuery(id+"F0.imprint","IMPRINT",EDGE,{"disambiguationData":[TD([[makeQuery(id+"F0.imprint","INTERSECT",VERTEX,{"derivedFrom":[subQ0,sQuery(id+"F0.wireOp",EDGE,"E15")]}),-1.0]])],"derivedFrom":subQ0})])],"isStart":false});}
            var Q91;
            {var subQ0=sQuery(id+"F0.wireOp",EDGE,"E10.left");Q91=makeQuery(id+"F1.opExtrude","CAP_EDGE",EDGE,{"disambiguationData":[OSD([subQ0]),TDD([makeQuery(id+"F0.imprint","IMPRINT",EDGE,{"disambiguationData":[TD([[makeQuery(id+"F0.imprint","INTERSECT",VERTEX,{"derivedFrom":[subQ0,sQuery(id+"F0.wireOp",EDGE,"E14.bottom")]}),-1.0]])],"derivedFrom":subQ0})])],"isStart":false});}
            var Q92;
            {var subQ0=sQuery(id+"F0.wireOp",EDGE,"E14.bottom");Q92=makeQuery(id+"F1.opExtrude","CAP_EDGE",EDGE,{"disambiguationData":[OSD([subQ0]),TDD([makeQuery(id+"F0.imprint","IMPRINT",EDGE,{"disambiguationData":[TD([[makeQuery(id+"F0.imprint","INTERSECT",VERTEX,{"derivedFrom":[sQuery(id+"F0.wireOp",EDGE,"E9.right"),subQ0]}),-1.0]])],"derivedFrom":subQ0})])],"isStart":false});}
            var Q93;
            {var subQ0=sQuery(id+"F0.wireOp",EDGE,"E24");Q93=makeQuery(id+"F1.opExtrude","CAP_EDGE",EDGE,{"disambiguationData":[OSD([subQ0]),TDD([makeQuery(id+"F0.imprint","IMPRINT",EDGE,{"disambiguationData":[TD([[makeQuery(id+"F0.imprint","INTERSECT",VERTEX,{"derivedFrom":[sQuery(id+"F0.wireOp",EDGE,"E14.bottom"),subQ0]}),-1.0]])],"derivedFrom":subQ0})])],"isStart":false});}
            var Q94;
            {var subQ0=sQuery(id+"F0.wireOp",EDGE,"E15");Q94=makeQuery(id+"F1.opExtrude","CAP_EDGE",EDGE,{"disambiguationData":[OSD([subQ0]),TDD([makeQuery(id+"F0.imprint","IMPRINT",EDGE,{"disambiguationData":[TD([[makeQuery(id+"F0.imprint","INTERSECT",VERTEX,{"derivedFrom":[sQuery(id+"F0.wireOp",EDGE,"E13.top"),subQ0]}),-1.0]])],"derivedFrom":subQ0})])],"isStart":false});}
            var Q95;
            Q95=makeQuery(id+"F1.opExtrude","SWEPT_EDGE",EDGE,{"disambiguationData":[OSD([sQuery(id+"F0.wireOp",EDGE,"E10.right"),sQuery(id+"F0.wireOp",EDGE,"E14.top")])]});
            var Q96;
            {var subQ0=sQuery(id+"F0.wireOp",EDGE,"E10.right");Q96=makeQuery(id+"F1.opExtrude","CAP_EDGE",EDGE,{"disambiguationData":[OSD([subQ0]),TDD([makeQuery(id+"F0.imprint","IMPRINT",EDGE,{"disambiguationData":[TD([[makeQuery(id+"F0.imprint","INTERSECT",VERTEX,{"derivedFrom":[subQ0,sQuery(id+"F0.wireOp",EDGE,"E14.bottom")]}),-1.0]])],"derivedFrom":subQ0})])],"isStart":false});}
            var Q97;
            {var subQ0=sQuery(id+"F0.wireOp",EDGE,"E13.bottom");Q97=makeQuery(id+"F1.opExtrude","CAP_EDGE",EDGE,{"disambiguationData":[OSD([subQ0]),TDD([makeQuery(id+"F0.imprint","IMPRINT",EDGE,{"disambiguationData":[TD([[makeQuery(id+"F0.imprint","INTERSECT",VERTEX,{"derivedFrom":[sQuery(id+"F0.wireOp",EDGE,"E9.right"),subQ0]}),-1.0]])],"derivedFrom":subQ0})])],"isStart":false});}
            var Q98;
            {var subQ0=sQuery(id+"F0.wireOp",EDGE,"E14.bottom");Q98=makeQuery(id+"F1.opExtrude","CAP_EDGE",EDGE,{"disambiguationData":[OSD([subQ0]),TDD([makeQuery(id+"F0.imprint","IMPRINT",EDGE,{"disambiguationData":[TD([[makeQuery(id+"F0.imprint","INTERSECT",VERTEX,{"derivedFrom":[sQuery(id+"F0.wireOp",EDGE,"E11.left"),subQ0]}),-1.0]])],"derivedFrom":subQ0})])],"isStart":false});}
            var Q99;
            {var subQ0=sQuery(id+"F0.wireOp",EDGE,"E7.right");Q99=makeQuery(id+"F1.opExtrude","CAP_EDGE",EDGE,{"disambiguationData":[OSD([subQ0]),TDD([makeQuery(id+"F0.imprint","IMPRINT",EDGE,{"disambiguationData":[TD([[makeQuery(id+"F0.imprint","INTERSECT",VERTEX,{"derivedFrom":[subQ0,sQuery(id+"F0.wireOp",EDGE,"E22")]}),-1.0]])],"derivedFrom":subQ0})])],"isStart":false});}
            var Q100;
            Q100=makeQuery(id+"F1.opExtrude","CAP_EDGE",EDGE,{"disambiguationData":[OSD([sQuery(id+"F0.wireOp",EDGE,"E32")])],"isStart":false});
            var Q101;
            {var subQ0=sQuery(id+"F0.wireOp",EDGE,"E14.top");Q101=makeQuery(id+"F1.opExtrude","CAP_EDGE",EDGE,{"disambiguationData":[OSD([subQ0]),TDD([makeQuery(id+"F0.imprint","IMPRINT",EDGE,{"disambiguationData":[TD([[makeQuery(id+"F0.imprint","INTERSECT",VERTEX,{"derivedFrom":[subQ0,sQuery(id+"F0.wireOp",EDGE,"E24")]}),1.0]])],"derivedFrom":subQ0})])],"isStart":false});}
            var Q102;
            {var subQ0=sQuery(id+"F0.wireOp",EDGE,"E9.right");Q102=makeQuery(id+"F1.opExtrude","CAP_EDGE",EDGE,{"disambiguationData":[OSD([subQ0]),TDD([makeQuery(id+"F0.imprint","IMPRINT",EDGE,{"disambiguationData":[TD([[makeQuery(id+"F0.imprint","INTERSECT",VERTEX,{"derivedFrom":[subQ0,sQuery(id+"F0.wireOp",EDGE,"E13.bottom")]}),1.0]])],"derivedFrom":subQ0})])],"isStart":false});}
            var Q103;
            {var subQ0=sQuery(id+"F0.wireOp",EDGE,"E9.right");Q103=makeQuery(id+"F1.opExtrude","CAP_EDGE",EDGE,{"disambiguationData":[OSD([subQ0]),TDD([makeQuery(id+"F0.imprint","IMPRINT",EDGE,{"disambiguationData":[TD([[makeQuery(id+"F0.imprint","INTERSECT",VERTEX,{"derivedFrom":[subQ0,sQuery(id+"F0.wireOp",EDGE,"E14.bottom")]}),-1.0]])],"derivedFrom":subQ0})])],"isStart":false});}
            var Q104;
            Q104=makeQuery(id+"F1.opExtrude","SWEPT_EDGE",EDGE,{"disambiguationData":[OSD([sQuery(id+"F0.wireOp",EDGE,"E6.right"),sQuery(id+"F0.wireOp",EDGE,"E13.top")])]});
            var Q105;
            Q105=makeQuery(id+"F1.opExtrude","CAP_EDGE",EDGE,{"disambiguationData":[OSD([sQuery(id+"F0.wireOp",EDGE,"E11.bottom")])],"isStart":false});
            var Q106;
            Q106=makeQuery(id+"F1.opExtrude","CAP_EDGE",EDGE,{"disambiguationData":[OSD([sQuery(id+"F0.wireOp",EDGE,"E18")])],"isStart":false});
            var Q107;
            Q107=makeQuery(id+"F1.opExtrude","SWEPT_EDGE",EDGE,{"disambiguationData":[OSD([sQuery(id+"F0.wireOp",EDGE,"E5.right"),sQuery(id+"F0.wireOp",EDGE,"E14.bottom")])]});
            var Q108;
            {var subQ0=sQuery(id+"F0.wireOp",EDGE,"E24");Q108=makeQuery(id+"F1.opExtrude","CAP_EDGE",EDGE,{"disambiguationData":[OSD([subQ0]),TDD([makeQuery(id+"F0.imprint","IMPRINT",EDGE,{"disambiguationData":[TD([[makeQuery(id+"F0.imprint","INTERSECT",VERTEX,{"derivedFrom":[subQ0,sQuery(id+"F0.wireOp",EDGE,"E26")]}),-1.0]])],"derivedFrom":subQ0})])],"isStart":false});}
            var Q109;
            Q109=makeQuery(id+"F1.opExtrude","CAP_EDGE",EDGE,{"disambiguationData":[OSD([sQuery(id+"F0.wireOp",EDGE,"E10.bottom")])],"isStart":false});
            var Q110;
            {var subQ0=sQuery(id+"F0.wireOp",EDGE,"E1.left");Q110=makeQuery(id+"F1.opExtrude","CAP_EDGE",EDGE,{"disambiguationData":[OSD([subQ0]),TDD([makeQuery(id+"F0.imprint","IMPRINT",EDGE,{"disambiguationData":[TD([[makeQuery(id+"F0.imprint","INTERSECT",VERTEX,{"derivedFrom":[subQ0,sQuery(id+"F0.wireOp",EDGE,"E14.bottom")]}),-1.0]])],"derivedFrom":subQ0})])],"isStart":false});}
            var Q111;
            Q111=makeQuery(id+"F1.opExtrude","SWEPT_EDGE",EDGE,{"disambiguationData":[OSD([sQuery(id+"F0.wireOp",EDGE,"E3.right"),sQuery(id+"F0.wireOp",EDGE,"E13.bottom")])]});
            var Q112;
            {var subQ0=sQuery(id+"F0.wireOp",EDGE,"E13.top");Q112=makeQuery(id+"F1.opExtrude","CAP_EDGE",EDGE,{"disambiguationData":[OSD([subQ0]),TDD([makeQuery(id+"F0.imprint","IMPRINT",EDGE,{"disambiguationData":[TD([[makeQuery(id+"F0.imprint","INTERSECT",VERTEX,{"derivedFrom":[sQuery(id+"F0.wireOp",EDGE,"E2.left"),subQ0]}),1.0]])],"derivedFrom":subQ0})])],"isStart":false});}
            var Q113;
            Q113=makeQuery(id+"F1.opExtrude","CAP_EDGE",EDGE,{"disambiguationData":[OSD([sQuery(id+"F0.wireOp",EDGE,"E25")])],"isStart":false});
            var Q114;
            Q114=makeQuery(id+"F1.opExtrude","CAP_EDGE",EDGE,{"disambiguationData":[OSD([sQuery(id+"F0.wireOp",EDGE,"E26")])],"isStart":false});
            var Q115;
            {var subQ0=sQuery(id+"F0.wireOp",EDGE,"E23");Q115=makeQuery(id+"F1.opExtrude","CAP_EDGE",EDGE,{"disambiguationData":[OSD([subQ0]),TDD([makeQuery(id+"F0.imprint","IMPRINT",EDGE,{"disambiguationData":[TD([[makeQuery(id+"F0.imprint","INTERSECT",VERTEX,{"derivedFrom":[sQuery(id+"F0.wireOp",EDGE,"E14.bottom"),subQ0]}),-1.0]])],"derivedFrom":subQ0})])],"isStart":false});}
            var Q116;
            Q116=makeQuery(id+"F1.opExtrude","CAP_EDGE",EDGE,{"disambiguationData":[OSD([sQuery(id+"F0.wireOp",EDGE,"E19")])],"isStart":false});
            var Q117;
            Q117=makeQuery(id+"F1.opExtrude","CAP_EDGE",EDGE,{"disambiguationData":[OSD([sQuery(id+"F0.wireOp",EDGE,"E10.top")])],"isStart":false});
            var Q118;
            {var subQ0=sQuery(id+"F0.wireOp",EDGE,"E13.bottom");Q118=makeQuery(id+"F1.opExtrude","CAP_EDGE",EDGE,{"disambiguationData":[OSD([subQ0]),TDD([makeQuery(id+"F0.imprint","IMPRINT",EDGE,{"disambiguationData":[TD([[makeQuery(id+"F0.imprint","INTERSECT",VERTEX,{"derivedFrom":[sQuery(id+"F0.wireOp",EDGE,"E3.right"),subQ0]}),1.0]])],"derivedFrom":subQ0})])],"isStart":false});}
            var Q119;
            {var subQ0=sQuery(id+"F0.wireOp",EDGE,"E2.left");Q119=makeQuery(id+"F1.opExtrude","CAP_EDGE",EDGE,{"disambiguationData":[OSD([subQ0]),TDD([makeQuery(id+"F0.imprint","IMPRINT",EDGE,{"disambiguationData":[TD([[makeQuery(id+"F0.imprint","INTERSECT",VERTEX,{"derivedFrom":[subQ0,sQuery(id+"F0.wireOp",EDGE,"E18")]}),-1.0]])],"derivedFrom":subQ0})])],"isStart":false});}
            var Q120;
            {var subQ0=sQuery(id+"F0.wireOp",EDGE,"E13.top");Q120=makeQuery(id+"F1.opExtrude","CAP_EDGE",EDGE,{"disambiguationData":[OSD([subQ0]),TDD([makeQuery(id+"F0.imprint","IMPRINT",EDGE,{"disambiguationData":[TD([[makeQuery(id+"F0.imprint","INTERSECT",VERTEX,{"derivedFrom":[sQuery(id+"F0.wireOp",EDGE,"E11.left"),subQ0]}),-1.0]])],"derivedFrom":subQ0})])],"isStart":false});}
            var Q121;
            {var subQ0=sQuery(id+"F0.wireOp",EDGE,"E13.bottom");Q121=makeQuery(id+"F1.opExtrude","CAP_EDGE",EDGE,{"disambiguationData":[OSD([subQ0]),TDD([makeQuery(id+"F0.imprint","IMPRINT",EDGE,{"disambiguationData":[TD([[makeQuery(id+"F0.imprint","INTERSECT",VERTEX,{"derivedFrom":[sQuery(id+"F0.wireOp",EDGE,"E1.right"),subQ0]}),1.0]])],"derivedFrom":subQ0})])],"isStart":false});}
            var Q122;
            {var subQ0=sQuery(id+"F0.wireOp",EDGE,"E13.top");Q122=makeQuery(id+"F1.opExtrude","CAP_EDGE",EDGE,{"disambiguationData":[OSD([subQ0]),TDD([makeQuery(id+"F0.imprint","IMPRINT",EDGE,{"disambiguationData":[TD([[makeQuery(id+"F0.imprint","INTERSECT",VERTEX,{"derivedFrom":[sQuery(id+"F0.wireOp",EDGE,"E1.right"),subQ0]}),1.0]])],"derivedFrom":subQ0})])],"isStart":false});}
            var Q123;
            Q123=makeQuery(id+"F1.opExtrude","CAP_EDGE",EDGE,{"disambiguationData":[OSD([sQuery(id+"F0.wireOp",EDGE,"E11.top")])],"isStart":false});
            var Q124;
            {var subQ0=sQuery(id+"F0.wireOp",EDGE,"E13.top");Q124=makeQuery(id+"F1.opExtrude","CAP_EDGE",EDGE,{"disambiguationData":[OSD([subQ0]),TDD([makeQuery(id+"F0.imprint","IMPRINT",EDGE,{"disambiguationData":[TD([[makeQuery(id+"F0.imprint","INTERSECT",VERTEX,{"derivedFrom":[sQuery(id+"F0.wireOp",EDGE,"E2.right"),subQ0]}),-1.0]])],"derivedFrom":subQ0})])],"isStart":false});}
            var Q125;
            {var subQ0=sQuery(id+"F0.wireOp",EDGE,"E10.right");Q125=makeQuery(id+"F1.opExtrude","CAP_EDGE",EDGE,{"disambiguationData":[OSD([subQ0]),TDD([makeQuery(id+"F0.imprint","IMPRINT",EDGE,{"disambiguationData":[TD([[makeQuery(id+"F0.imprint","INTERSECT",VERTEX,{"derivedFrom":[sQuery(id+"F0.wireOp",EDGE,"E10.top"),subQ0]}),1.0]])],"derivedFrom":subQ0})])],"isStart":false});}
            var Q126;
            {var subQ0=sQuery(id+"F0.wireOp",EDGE,"E14.top");Q126=makeQuery(id+"F1.opExtrude","CAP_EDGE",EDGE,{"disambiguationData":[OSD([subQ0]),TDD([makeQuery(id+"F0.imprint","IMPRINT",EDGE,{"disambiguationData":[TD([[makeQuery(id+"F0.imprint","INTERSECT",VERTEX,{"derivedFrom":[sQuery(id+"F0.wireOp",EDGE,"E11.left"),subQ0]}),-1.0]])],"derivedFrom":subQ0})])],"isStart":false});}
            var Q127;
            {var subQ0=sQuery(id+"F0.wireOp",EDGE,"E3.right");Q127=makeQuery(id+"F1.opExtrude","CAP_EDGE",EDGE,{"disambiguationData":[OSD([subQ0]),TDD([makeQuery(id+"F0.imprint","IMPRINT",EDGE,{"disambiguationData":[TD([[makeQuery(id+"F0.imprint","INTERSECT",VERTEX,{"derivedFrom":[subQ0,sQuery(id+"F0.wireOp",EDGE,"E13.bottom")]}),-1.0]])],"derivedFrom":subQ0})])],"isStart":false});}
            var Q128;
            {var subQ0=sQuery(id+"F0.wireOp",EDGE,"E7.right");Q128=makeQuery(id+"F1.opExtrude","CAP_EDGE",EDGE,{"disambiguationData":[OSD([subQ0]),TDD([makeQuery(id+"F0.imprint","IMPRINT",EDGE,{"disambiguationData":[TD([[makeQuery(id+"F0.imprint","INTERSECT",VERTEX,{"derivedFrom":[subQ0,sQuery(id+"F0.wireOp",EDGE,"E14.bottom")]}),-1.0]])],"derivedFrom":subQ0})])],"isStart":false});}
            var Q129;
            Q129=makeQuery(id+"F1.opExtrude","CAP_EDGE",EDGE,{"disambiguationData":[OSD([sQuery(id+"F0.wireOp",EDGE,"E30")])],"isStart":false});
            var Q130;
            {var subQ0=sQuery(id+"F0.wireOp",EDGE,"E14.top");Q130=makeQuery(id+"F1.opExtrude","CAP_EDGE",EDGE,{"disambiguationData":[OSD([subQ0]),TDD([makeQuery(id+"F0.imprint","IMPRINT",EDGE,{"disambiguationData":[TD([[makeQuery(id+"F0.imprint","INTERSECT",VERTEX,{"derivedFrom":[sQuery(id+"F0.wireOp",EDGE,"E7.right"),subQ0]}),-1.0]])],"derivedFrom":subQ0})])],"isStart":false});}
            var Q131;
            {var subQ0=sQuery(id+"F0.wireOp",EDGE,"E13.top");Q131=makeQuery(id+"F1.opExtrude","CAP_EDGE",EDGE,{"disambiguationData":[OSD([subQ0]),TDD([makeQuery(id+"F0.imprint","IMPRINT",EDGE,{"disambiguationData":[TD([[makeQuery(id+"F0.imprint","INTERSECT",VERTEX,{"derivedFrom":[sQuery(id+"F0.wireOp",EDGE,"E10.left"),subQ0]}),-1.0]])],"derivedFrom":subQ0})])],"isStart":true});}
            var Q132;
            {var subQ0=sQuery(id+"F0.wireOp",EDGE,"E5.right");Q132=makeQuery(id+"F1.opExtrude","CAP_EDGE",EDGE,{"disambiguationData":[OSD([subQ0]),TDD([makeQuery(id+"F0.imprint","IMPRINT",EDGE,{"disambiguationData":[TD([[makeQuery(id+"F0.imprint","INTERSECT",VERTEX,{"derivedFrom":[subQ0,sQuery(id+"F0.wireOp",EDGE,"E13.top")]}),-1.0]])],"derivedFrom":subQ0})])],"isStart":true});}
            var Q133;
            {var subQ0=sQuery(id+"F0.wireOp",EDGE,"E6.left");Q133=makeQuery(id+"F1.opExtrude","CAP_EDGE",EDGE,{"disambiguationData":[OSD([subQ0]),TDD([makeQuery(id+"F0.imprint","IMPRINT",EDGE,{"disambiguationData":[TD([[makeQuery(id+"F0.imprint","INTERSECT",VERTEX,{"derivedFrom":[sQuery(id+"F0.wireOp",EDGE,"E6.top"),subQ0]}),1.0]])],"derivedFrom":subQ0})])],"isStart":true});}
            var Q134;
            Q134=makeQuery(id+"F1.opExtrude","SWEPT_EDGE",EDGE,{"disambiguationData":[OSD([sQuery(id+"F0.wireOp",EDGE,"E11.left"),sQuery(id+"F0.wireOp",EDGE,"E13.bottom")])]});
            var Q135;
            Q135=makeQuery(id+"F1.opExtrude","SWEPT_EDGE",EDGE,{"disambiguationData":[OSD([sQuery(id+"F0.wireOp",EDGE,"E1.left"),sQuery(id+"F0.wireOp",EDGE,"E13.top")])]});
            var Q136;
            Q136=makeQuery(id+"F1.opExtrude","SWEPT_EDGE",EDGE,{"disambiguationData":[OSD([sQuery(id+"F0.wireOp",EDGE,"E3.right"),sQuery(id+"F0.wireOp",EDGE,"E19")])]});
            var Q137;
            Q137=makeQuery(id+"F1.opExtrude","SWEPT_EDGE",EDGE,{"disambiguationData":[OSD([sQuery(id+"F0.wireOp",EDGE,"E11.left"),sQuery(id+"F0.wireOp",EDGE,"E14.bottom")])]});
            var Q138;
            Q138=makeQuery(id+"F1.opExtrude","SWEPT_EDGE",EDGE,{"disambiguationData":[OSD([sQuery(id+"F0.wireOp",EDGE,"E7.right"),sQuery(id+"F0.wireOp",EDGE,"E32")])]});
            var Q139;
            Q139=makeQuery(id+"F1.opExtrude","CAP_EDGE",EDGE,{"disambiguationData":[OSD([sQuery(id+"F0.wireOp",EDGE,"E17")])],"isStart":true});
            var Q140;
            {var subQ0=sQuery(id+"F0.wireOp",EDGE,"E2.right");Q140=makeQuery(id+"F1.opExtrude","CAP_EDGE",EDGE,{"disambiguationData":[OSD([subQ0]),TDD([makeQuery(id+"F0.imprint","IMPRINT",EDGE,{"disambiguationData":[TD([[makeQuery(id+"F0.imprint","INTERSECT",VERTEX,{"derivedFrom":[subQ0,sQuery(id+"F0.wireOp",EDGE,"E19")]}),-1.0]])],"derivedFrom":subQ0})])],"isStart":true});}
            var Q141;
            Q141=makeQuery(id+"F1.opExtrude","SWEPT_EDGE",EDGE,{"disambiguationData":[OSD([sQuery(id+"F0.wireOp",EDGE,"E1.right"),sQuery(id+"F0.wireOp",EDGE,"E14.top")])]});
            var Q142;
            Q142=makeQuery(id+"F1.opExtrude","SWEPT_EDGE",EDGE,{"disambiguationData":[OSD([sQuery(id+"F0.wireOp",EDGE,"E5.right"),sQuery(id+"F0.wireOp",EDGE,"E28")])]});
            var Q143;
            Q143=makeQuery(id+"F1.opExtrude","CAP_EDGE",EDGE,{"disambiguationData":[OSD([sQuery(id+"F0.wireOp",EDGE,"E18")])],"isStart":true});
            var Q144;
            {var subQ0=sQuery(id+"F0.wireOp",EDGE,"E13.bottom");Q144=makeQuery(id+"F1.opExtrude","CAP_EDGE",EDGE,{"disambiguationData":[OSD([subQ0]),TDD([makeQuery(id+"F0.imprint","IMPRINT",EDGE,{"disambiguationData":[TD([[makeQuery(id+"F0.imprint","INTERSECT",VERTEX,{"derivedFrom":[sQuery(id+"F0.wireOp",EDGE,"E9.right"),subQ0]}),-1.0]])],"derivedFrom":subQ0})])],"isStart":true});}
            var Q145;
            Q145=makeQuery(id+"F1.opExtrude","SWEPT_EDGE",EDGE,{"disambiguationData":[OSD([sQuery(id+"F0.wireOp",EDGE,"E6.left"),sQuery(id+"F0.wireOp",EDGE,"E14.top")])]});
            var Q146;
            Q146=makeQuery(id+"F1.opExtrude","SWEPT_EDGE",EDGE,{"disambiguationData":[OSD([sQuery(id+"F0.wireOp",EDGE,"E8.left"),sQuery(id+"F0.wireOp",EDGE,"E14.bottom")])]});
            var Q147;
            Q147=makeQuery(id+"F1.opExtrude","SWEPT_EDGE",EDGE,{"disambiguationData":[OSD([sQuery(id+"F0.wireOp",EDGE,"E2.right"),sQuery(id+"F0.wireOp",EDGE,"E13.top")])]});
            var Q148;
            {var subQ0=sQuery(id+"F0.wireOp",EDGE,"E14.bottom");Q148=makeQuery(id+"F1.opExtrude","CAP_EDGE",EDGE,{"disambiguationData":[OSD([subQ0]),TDD([makeQuery(id+"F0.imprint","IMPRINT",EDGE,{"disambiguationData":[TD([[makeQuery(id+"F0.imprint","INTERSECT",VERTEX,{"derivedFrom":[sQuery(id+"F0.wireOp",EDGE,"E2.right"),subQ0]}),-1.0]])],"derivedFrom":subQ0})])],"isStart":true});}
            var Q149;
            {var subQ0=sQuery(id+"F0.wireOp",EDGE,"E14.bottom");Q149=makeQuery(id+"F1.opExtrude","CAP_EDGE",EDGE,{"disambiguationData":[OSD([subQ0]),TDD([makeQuery(id+"F0.imprint","IMPRINT",EDGE,{"disambiguationData":[TD([[makeQuery(id+"F0.imprint","INTERSECT",VERTEX,{"derivedFrom":[subQ0,sQuery(id+"F0.wireOp",EDGE,"E15")]}),-1.0]])],"derivedFrom":subQ0})])],"isStart":true});}
            var Q150;
            {var subQ0=sQuery(id+"F0.wireOp",EDGE,"E14.top");Q150=makeQuery(id+"F1.opExtrude","CAP_EDGE",EDGE,{"disambiguationData":[OSD([subQ0]),TDD([makeQuery(id+"F0.imprint","IMPRINT",EDGE,{"disambiguationData":[TD([[makeQuery(id+"F0.imprint","INTERSECT",VERTEX,{"derivedFrom":[subQ0,sQuery(id+"F0.wireOp",EDGE,"E24")]}),1.0]])],"derivedFrom":subQ0})])],"isStart":true});}
            var Q151;
            {var subQ0=sQuery(id+"F0.wireOp",EDGE,"E14.bottom");Q151=makeQuery(id+"F1.opExtrude","CAP_EDGE",EDGE,{"disambiguationData":[OSD([subQ0]),TDD([makeQuery(id+"F0.imprint","IMPRINT",EDGE,{"disambiguationData":[TD([[makeQuery(id+"F0.imprint","INTERSECT",VERTEX,{"derivedFrom":[sQuery(id+"F0.wireOp",EDGE,"E10.left"),subQ0]}),-1.0]])],"derivedFrom":subQ0})])],"isStart":true});}
            var Q152;
            Q152=makeQuery(id+"F1.opExtrude","SWEPT_EDGE",EDGE,{"disambiguationData":[OSD([sQuery(id+"F0.wireOp",EDGE,"E13.bottom"),sQuery(id+"F0.wireOp",EDGE,"E23")])]});
            var Q153;
            Q153=makeQuery(id+"F1.opExtrude","CAP_EDGE",EDGE,{"disambiguationData":[OSD([sQuery(id+"F0.wireOp",EDGE,"E32")])],"isStart":true});
            var Q154;
            Q154=makeQuery(id+"F1.opExtrude","SWEPT_EDGE",EDGE,{"disambiguationData":[OSD([sQuery(id+"F0.wireOp",EDGE,"E3.bottom"),sQuery(id+"F0.wireOp",EDGE,"E3.right")])]});
            var Q155;
            {var subQ0=sQuery(id+"F0.wireOp",EDGE,"E13.top");Q155=makeQuery(id+"F1.opExtrude","CAP_EDGE",EDGE,{"disambiguationData":[OSD([subQ0]),TDD([makeQuery(id+"F0.imprint","IMPRINT",EDGE,{"disambiguationData":[TD([[makeQuery(id+"F0.imprint","INTERSECT",VERTEX,{"derivedFrom":[sQuery(id+"F0.wireOp",EDGE,"E1.right"),subQ0]}),1.0]])],"derivedFrom":subQ0})])],"isStart":true});}
            var Q156;
            {var subQ0=sQuery(id+"F0.wireOp",EDGE,"E23");Q156=makeQuery(id+"F1.opExtrude","CAP_EDGE",EDGE,{"disambiguationData":[OSD([subQ0]),TDD([makeQuery(id+"F0.imprint","IMPRINT",EDGE,{"disambiguationData":[TD([[makeQuery(id+"F0.imprint","INTERSECT",VERTEX,{"derivedFrom":[sQuery(id+"F0.wireOp",EDGE,"E14.bottom"),subQ0]}),-1.0]])],"derivedFrom":subQ0})])],"isStart":true});}
            var Q157;
            Q157=makeQuery(id+"F1.opExtrude","CAP_EDGE",EDGE,{"disambiguationData":[OSD([sQuery(id+"F0.wireOp",EDGE,"E10.top")])],"isStart":true});
            var Q158;
            Q158=makeQuery(id+"F1.opExtrude","CAP_EDGE",EDGE,{"disambiguationData":[OSD([sQuery(id+"F0.wireOp",EDGE,"E19")])],"isStart":true});
            var Q159;
            Q159=makeQuery(id+"F1.opExtrude","SWEPT_EDGE",EDGE,{"disambiguationData":[OSD([sQuery(id+"F0.wireOp",EDGE,"E11.bottom"),sQuery(id+"F0.wireOp",EDGE,"E11.right")])]});
            var Q160;
            Q160=makeQuery(id+"F1.opExtrude","SWEPT_EDGE",EDGE,{"disambiguationData":[OSD([sQuery(id+"F0.wireOp",EDGE,"E11.right"),sQuery(id+"F0.wireOp",EDGE,"E13.top")])]});
            var Q161;
            Q161=makeQuery(id+"F1.opExtrude","SWEPT_EDGE",EDGE,{"disambiguationData":[OSD([sQuery(id+"F0.wireOp",EDGE,"E10.right"),sQuery(id+"F0.wireOp",EDGE,"E13.top")])]});
            var Q162;
            {var subQ0=sQuery(id+"F0.wireOp",EDGE,"E9.right");Q162=makeQuery(id+"F1.opExtrude","CAP_EDGE",EDGE,{"disambiguationData":[OSD([subQ0]),TDD([makeQuery(id+"F0.imprint","IMPRINT",EDGE,{"disambiguationData":[TD([[makeQuery(id+"F0.imprint","INTERSECT",VERTEX,{"derivedFrom":[subQ0,sQuery(id+"F0.wireOp",EDGE,"E14.bottom")]}),-1.0]])],"derivedFrom":subQ0})])],"isStart":true});}
            var Q163;
            {var subQ0=sQuery(id+"F0.wireOp",EDGE,"E6.left");Q163=makeQuery(id+"F1.opExtrude","CAP_EDGE",EDGE,{"disambiguationData":[OSD([subQ0]),TDD([makeQuery(id+"F0.imprint","IMPRINT",EDGE,{"disambiguationData":[TD([[makeQuery(id+"F0.imprint","INTERSECT",VERTEX,{"derivedFrom":[subQ0,sQuery(id+"F0.wireOp",EDGE,"E14.bottom")]}),-1.0]])],"derivedFrom":subQ0})])],"isStart":true});}
            var Q164;
            {var subQ0=sQuery(id+"F0.wireOp",EDGE,"E14.bottom");Q164=makeQuery(id+"F1.opExtrude","CAP_EDGE",EDGE,{"disambiguationData":[OSD([subQ0]),TDD([makeQuery(id+"F0.imprint","IMPRINT",EDGE,{"disambiguationData":[TD([[makeQuery(id+"F0.imprint","INTERSECT",VERTEX,{"derivedFrom":[sQuery(id+"F0.wireOp",EDGE,"E11.left"),subQ0]}),-1.0]])],"derivedFrom":subQ0})])],"isStart":true});}
            var Q165;
            Q165=makeQuery(id+"F1.opExtrude","SWEPT_EDGE",EDGE,{"disambiguationData":[OSD([sQuery(id+"F0.wireOp",EDGE,"E13.top"),sQuery(id+"F0.wireOp",EDGE,"E24")])]});
            var Q166;
            Q166=makeQuery(id+"F1.opExtrude","SWEPT_EDGE",EDGE,{"disambiguationData":[OSD([sQuery(id+"F0.wireOp",EDGE,"E14.bottom"),sQuery(id+"F0.wireOp",EDGE,"E16")])]});
            var Q167;
            Q167=makeQuery(id+"F1.opExtrude","SWEPT_EDGE",EDGE,{"disambiguationData":[OSD([sQuery(id+"F0.wireOp",EDGE,"E11.left"),sQuery(id+"F0.wireOp",EDGE,"E13.top")])]});
            var Q168;
            Q168=makeQuery(id+"F1.opExtrude","SWEPT_EDGE",EDGE,{"disambiguationData":[OSD([sQuery(id+"F0.wireOp",EDGE,"E11.left"),sQuery(id+"F0.wireOp",EDGE,"E14.top")])]});
            var Q169;
            Q169=makeQuery(id+"F1.opExtrude","SWEPT_EDGE",EDGE,{"disambiguationData":[OSD([sQuery(id+"F0.wireOp",EDGE,"E11.right"),sQuery(id+"F0.wireOp",EDGE,"E14.bottom")])]});
            var Q170;
            {var subQ0=sQuery(id+"F0.wireOp",EDGE,"E7.right");Q170=makeQuery(id+"F1.opExtrude","CAP_EDGE",EDGE,{"disambiguationData":[OSD([subQ0]),TDD([makeQuery(id+"F0.imprint","IMPRINT",EDGE,{"disambiguationData":[TD([[makeQuery(id+"F0.imprint","INTERSECT",VERTEX,{"derivedFrom":[subQ0,sQuery(id+"F0.wireOp",EDGE,"E14.bottom")]}),-1.0]])],"derivedFrom":subQ0})])],"isStart":true});}
            var Q171;
            {var subQ0=sQuery(id+"F0.wireOp",EDGE,"E2.right");Q171=makeQuery(id+"F1.opExtrude","CAP_EDGE",EDGE,{"disambiguationData":[OSD([subQ0]),TDD([makeQuery(id+"F0.imprint","IMPRINT",EDGE,{"disambiguationData":[TD([[makeQuery(id+"F0.imprint","INTERSECT",VERTEX,{"derivedFrom":[subQ0,sQuery(id+"F0.wireOp",EDGE,"E3.bottom")]}),1.0]])],"derivedFrom":subQ0})])],"isStart":true});}
            var Q172;
            Q172=makeQuery(id+"F1.opExtrude","SWEPT_EDGE",EDGE,{"disambiguationData":[OSD([sQuery(id+"F0.wireOp",EDGE,"E6.right"),sQuery(id+"F0.wireOp",EDGE,"E13.bottom")])]});
            var Q173;
            Q173=makeQuery(id+"F1.opExtrude","CAP_EDGE",EDGE,{"disambiguationData":[OSD([sQuery(id+"F0.wireOp",EDGE,"E10.bottom")])],"isStart":true});
            var Q174;
            {var subQ0=sQuery(id+"F0.wireOp",EDGE,"E1.left");Q174=makeQuery(id+"F1.opExtrude","CAP_EDGE",EDGE,{"disambiguationData":[OSD([subQ0]),TDD([makeQuery(id+"F0.imprint","IMPRINT",EDGE,{"disambiguationData":[TD([[makeQuery(id+"F0.imprint","INTERSECT",VERTEX,{"derivedFrom":[subQ0,sQuery(id+"F0.wireOp",EDGE,"E13.bottom")]}),1.0]])],"derivedFrom":subQ0})])],"isStart":true});}
            var Q175;
            Q175=makeQuery(id+"F1.opExtrude","SWEPT_EDGE",EDGE,{"disambiguationData":[OSD([sQuery(id+"F0.wireOp",EDGE,"E6.right"),sQuery(id+"F0.wireOp",EDGE,"E21")])]});
            var Q176;
            {var subQ0=sQuery(id+"F0.wireOp",EDGE,"E15");Q176=makeQuery(id+"F1.opExtrude","CAP_EDGE",EDGE,{"disambiguationData":[OSD([subQ0]),TDD([makeQuery(id+"F0.imprint","IMPRINT",EDGE,{"disambiguationData":[TD([[makeQuery(id+"F0.imprint","INTERSECT",VERTEX,{"derivedFrom":[sQuery(id+"F0.wireOp",EDGE,"E14.bottom"),subQ0]}),-1.0]])],"derivedFrom":subQ0})])],"isStart":true});}
            var Q177;
            Q177=makeQuery(id+"F1.opExtrude","SWEPT_EDGE",EDGE,{"disambiguationData":[OSD([sQuery(id+"F0.wireOp",EDGE,"E7.right"),sQuery(id+"F0.wireOp",EDGE,"E14.top")])]});
            var Q178;
            Q178=makeQuery(id+"F1.opExtrude","SWEPT_EDGE",EDGE,{"disambiguationData":[OSD([sQuery(id+"F0.wireOp",EDGE,"E14.bottom"),sQuery(id+"F0.wireOp",EDGE,"E15")])]});
            var Q179;
            Q179=makeQuery(id+"F1.opExtrude","SWEPT_EDGE",EDGE,{"disambiguationData":[OSD([sQuery(id+"F0.wireOp",EDGE,"E2.left"),sQuery(id+"F0.wireOp",EDGE,"E18")])]});
            var Q180;
            {var subQ0=sQuery(id+"F0.wireOp",EDGE,"E14.top");Q180=makeQuery(id+"F1.opExtrude","CAP_EDGE",EDGE,{"disambiguationData":[OSD([subQ0]),TDD([makeQuery(id+"F0.imprint","IMPRINT",EDGE,{"disambiguationData":[TD([[makeQuery(id+"F0.imprint","INTERSECT",VERTEX,{"derivedFrom":[sQuery(id+"F0.wireOp",EDGE,"E6.left"),subQ0]}),-1.0]])],"derivedFrom":subQ0})])],"isStart":true});}
            var Q181;
            Q181=makeQuery(id+"F1.opExtrude","SWEPT_EDGE",EDGE,{"disambiguationData":[OSD([sQuery(id+"F0.wireOp",EDGE,"E4.right"),sQuery(id+"F0.wireOp",EDGE,"E28")])]});
            var Q182;
            Q182=makeQuery(id+"F1.opExtrude","CAP_EDGE",EDGE,{"disambiguationData":[OSD([sQuery(id+"F0.wireOp",EDGE,"E31")])],"isStart":true});
            var Q183;
            Q183=makeQuery(id+"F1.opExtrude","SWEPT_EDGE",EDGE,{"disambiguationData":[OSD([sQuery(id+"F0.wireOp",EDGE,"E10.left"),sQuery(id+"F0.wireOp",EDGE,"E13.bottom")])]});
            var Q184;
            {var subQ0=sQuery(id+"F0.wireOp",EDGE,"E11.left");Q184=makeQuery(id+"F1.opExtrude","CAP_EDGE",EDGE,{"disambiguationData":[OSD([subQ0]),TDD([makeQuery(id+"F0.imprint","IMPRINT",EDGE,{"disambiguationData":[TD([[makeQuery(id+"F0.imprint","INTERSECT",VERTEX,{"derivedFrom":[sQuery(id+"F0.wireOp",EDGE,"E11.bottom"),subQ0]}),-1.0]])],"derivedFrom":subQ0})])],"isStart":true});}
            var Q185;
            Q185=makeQuery(id+"F1.opExtrude","SWEPT_EDGE",EDGE,{"disambiguationData":[OSD([sQuery(id+"F0.wireOp",EDGE,"E2.left"),sQuery(id+"F0.wireOp",EDGE,"E13.top")])]});
            var Q186;
            {var subQ0=sQuery(id+"F0.wireOp",EDGE,"E2.left");Q186=makeQuery(id+"F1.opExtrude","CAP_EDGE",EDGE,{"disambiguationData":[OSD([subQ0]),TDD([makeQuery(id+"F0.imprint","IMPRINT",EDGE,{"disambiguationData":[TD([[makeQuery(id+"F0.imprint","INTERSECT",VERTEX,{"derivedFrom":[subQ0,sQuery(id+"F0.wireOp",EDGE,"E14.bottom")]}),-1.0]])],"derivedFrom":subQ0})])],"isStart":true});}
            var Q187;
            Q187=makeQuery(id+"F1.opExtrude","SWEPT_EDGE",EDGE,{"disambiguationData":[OSD([sQuery(id+"F0.wireOp",EDGE,"E11.right"),sQuery(id+"F0.wireOp",EDGE,"E14.top")])]});
            var Q188;
            {var subQ0=sQuery(id+"F0.wireOp",EDGE,"E10.left");Q188=makeQuery(id+"F1.opExtrude","CAP_EDGE",EDGE,{"disambiguationData":[OSD([subQ0]),TDD([makeQuery(id+"F0.imprint","IMPRINT",EDGE,{"disambiguationData":[TD([[makeQuery(id+"F0.imprint","INTERSECT",VERTEX,{"derivedFrom":[sQuery(id+"F0.wireOp",EDGE,"E10.top"),subQ0]}),1.0]])],"derivedFrom":subQ0})])],"isStart":true});}
            var Q189;
            Q189=makeQuery(id+"F1.opExtrude","SWEPT_EDGE",EDGE,{"disambiguationData":[OSD([sQuery(id+"F0.wireOp",EDGE,"E5.right"),sQuery(id+"F0.wireOp",EDGE,"E13.bottom")])]});
            var Q190;
            Q190=makeQuery(id+"F1.opExtrude","SWEPT_EDGE",EDGE,{"disambiguationData":[OSD([sQuery(id+"F0.wireOp",EDGE,"E10.left"),sQuery(id+"F0.wireOp",EDGE,"E13.top")])]});
            var Q191;
            {var subQ0=sQuery(id+"F0.wireOp",EDGE,"E14.bottom");Q191=makeQuery(id+"F1.opExtrude","CAP_EDGE",EDGE,{"disambiguationData":[OSD([subQ0]),TDD([makeQuery(id+"F0.imprint","IMPRINT",EDGE,{"disambiguationData":[TD([[makeQuery(id+"F0.imprint","INTERSECT",VERTEX,{"derivedFrom":[sQuery(id+"F0.wireOp",EDGE,"E1.right"),subQ0]}),1.0]])],"derivedFrom":subQ0})])],"isStart":false});}
            var Q192;
            {var subQ0=sQuery(id+"F0.wireOp",EDGE,"E13.top");Q192=makeQuery(id+"F1.opExtrude","CAP_EDGE",EDGE,{"disambiguationData":[OSD([subQ0]),TDD([makeQuery(id+"F0.imprint","IMPRINT",EDGE,{"disambiguationData":[TD([[makeQuery(id+"F0.imprint","INTERSECT",VERTEX,{"derivedFrom":[sQuery(id+"F0.wireOp",EDGE,"E5.right"),subQ0]}),1.0]])],"derivedFrom":subQ0})])],"isStart":true});}
            var Q193;
            {var subQ0=sQuery(id+"F0.wireOp",EDGE,"E8.left");Q193=makeQuery(id+"F1.opExtrude","CAP_EDGE",EDGE,{"disambiguationData":[OSD([subQ0]),TDD([makeQuery(id+"F0.imprint","IMPRINT",EDGE,{"disambiguationData":[TD([[makeQuery(id+"F0.imprint","INTERSECT",VERTEX,{"derivedFrom":[subQ0,sQuery(id+"F0.wireOp",EDGE,"E14.bottom")]}),-1.0]])],"derivedFrom":subQ0})])],"isStart":true});}
            var Q194;
            Q194=makeQuery(id+"F1.opExtrude","SWEPT_EDGE",EDGE,{"disambiguationData":[OSD([sQuery(id+"F0.wireOp",EDGE,"E8.left"),sQuery(id+"F0.wireOp",EDGE,"E13.top")])]});
            var Q195;
            {var subQ0=sQuery(id+"F0.wireOp",EDGE,"E14.bottom");Q195=makeQuery(id+"F1.opExtrude","CAP_EDGE",EDGE,{"disambiguationData":[OSD([subQ0]),TDD([makeQuery(id+"F0.imprint","IMPRINT",EDGE,{"disambiguationData":[TD([[makeQuery(id+"F0.imprint","INTERSECT",VERTEX,{"derivedFrom":[sQuery(id+"F0.wireOp",EDGE,"E1.left"),subQ0]}),-1.0]])],"derivedFrom":subQ0})])],"isStart":true});}
            var Q196;
            Q196=makeQuery(id+"F1.opExtrude","SWEPT_EDGE",EDGE,{"disambiguationData":[OSD([sQuery(id+"F0.wireOp",EDGE,"E2.right"),sQuery(id+"F0.wireOp",EDGE,"E3.bottom")])]});
            var Q197;
            {var subQ0=sQuery(id+"F0.wireOp",EDGE,"E6.right");Q197=makeQuery(id+"F1.opExtrude","CAP_EDGE",EDGE,{"disambiguationData":[OSD([subQ0]),TDD([makeQuery(id+"F0.imprint","IMPRINT",EDGE,{"disambiguationData":[TD([[makeQuery(id+"F0.imprint","INTERSECT",VERTEX,{"derivedFrom":[sQuery(id+"F0.wireOp",EDGE,"E6.top"),subQ0]}),1.0]])],"derivedFrom":subQ0})])],"isStart":true});}
            var Q198;
            {var subQ0=sQuery(id+"F0.wireOp",EDGE,"E3.right");Q198=makeQuery(id+"F1.opExtrude","CAP_EDGE",EDGE,{"disambiguationData":[OSD([subQ0]),TDD([makeQuery(id+"F0.imprint","IMPRINT",EDGE,{"disambiguationData":[TD([[makeQuery(id+"F0.imprint","INTERSECT",VERTEX,{"derivedFrom":[subQ0,sQuery(id+"F0.wireOp",EDGE,"E14.top")]}),-1.0]])],"derivedFrom":subQ0})])],"isStart":true});}
            var Q199;
            {var subQ0=sQuery(id+"F0.wireOp",EDGE,"E2.left");Q199=makeQuery(id+"F1.opExtrude","CAP_EDGE",EDGE,{"disambiguationData":[OSD([subQ0]),TDD([makeQuery(id+"F0.imprint","IMPRINT",EDGE,{"disambiguationData":[TD([[makeQuery(id+"F0.imprint","INTERSECT",VERTEX,{"derivedFrom":[subQ0,sQuery(id+"F0.wireOp",EDGE,"E18")]}),-1.0]])],"derivedFrom":subQ0})])],"isStart":true});}
            var Q200;
            Q200=makeQuery(id+"F1.opExtrude","SWEPT_EDGE",EDGE,{"disambiguationData":[OSD([sQuery(id+"F0.wireOp",EDGE,"E2.right"),sQuery(id+"F0.wireOp",EDGE,"E14.top")])]});
            var Q201;
            Q201=makeQuery(id+"F1.opExtrude","SWEPT_EDGE",EDGE,{"disambiguationData":[OSD([sQuery(id+"F0.wireOp",EDGE,"E1.right"),sQuery(id+"F0.wireOp",EDGE,"E13.top")])]});
            var Q202;
            {var subQ0=sQuery(id+"F0.wireOp",EDGE,"E24");Q202=makeQuery(id+"F1.opExtrude","CAP_EDGE",EDGE,{"disambiguationData":[OSD([subQ0]),TDD([makeQuery(id+"F0.imprint","IMPRINT",EDGE,{"disambiguationData":[TD([[makeQuery(id+"F0.imprint","INTERSECT",VERTEX,{"derivedFrom":[subQ0,sQuery(id+"F0.wireOp",EDGE,"E26")]}),-1.0]])],"derivedFrom":subQ0})])],"isStart":true});}
            var Q203;
            {var subQ0=sQuery(id+"F0.wireOp",EDGE,"E13.bottom");Q203=makeQuery(id+"F1.opExtrude","CAP_EDGE",EDGE,{"disambiguationData":[OSD([subQ0]),TDD([makeQuery(id+"F0.imprint","IMPRINT",EDGE,{"disambiguationData":[TD([[makeQuery(id+"F0.imprint","INTERSECT",VERTEX,{"derivedFrom":[sQuery(id+"F0.wireOp",EDGE,"E1.right"),subQ0]}),1.0]])],"derivedFrom":subQ0})])],"isStart":true});}
            var Q204;
            {var subQ0=sQuery(id+"F0.wireOp",EDGE,"E5.right");Q204=makeQuery(id+"F1.opExtrude","CAP_EDGE",EDGE,{"disambiguationData":[OSD([subQ0]),TDD([makeQuery(id+"F0.imprint","IMPRINT",EDGE,{"disambiguationData":[TD([[makeQuery(id+"F0.imprint","INTERSECT",VERTEX,{"derivedFrom":[subQ0,sQuery(id+"F0.wireOp",EDGE,"E14.bottom")]}),-1.0]])],"derivedFrom":subQ0})])],"isStart":true});}
            var Q205;
            Q205=makeQuery(id+"F1.opExtrude","SWEPT_EDGE",EDGE,{"disambiguationData":[OSD([sQuery(id+"F0.wireOp",EDGE,"E14.bottom"),sQuery(id+"F0.wireOp",EDGE,"E23")])]});
            var Q206;
            {var subQ0=sQuery(id+"F0.wireOp",EDGE,"E11.right");Q206=makeQuery(id+"F1.opExtrude","CAP_EDGE",EDGE,{"disambiguationData":[OSD([subQ0]),TDD([makeQuery(id+"F0.imprint","IMPRINT",EDGE,{"disambiguationData":[TD([[makeQuery(id+"F0.imprint","INTERSECT",VERTEX,{"derivedFrom":[sQuery(id+"F0.wireOp",EDGE,"E11.bottom"),subQ0]}),-1.0]])],"derivedFrom":subQ0})])],"isStart":true});}
            var Q207;
            Q207=makeQuery(id+"F1.opExtrude","CAP_EDGE",EDGE,{"disambiguationData":[OSD([sQuery(id+"F0.wireOp",EDGE,"E21")])],"isStart":false});
            var Q208;
            {var subQ0=sQuery(id+"F0.wireOp",EDGE,"E1.left");Q208=makeQuery(id+"F1.opExtrude","CAP_EDGE",EDGE,{"disambiguationData":[OSD([subQ0]),TDD([makeQuery(id+"F0.imprint","IMPRINT",EDGE,{"disambiguationData":[TD([[makeQuery(id+"F0.imprint","INTERSECT",VERTEX,{"derivedFrom":[subQ0,sQuery(id+"F0.wireOp",EDGE,"E14.bottom")]}),-1.0]])],"derivedFrom":subQ0})])],"isStart":true});}
            var Q209;
            {var subQ0=sQuery(id+"F0.wireOp",EDGE,"E9.right");Q209=makeQuery(id+"F1.opExtrude","CAP_EDGE",EDGE,{"disambiguationData":[OSD([subQ0]),TDD([makeQuery(id+"F0.imprint","IMPRINT",EDGE,{"disambiguationData":[TD([[makeQuery(id+"F0.imprint","INTERSECT",VERTEX,{"derivedFrom":[subQ0,sQuery(id+"F0.wireOp",EDGE,"E30")]}),1.0]])],"derivedFrom":subQ0})])],"isStart":true});}
            var Q210;
            Q210=makeQuery(id+"F1.opExtrude","SWEPT_EDGE",EDGE,{"disambiguationData":[OSD([sQuery(id+"F0.wireOp",EDGE,"E9.right"),sQuery(id+"F0.wireOp",EDGE,"E30")])]});
            var Q211;
            {var subQ0=sQuery(id+"F0.wireOp",EDGE,"E2.right");Q211=makeQuery(id+"F1.opExtrude","CAP_EDGE",EDGE,{"disambiguationData":[OSD([subQ0]),TDD([makeQuery(id+"F0.imprint","IMPRINT",EDGE,{"disambiguationData":[TD([[makeQuery(id+"F0.imprint","INTERSECT",VERTEX,{"derivedFrom":[subQ0,sQuery(id+"F0.wireOp",EDGE,"E14.bottom")]}),-1.0]])],"derivedFrom":subQ0})])],"isStart":true});}
            var Q212;
            Q212=makeQuery(id+"F1.opExtrude","SWEPT_EDGE",EDGE,{"disambiguationData":[OSD([sQuery(id+"F0.wireOp",EDGE,"E14.top"),sQuery(id+"F0.wireOp",EDGE,"E15")])]});
            var Q213;
            {var subQ0=sQuery(id+"F0.wireOp",EDGE,"E13.bottom");Q213=makeQuery(id+"F1.opExtrude","CAP_EDGE",EDGE,{"disambiguationData":[OSD([subQ0]),TDD([makeQuery(id+"F0.imprint","IMPRINT",EDGE,{"disambiguationData":[TD([[makeQuery(id+"F0.imprint","INTERSECT",VERTEX,{"derivedFrom":[sQuery(id+"F0.wireOp",EDGE,"E11.left"),subQ0]}),-1.0]])],"derivedFrom":subQ0})])],"isStart":true});}
            var Q214;
            Q214=makeQuery(id+"F1.opExtrude","SWEPT_EDGE",EDGE,{"disambiguationData":[OSD([sQuery(id+"F0.wireOp",EDGE,"E6.top"),sQuery(id+"F0.wireOp",EDGE,"E6.right")])]});
            var Q215;
            {var subQ0=sQuery(id+"F0.wireOp",EDGE,"E5.right");Q215=makeQuery(id+"F1.opExtrude","CAP_EDGE",EDGE,{"disambiguationData":[OSD([subQ0]),TDD([makeQuery(id+"F0.imprint","IMPRINT",EDGE,{"disambiguationData":[TD([[makeQuery(id+"F0.imprint","INTERSECT",VERTEX,{"derivedFrom":[subQ0,sQuery(id+"F0.wireOp",EDGE,"E20")]}),-1.0]])],"derivedFrom":subQ0})])],"isStart":true});}
            var Q216;
            {var subQ0=sQuery(id+"F0.wireOp",EDGE,"E6.right");Q216=makeQuery(id+"F1.opExtrude","CAP_EDGE",EDGE,{"disambiguationData":[OSD([subQ0]),TDD([makeQuery(id+"F0.imprint","IMPRINT",EDGE,{"disambiguationData":[TD([[makeQuery(id+"F0.imprint","INTERSECT",VERTEX,{"derivedFrom":[subQ0,sQuery(id+"F0.wireOp",EDGE,"E14.bottom")]}),-1.0]])],"derivedFrom":subQ0})])],"isStart":true});}
            var Q217;
            {var subQ0=sQuery(id+"F0.wireOp",EDGE,"E11.left");Q217=makeQuery(id+"F1.opExtrude","CAP_EDGE",EDGE,{"disambiguationData":[OSD([subQ0]),TDD([makeQuery(id+"F0.imprint","IMPRINT",EDGE,{"disambiguationData":[TD([[makeQuery(id+"F0.imprint","INTERSECT",VERTEX,{"derivedFrom":[sQuery(id+"F0.wireOp",EDGE,"E11.top"),subQ0]}),1.0]])],"derivedFrom":subQ0})])],"isStart":true});}
            var Q218;
            {var subQ0=sQuery(id+"F0.wireOp",EDGE,"E23");Q218=makeQuery(id+"F1.opExtrude","CAP_EDGE",EDGE,{"disambiguationData":[OSD([subQ0]),TDD([makeQuery(id+"F0.imprint","IMPRINT",EDGE,{"disambiguationData":[TD([[makeQuery(id+"F0.imprint","INTERSECT",VERTEX,{"derivedFrom":[subQ0,sQuery(id+"F0.wireOp",EDGE,"E25")]}),-1.0]])],"derivedFrom":subQ0})])],"isStart":true});}
            var Q219;
            {var subQ0=sQuery(id+"F0.wireOp",EDGE,"E13.top");Q219=makeQuery(id+"F1.opExtrude","CAP_EDGE",EDGE,{"disambiguationData":[OSD([subQ0]),TDD([makeQuery(id+"F0.imprint","IMPRINT",EDGE,{"disambiguationData":[TD([[makeQuery(id+"F0.imprint","INTERSECT",VERTEX,{"derivedFrom":[subQ0,sQuery(id+"F0.wireOp",EDGE,"E15")]}),-1.0]])],"derivedFrom":subQ0})])],"isStart":true});}
            var Q220;
            {var subQ0=sQuery(id+"F0.wireOp",EDGE,"E3.right");Q220=makeQuery(id+"F1.opExtrude","CAP_EDGE",EDGE,{"disambiguationData":[OSD([subQ0]),TDD([makeQuery(id+"F0.imprint","IMPRINT",EDGE,{"disambiguationData":[TD([[makeQuery(id+"F0.imprint","INTERSECT",VERTEX,{"derivedFrom":[sQuery(id+"F0.wireOp",EDGE,"E3.bottom"),subQ0]}),-1.0]])],"derivedFrom":subQ0})])],"isStart":true});}
            var Q221;
            Q221=makeQuery(id+"F1.opExtrude","SWEPT_EDGE",EDGE,{"disambiguationData":[OSD([sQuery(id+"F0.wireOp",EDGE,"E24"),sQuery(id+"F0.wireOp",EDGE,"E31")])]});
            var Q222;
            Q222=makeQuery(id+"F1.opExtrude","SWEPT_EDGE",EDGE,{"disambiguationData":[OSD([sQuery(id+"F0.wireOp",EDGE,"E1.left"),sQuery(id+"F0.wireOp",EDGE,"E18")])]});
            var Q223;
            Q223=makeQuery(id+"F1.opExtrude","CAP_EDGE",EDGE,{"disambiguationData":[OSD([sQuery(id+"F0.wireOp",EDGE,"E28")])],"isStart":true});
            var Q224;
            Q224=makeQuery(id+"F1.opExtrude","SWEPT_EDGE",EDGE,{"disambiguationData":[OSD([sQuery(id+"F0.wireOp",EDGE,"E13.top"),sQuery(id+"F0.wireOp",EDGE,"E15")])]});
            var Q225;
            {var subQ0=sQuery(id+"F0.wireOp",EDGE,"E15");Q225=makeQuery(id+"F1.opExtrude","CAP_EDGE",EDGE,{"disambiguationData":[OSD([subQ0]),TDD([makeQuery(id+"F0.imprint","IMPRINT",EDGE,{"disambiguationData":[TD([[makeQuery(id+"F0.imprint","INTERSECT",VERTEX,{"derivedFrom":[sQuery(id+"F0.wireOp",EDGE,"E13.top"),subQ0]}),-1.0]])],"derivedFrom":subQ0})])],"isStart":true});}
            var Q226;
            {var subQ0=sQuery(id+"F0.wireOp",EDGE,"E6.right");Q226=makeQuery(id+"F1.opExtrude","CAP_EDGE",EDGE,{"disambiguationData":[OSD([subQ0]),TDD([makeQuery(id+"F0.imprint","IMPRINT",EDGE,{"disambiguationData":[TD([[makeQuery(id+"F0.imprint","INTERSECT",VERTEX,{"derivedFrom":[subQ0,sQuery(id+"F0.wireOp",EDGE,"E21")]}),-1.0]])],"derivedFrom":subQ0})])],"isStart":true});}
            var Q227;
            Q227=makeQuery(id+"F1.opExtrude","SWEPT_EDGE",EDGE,{"disambiguationData":[OSD([sQuery(id+"F0.wireOp",EDGE,"E2.right"),sQuery(id+"F0.wireOp",EDGE,"E14.bottom")])]});
            var Q228;
            Q228=makeQuery(id+"F1.opExtrude","SWEPT_EDGE",EDGE,{"disambiguationData":[OSD([sQuery(id+"F0.wireOp",EDGE,"E5.right"),sQuery(id+"F0.wireOp",EDGE,"E20")])]});
            var Q229;
            {var subQ0=sQuery(id+"F0.wireOp",EDGE,"E13.bottom");Q229=makeQuery(id+"F1.opExtrude","CAP_EDGE",EDGE,{"disambiguationData":[OSD([subQ0]),TDD([makeQuery(id+"F0.imprint","IMPRINT",EDGE,{"disambiguationData":[TD([[makeQuery(id+"F0.imprint","INTERSECT",VERTEX,{"derivedFrom":[subQ0,sQuery(id+"F0.wireOp",EDGE,"E15")]}),-1.0]])],"derivedFrom":subQ0})])],"isStart":true});}
            var Q230;
            Q230=makeQuery(id+"F1.opExtrude","SWEPT_EDGE",EDGE,{"disambiguationData":[OSD([sQuery(id+"F0.wireOp",EDGE,"E6.left"),sQuery(id+"F0.wireOp",EDGE,"E21")])]});
            var Q231;
            Q231=makeQuery(id+"F1.opExtrude","CAP_EDGE",EDGE,{"disambiguationData":[OSD([sQuery(id+"F0.wireOp",EDGE,"E29")])],"isStart":true});
            var Q232;
            {var subQ0=sQuery(id+"F0.wireOp",EDGE,"E11.left");Q232=makeQuery(id+"F1.opExtrude","CAP_EDGE",EDGE,{"disambiguationData":[OSD([subQ0]),TDD([makeQuery(id+"F0.imprint","IMPRINT",EDGE,{"disambiguationData":[TD([[makeQuery(id+"F0.imprint","INTERSECT",VERTEX,{"derivedFrom":[subQ0,sQuery(id+"F0.wireOp",EDGE,"E14.bottom")]}),-1.0]])],"derivedFrom":subQ0})])],"isStart":true});}
            var Q233;
            {var subQ0=sQuery(id+"F0.wireOp",EDGE,"E13.top");Q233=makeQuery(id+"F1.opExtrude","CAP_EDGE",EDGE,{"disambiguationData":[OSD([subQ0]),TDD([makeQuery(id+"F0.imprint","IMPRINT",EDGE,{"disambiguationData":[TD([[makeQuery(id+"F0.imprint","INTERSECT",VERTEX,{"derivedFrom":[sQuery(id+"F0.wireOp",EDGE,"E2.right"),subQ0]}),-1.0]])],"derivedFrom":subQ0})])],"isStart":true});}
            var Q234;
            Q234=makeQuery(id+"F1.opExtrude","SWEPT_EDGE",EDGE,{"disambiguationData":[OSD([sQuery(id+"F0.wireOp",EDGE,"E15"),sQuery(id+"F0.wireOp",EDGE,"E31")])]});
            var Q235;
            {var subQ0=sQuery(id+"F0.wireOp",EDGE,"E13.top");Q235=makeQuery(id+"F1.opExtrude","CAP_EDGE",EDGE,{"disambiguationData":[OSD([subQ0]),TDD([makeQuery(id+"F0.imprint","IMPRINT",EDGE,{"disambiguationData":[TD([[makeQuery(id+"F0.imprint","INTERSECT",VERTEX,{"derivedFrom":[sQuery(id+"F0.wireOp",EDGE,"E2.left"),subQ0]}),1.0]])],"derivedFrom":subQ0})])],"isStart":true});}
            var Q236;
            {var subQ0=sQuery(id+"F0.wireOp",EDGE,"E15");Q236=makeQuery(id+"F1.opExtrude","CAP_EDGE",EDGE,{"disambiguationData":[OSD([subQ0]),TDD([makeQuery(id+"F0.imprint","IMPRINT",EDGE,{"disambiguationData":[TD([[makeQuery(id+"F0.imprint","INTERSECT",VERTEX,{"derivedFrom":[subQ0,sQuery(id+"F0.wireOp",EDGE,"E26")]}),-1.0]])],"derivedFrom":subQ0})])],"isStart":true});}
            var Q237;
            {var subQ0=sQuery(id+"F0.wireOp",EDGE,"E11.right");Q237=makeQuery(id+"F1.opExtrude","CAP_EDGE",EDGE,{"disambiguationData":[OSD([subQ0]),TDD([makeQuery(id+"F0.imprint","IMPRINT",EDGE,{"disambiguationData":[TD([[makeQuery(id+"F0.imprint","INTERSECT",VERTEX,{"derivedFrom":[subQ0,sQuery(id+"F0.wireOp",EDGE,"E14.bottom")]}),-1.0]])],"derivedFrom":subQ0})])],"isStart":true});}
            var Q238;
            {var subQ0=sQuery(id+"F0.wireOp",EDGE,"E13.top");Q238=makeQuery(id+"F1.opExtrude","CAP_EDGE",EDGE,{"disambiguationData":[OSD([subQ0]),TDD([makeQuery(id+"F0.imprint","IMPRINT",EDGE,{"disambiguationData":[TD([[makeQuery(id+"F0.imprint","INTERSECT",VERTEX,{"derivedFrom":[sQuery(id+"F0.wireOp",EDGE,"E9.right"),subQ0]}),-1.0]])],"derivedFrom":subQ0})])],"isStart":true});}
            var Q239;
            Q239=makeQuery(id+"F1.opExtrude","SWEPT_EDGE",EDGE,{"disambiguationData":[OSD([sQuery(id+"F0.wireOp",EDGE,"E7.right"),sQuery(id+"F0.wireOp",EDGE,"E13.bottom")])]});
            var Q240;
            Q240=makeQuery(id+"F1.opExtrude","SWEPT_EDGE",EDGE,{"disambiguationData":[OSD([sQuery(id+"F0.wireOp",EDGE,"E23"),sQuery(id+"F0.wireOp",EDGE,"E30")])]});
            var Q241;
            Q241=makeQuery(id+"F1.opExtrude","SWEPT_EDGE",EDGE,{"disambiguationData":[OSD([sQuery(id+"F0.wireOp",EDGE,"E11.bottom"),sQuery(id+"F0.wireOp",EDGE,"E11.left")])]});
            var Q242;
            {var subQ0=sQuery(id+"F0.wireOp",EDGE,"E13.bottom");Q242=makeQuery(id+"F1.opExtrude","CAP_EDGE",EDGE,{"disambiguationData":[OSD([subQ0]),TDD([makeQuery(id+"F0.imprint","IMPRINT",EDGE,{"disambiguationData":[TD([[makeQuery(id+"F0.imprint","INTERSECT",VERTEX,{"derivedFrom":[sQuery(id+"F0.wireOp",EDGE,"E6.left"),subQ0]}),-1.0]])],"derivedFrom":subQ0})])],"isStart":true});}
            var Q243;
            Q243=makeQuery(id+"F1.opExtrude","SWEPT_EDGE",EDGE,{"disambiguationData":[OSD([sQuery(id+"F0.wireOp",EDGE,"E13.top"),sQuery(id+"F0.wireOp",EDGE,"E23")])]});
            var Q244;
            Q244=makeQuery(id+"F1.opExtrude","SWEPT_EDGE",EDGE,{"disambiguationData":[OSD([sQuery(id+"F0.wireOp",EDGE,"E3.right"),sQuery(id+"F0.wireOp",EDGE,"E14.bottom")])]});
            var Q245;
            Q245=makeQuery(id+"F1.opExtrude","CAP_EDGE",EDGE,{"disambiguationData":[OSD([sQuery(id+"F0.wireOp",EDGE,"E26")])],"isStart":true});
            var Q246;
            Q246=makeQuery(id+"F1.opExtrude","CAP_EDGE",EDGE,{"disambiguationData":[OSD([sQuery(id+"F0.wireOp",EDGE,"E11.top")])],"isStart":true});
            var Q247;
            {var subQ0=sQuery(id+"F0.wireOp",EDGE,"E14.top");Q247=makeQuery(id+"F1.opExtrude","CAP_EDGE",EDGE,{"disambiguationData":[OSD([subQ0]),TDD([makeQuery(id+"F0.imprint","IMPRINT",EDGE,{"disambiguationData":[TD([[makeQuery(id+"F0.imprint","INTERSECT",VERTEX,{"derivedFrom":[sQuery(id+"F0.wireOp",EDGE,"E3.right"),subQ0]}),1.0]])],"derivedFrom":subQ0})])],"isStart":true});}
            var Q248;
            Q248=makeQuery(id+"F1.opExtrude","SWEPT_EDGE",EDGE,{"disambiguationData":[OSD([sQuery(id+"F0.wireOp",EDGE,"E4.right"),sQuery(id+"F0.wireOp",EDGE,"E13.top")])]});
            var Q249;
            Q249=makeQuery(id+"F1.opExtrude","CAP_EDGE",EDGE,{"disambiguationData":[OSD([sQuery(id+"F0.wireOp",EDGE,"E22")])],"isStart":true});
            var Q250;
            {var subQ0=sQuery(id+"F0.wireOp",EDGE,"E13.bottom");Q250=makeQuery(id+"F1.opExtrude","CAP_EDGE",EDGE,{"disambiguationData":[OSD([subQ0]),TDD([makeQuery(id+"F0.imprint","IMPRINT",EDGE,{"disambiguationData":[TD([[makeQuery(id+"F0.imprint","INTERSECT",VERTEX,{"derivedFrom":[sQuery(id+"F0.wireOp",EDGE,"E10.left"),subQ0]}),-1.0]])],"derivedFrom":subQ0})])],"isStart":true});}
            var Q251;
            Q251=makeQuery(id+"F1.opExtrude","SWEPT_EDGE",EDGE,{"disambiguationData":[OSD([sQuery(id+"F0.wireOp",EDGE,"E13.bottom"),sQuery(id+"F0.wireOp",EDGE,"E15")])]});
            var Q252;
            Q252=makeQuery(id+"F1.opExtrude","SWEPT_EDGE",EDGE,{"disambiguationData":[OSD([sQuery(id+"F0.wireOp",EDGE,"E4.right"),sQuery(id+"F0.wireOp",EDGE,"E14.top")])]});
            var Q253;
            {var subQ0=sQuery(id+"F0.wireOp",EDGE,"E10.left");Q253=makeQuery(id+"F1.opExtrude","CAP_EDGE",EDGE,{"disambiguationData":[OSD([subQ0]),TDD([makeQuery(id+"F0.imprint","IMPRINT",EDGE,{"disambiguationData":[TD([[makeQuery(id+"F0.imprint","INTERSECT",VERTEX,{"derivedFrom":[subQ0,sQuery(id+"F0.wireOp",EDGE,"E14.bottom")]}),-1.0]])],"derivedFrom":subQ0})])],"isStart":true});}
            var Q254;
            Q254=makeQuery(id+"F1.opExtrude","SWEPT_EDGE",EDGE,{"disambiguationData":[OSD([sQuery(id+"F0.wireOp",EDGE,"E8.left"),sQuery(id+"F0.wireOp",EDGE,"E14.top")])]});
            var Q255;
            Q255=makeQuery(id+"F1.opExtrude","SWEPT_EDGE",EDGE,{"disambiguationData":[OSD([sQuery(id+"F0.wireOp",EDGE,"E9.right"),sQuery(id+"F0.wireOp",EDGE,"E14.bottom")])]});
            var Q256;
            Q256=makeQuery(id+"F1.opExtrude","CAP_EDGE",EDGE,{"disambiguationData":[OSD([sQuery(id+"F0.wireOp",EDGE,"E6.top")])],"isStart":true});
            var Q257;
            Q257=makeQuery(id+"F1.opExtrude","SWEPT_EDGE",EDGE,{"disambiguationData":[OSD([sQuery(id+"F0.wireOp",EDGE,"E9.right"),sQuery(id+"F0.wireOp",EDGE,"E25")])]});
            var Q258;
            Q258=makeQuery(id+"F1.opExtrude","SWEPT_EDGE",EDGE,{"disambiguationData":[OSD([sQuery(id+"F0.wireOp",EDGE,"E6.left"),sQuery(id+"F0.wireOp",EDGE,"E13.bottom")])]});
            var Q259;
            Q259=makeQuery(id+"F1.opExtrude","SWEPT_EDGE",EDGE,{"disambiguationData":[OSD([sQuery(id+"F0.wireOp",EDGE,"E4.right"),sQuery(id+"F0.wireOp",EDGE,"E14.bottom")])]});
            var Q260;
            Q260=makeQuery(id+"F1.opExtrude","SWEPT_EDGE",EDGE,{"disambiguationData":[OSD([sQuery(id+"F0.wireOp",EDGE,"E13.bottom"),sQuery(id+"F0.wireOp",EDGE,"E24")])]});
            var Q261;
            Q261=makeQuery(id+"F1.opExtrude","SWEPT_EDGE",EDGE,{"disambiguationData":[OSD([sQuery(id+"F0.wireOp",EDGE,"E11.right"),sQuery(id+"F0.wireOp",EDGE,"E13.bottom")])]});
            var Q262;
            Q262=makeQuery(id+"F1.opExtrude","SWEPT_EDGE",EDGE,{"disambiguationData":[OSD([sQuery(id+"F0.wireOp",EDGE,"E24"),sQuery(id+"F0.wireOp",EDGE,"E26")])]});
            var Q263;
            Q263=makeQuery(id+"F1.opExtrude","SWEPT_EDGE",EDGE,{"disambiguationData":[OSD([sQuery(id+"F0.wireOp",EDGE,"E14.bottom"),sQuery(id+"F0.wireOp",EDGE,"E24")])]});
            var Q264;
            {var subQ0=sQuery(id+"F0.wireOp",EDGE,"E1.right");Q264=makeQuery(id+"F1.opExtrude","CAP_EDGE",EDGE,{"disambiguationData":[OSD([subQ0]),TDD([makeQuery(id+"F0.imprint","IMPRINT",EDGE,{"disambiguationData":[TD([[makeQuery(id+"F0.imprint","INTERSECT",VERTEX,{"derivedFrom":[subQ0,sQuery(id+"F0.wireOp",EDGE,"E22")]}),-1.0]])],"derivedFrom":subQ0})])],"isStart":false});}
            var Q265;
            Q265=makeQuery(id+"F1.opExtrude","SWEPT_EDGE",EDGE,{"disambiguationData":[OSD([sQuery(id+"F0.wireOp",EDGE,"E9.right"),sQuery(id+"F0.wireOp",EDGE,"E13.bottom")])]});
            var Q266;
            Q266=makeQuery(id+"F1.opExtrude","CAP_EDGE",EDGE,{"disambiguationData":[OSD([sQuery(id+"F0.wireOp",EDGE,"E11.bottom")])],"isStart":true});
            var Q267;
            {var subQ0=sQuery(id+"F0.wireOp",EDGE,"E1.left");Q267=makeQuery(id+"F1.opExtrude","CAP_EDGE",EDGE,{"disambiguationData":[OSD([subQ0]),TDD([makeQuery(id+"F0.imprint","IMPRINT",EDGE,{"disambiguationData":[TD([[makeQuery(id+"F0.imprint","INTERSECT",VERTEX,{"derivedFrom":[subQ0,sQuery(id+"F0.wireOp",EDGE,"E29")]}),1.0]])],"derivedFrom":subQ0})])],"isStart":true});}
            var Q268;
            {var subQ0=sQuery(id+"F0.wireOp",EDGE,"E13.bottom");Q268=makeQuery(id+"F1.opExtrude","CAP_EDGE",EDGE,{"disambiguationData":[OSD([subQ0]),TDD([makeQuery(id+"F0.imprint","IMPRINT",EDGE,{"disambiguationData":[TD([[makeQuery(id+"F0.imprint","INTERSECT",VERTEX,{"derivedFrom":[sQuery(id+"F0.wireOp",EDGE,"E3.right"),subQ0]}),1.0]])],"derivedFrom":subQ0})])],"isStart":true});}
            var Q269;
            Q269=makeQuery(id+"F1.opExtrude","SWEPT_EDGE",EDGE,{"disambiguationData":[OSD([sQuery(id+"F0.wireOp",EDGE,"E8.left"),sQuery(id+"F0.wireOp",EDGE,"E13.bottom")])]});
            var Q270;
            Q270=makeQuery(id+"F1.opExtrude","SWEPT_EDGE",EDGE,{"disambiguationData":[OSD([sQuery(id+"F0.wireOp",EDGE,"E10.top"),sQuery(id+"F0.wireOp",EDGE,"E10.right")])]});
            var Q271;
            Q271=makeQuery(id+"F1.opExtrude","CAP_EDGE",EDGE,{"disambiguationData":[OSD([sQuery(id+"F0.wireOp",EDGE,"E20")])],"isStart":true});
            var Q272;
            {var subQ0=sQuery(id+"F0.wireOp",EDGE,"E24");Q272=makeQuery(id+"F1.opExtrude","CAP_EDGE",EDGE,{"disambiguationData":[OSD([subQ0]),TDD([makeQuery(id+"F0.imprint","IMPRINT",EDGE,{"disambiguationData":[TD([[makeQuery(id+"F0.imprint","INTERSECT",VERTEX,{"derivedFrom":[subQ0,sQuery(id+"F0.wireOp",EDGE,"E31")]}),1.0]])],"derivedFrom":subQ0})])],"isStart":true});}
            var Q273;
            {var subQ0=sQuery(id+"F0.wireOp",EDGE,"E13.bottom");Q273=makeQuery(id+"F1.opExtrude","CAP_EDGE",EDGE,{"disambiguationData":[OSD([subQ0]),TDD([makeQuery(id+"F0.imprint","IMPRINT",EDGE,{"disambiguationData":[TD([[makeQuery(id+"F0.imprint","INTERSECT",VERTEX,{"derivedFrom":[sQuery(id+"F0.wireOp",EDGE,"E4.right"),subQ0]}),-1.0]])],"derivedFrom":subQ0})])],"isStart":true});}
            var Q274;
            {var subQ0=sQuery(id+"F0.wireOp",EDGE,"E24");Q274=makeQuery(id+"F1.opExtrude","CAP_EDGE",EDGE,{"disambiguationData":[OSD([subQ0]),TDD([makeQuery(id+"F0.imprint","IMPRINT",EDGE,{"disambiguationData":[TD([[makeQuery(id+"F0.imprint","INTERSECT",VERTEX,{"derivedFrom":[sQuery(id+"F0.wireOp",EDGE,"E14.bottom"),subQ0]}),-1.0]])],"derivedFrom":subQ0})])],"isStart":true});}
            var Q275;
            Q275=makeQuery(id+"F1.opExtrude","SWEPT_EDGE",EDGE,{"disambiguationData":[OSD([sQuery(id+"F0.wireOp",EDGE,"E10.bottom"),sQuery(id+"F0.wireOp",EDGE,"E10.right")])]});
            var Q276;
            {var subQ0=sQuery(id+"F0.wireOp",EDGE,"E10.right");Q276=makeQuery(id+"F1.opExtrude","CAP_EDGE",EDGE,{"disambiguationData":[OSD([subQ0]),TDD([makeQuery(id+"F0.imprint","IMPRINT",EDGE,{"disambiguationData":[TD([[makeQuery(id+"F0.imprint","INTERSECT",VERTEX,{"derivedFrom":[sQuery(id+"F0.wireOp",EDGE,"E10.top"),subQ0]}),1.0]])],"derivedFrom":subQ0})])],"isStart":true});}
            var Q277;
            {var subQ0=sQuery(id+"F0.wireOp",EDGE,"E23");Q277=makeQuery(id+"F1.opExtrude","CAP_EDGE",EDGE,{"disambiguationData":[OSD([subQ0]),TDD([makeQuery(id+"F0.imprint","IMPRINT",EDGE,{"disambiguationData":[TD([[makeQuery(id+"F0.imprint","INTERSECT",VERTEX,{"derivedFrom":[subQ0,sQuery(id+"F0.wireOp",EDGE,"E30")]}),1.0]])],"derivedFrom":subQ0})])],"isStart":true});}
            var Q278;
            {var subQ0=sQuery(id+"F0.wireOp",EDGE,"E4.right");Q278=makeQuery(id+"F1.opExtrude","CAP_EDGE",EDGE,{"disambiguationData":[OSD([subQ0]),TDD([makeQuery(id+"F0.imprint","IMPRINT",EDGE,{"disambiguationData":[TD([[makeQuery(id+"F0.imprint","INTERSECT",VERTEX,{"derivedFrom":[subQ0,sQuery(id+"F0.wireOp",EDGE,"E13.bottom")]}),-1.0]])],"derivedFrom":subQ0})])],"isStart":true});}
            var Q279;
            Q279=makeQuery(id+"F1.opExtrude","SWEPT_EDGE",EDGE,{"disambiguationData":[OSD([sQuery(id+"F0.wireOp",EDGE,"E4.right"),sQuery(id+"F0.wireOp",EDGE,"E20")])]});
            var Q280;
            Q280=makeQuery(id+"F1.opExtrude","SWEPT_EDGE",EDGE,{"disambiguationData":[OSD([sQuery(id+"F0.wireOp",EDGE,"E6.left"),sQuery(id+"F0.wireOp",EDGE,"E14.bottom")])]});
            var Q281;
            Q281=makeQuery(id+"F1.opExtrude","SWEPT_EDGE",EDGE,{"disambiguationData":[OSD([sQuery(id+"F0.wireOp",EDGE,"E5.right"),sQuery(id+"F0.wireOp",EDGE,"E14.top")])]});
            var Q282;
            Q282=makeQuery(id+"F1.opExtrude","CAP_EDGE",EDGE,{"disambiguationData":[OSD([sQuery(id+"F0.wireOp",EDGE,"E30")])],"isStart":true});
            var Q283;
            Q283=makeQuery(id+"F1.opExtrude","SWEPT_EDGE",EDGE,{"disambiguationData":[OSD([sQuery(id+"F0.wireOp",EDGE,"E2.right"),sQuery(id+"F0.wireOp",EDGE,"E13.bottom")])]});
            var Q284;
            Q284=makeQuery(id+"F1.opExtrude","SWEPT_EDGE",EDGE,{"disambiguationData":[OSD([sQuery(id+"F0.wireOp",EDGE,"E5.right"),sQuery(id+"F0.wireOp",EDGE,"E13.top")])]});
            var Q285;
            Q285=makeQuery(id+"F1.opExtrude","SWEPT_EDGE",EDGE,{"disambiguationData":[OSD([sQuery(id+"F0.wireOp",EDGE,"E8.left"),sQuery(id+"F0.wireOp",EDGE,"E27")])]});
            var Q286;
            Q286=makeQuery(id+"F1.opExtrude","SWEPT_EDGE",EDGE,{"disambiguationData":[OSD([sQuery(id+"F0.wireOp",EDGE,"E7.right"),sQuery(id+"F0.wireOp",EDGE,"E22")])]});
            var Q287;
            {var subQ0=sQuery(id+"F0.wireOp",EDGE,"E14.top");Q287=makeQuery(id+"F1.opExtrude","CAP_EDGE",EDGE,{"disambiguationData":[OSD([subQ0]),TDD([makeQuery(id+"F0.imprint","IMPRINT",EDGE,{"disambiguationData":[TD([[makeQuery(id+"F0.imprint","INTERSECT",VERTEX,{"derivedFrom":[sQuery(id+"F0.wireOp",EDGE,"E9.right"),subQ0]}),-1.0]])],"derivedFrom":subQ0})])],"isStart":false});}
            var Q288;
            {var subQ0=sQuery(id+"F0.wireOp",EDGE,"E1.right");Q288=makeQuery(id+"F1.opExtrude","CAP_EDGE",EDGE,{"disambiguationData":[OSD([subQ0]),TDD([makeQuery(id+"F0.imprint","IMPRINT",EDGE,{"disambiguationData":[TD([[makeQuery(id+"F0.imprint","INTERSECT",VERTEX,{"derivedFrom":[subQ0,sQuery(id+"F0.wireOp",EDGE,"E14.bottom")]}),-1.0]])],"derivedFrom":subQ0})])],"isStart":true});}
            var Q289;
            Q289=makeQuery(id+"F1.opExtrude","SWEPT_EDGE",EDGE,{"disambiguationData":[OSD([sQuery(id+"F0.wireOp",EDGE,"E2.left"),sQuery(id+"F0.wireOp",EDGE,"E29")])]});
            var Q290;
            {var subQ0=sQuery(id+"F0.wireOp",EDGE,"E10.right");Q290=makeQuery(id+"F1.opExtrude","CAP_EDGE",EDGE,{"disambiguationData":[OSD([subQ0]),TDD([makeQuery(id+"F0.imprint","IMPRINT",EDGE,{"disambiguationData":[TD([[makeQuery(id+"F0.imprint","INTERSECT",VERTEX,{"derivedFrom":[sQuery(id+"F0.wireOp",EDGE,"E10.bottom"),subQ0]}),-1.0]])],"derivedFrom":subQ0})])],"isStart":true});}
            var Q291;
            {var subQ0=sQuery(id+"F0.wireOp",EDGE,"E14.top");Q291=makeQuery(id+"F1.opExtrude","CAP_EDGE",EDGE,{"disambiguationData":[OSD([subQ0]),TDD([makeQuery(id+"F0.imprint","IMPRINT",EDGE,{"disambiguationData":[TD([[makeQuery(id+"F0.imprint","INTERSECT",VERTEX,{"derivedFrom":[sQuery(id+"F0.wireOp",EDGE,"E4.right"),subQ0]}),-1.0]])],"derivedFrom":subQ0})])],"isStart":true});}
            var Q292;
            {var subQ0=sQuery(id+"F0.wireOp",EDGE,"E7.right");Q292=makeQuery(id+"F1.opExtrude","CAP_EDGE",EDGE,{"disambiguationData":[OSD([subQ0]),TDD([makeQuery(id+"F0.imprint","IMPRINT",EDGE,{"disambiguationData":[TD([[makeQuery(id+"F0.imprint","INTERSECT",VERTEX,{"derivedFrom":[subQ0,sQuery(id+"F0.wireOp",EDGE,"E22")]}),-1.0]])],"derivedFrom":subQ0})])],"isStart":true});}
            var Q293;
            {var subQ0=sQuery(id+"F0.wireOp",EDGE,"E4.right");Q293=makeQuery(id+"F1.opExtrude","CAP_EDGE",EDGE,{"disambiguationData":[OSD([subQ0]),TDD([makeQuery(id+"F0.imprint","IMPRINT",EDGE,{"disambiguationData":[TD([[makeQuery(id+"F0.imprint","INTERSECT",VERTEX,{"derivedFrom":[subQ0,sQuery(id+"F0.wireOp",EDGE,"E14.top")]}),-1.0]])],"derivedFrom":subQ0})])],"isStart":true});}
            var Q294;
            Q294=makeQuery(id+"F1.opExtrude","SWEPT_EDGE",EDGE,{"disambiguationData":[OSD([sQuery(id+"F0.wireOp",EDGE,"E10.left"),sQuery(id+"F0.wireOp",EDGE,"E14.top")])]});
            var Q295;
            {var subQ0=sQuery(id+"F0.wireOp",EDGE,"E4.right");Q295=makeQuery(id+"F1.opExtrude","CAP_EDGE",EDGE,{"disambiguationData":[OSD([subQ0]),TDD([makeQuery(id+"F0.imprint","IMPRINT",EDGE,{"disambiguationData":[TD([[makeQuery(id+"F0.imprint","INTERSECT",VERTEX,{"derivedFrom":[subQ0,sQuery(id+"F0.wireOp",EDGE,"E28")]}),-1.0]])],"derivedFrom":subQ0})])],"isStart":true});}
            var Q296;
            {var subQ0=sQuery(id+"F0.wireOp",EDGE,"E14.top");Q296=makeQuery(id+"F1.opExtrude","CAP_EDGE",EDGE,{"disambiguationData":[OSD([subQ0]),TDD([makeQuery(id+"F0.imprint","IMPRINT",EDGE,{"disambiguationData":[TD([[makeQuery(id+"F0.imprint","INTERSECT",VERTEX,{"derivedFrom":[sQuery(id+"F0.wireOp",EDGE,"E11.left"),subQ0]}),-1.0]])],"derivedFrom":subQ0})])],"isStart":true});}
            var Q297;
            Q297=makeQuery(id+"F1.opExtrude","SWEPT_EDGE",EDGE,{"disambiguationData":[OSD([sQuery(id+"F0.wireOp",EDGE,"E10.top"),sQuery(id+"F0.wireOp",EDGE,"E10.left")])]});
            var Q298;
            {var subQ0=sQuery(id+"F0.wireOp",EDGE,"E9.right");Q298=makeQuery(id+"F1.opExtrude","CAP_EDGE",EDGE,{"disambiguationData":[OSD([subQ0]),TDD([makeQuery(id+"F0.imprint","IMPRINT",EDGE,{"disambiguationData":[TD([[makeQuery(id+"F0.imprint","INTERSECT",VERTEX,{"derivedFrom":[subQ0,sQuery(id+"F0.wireOp",EDGE,"E13.bottom")]}),1.0]])],"derivedFrom":subQ0})])],"isStart":true});}
            var Q299;
            {var subQ0=sQuery(id+"F0.wireOp",EDGE,"E1.right");Q299=makeQuery(id+"F1.opExtrude","CAP_EDGE",EDGE,{"disambiguationData":[OSD([subQ0]),TDD([makeQuery(id+"F0.imprint","IMPRINT",EDGE,{"disambiguationData":[TD([[makeQuery(id+"F0.imprint","INTERSECT",VERTEX,{"derivedFrom":[subQ0,sQuery(id+"F0.wireOp",EDGE,"E13.top")]}),-1.0]])],"derivedFrom":subQ0})])],"isStart":true});}
            var Q300;
            Q300=makeQuery(id+"F1.opExtrude","CAP_EDGE",EDGE,{"disambiguationData":[OSD([sQuery(id+"F0.wireOp",EDGE,"E25")])],"isStart":true});
            var Q301;
            {var subQ0=sQuery(id+"F0.wireOp",EDGE,"E8.left");Q301=makeQuery(id+"F1.opExtrude","CAP_EDGE",EDGE,{"disambiguationData":[OSD([subQ0]),TDD([makeQuery(id+"F0.imprint","IMPRINT",EDGE,{"disambiguationData":[TD([[makeQuery(id+"F0.imprint","INTERSECT",VERTEX,{"derivedFrom":[subQ0,sQuery(id+"F0.wireOp",EDGE,"E13.top")]}),-1.0]])],"derivedFrom":subQ0})])],"isStart":true});}
            var Q302;
            Q302=makeQuery(id+"F1.opExtrude","CAP_EDGE",EDGE,{"disambiguationData":[OSD([sQuery(id+"F0.wireOp",EDGE,"E3.bottom")])],"isStart":true});
            var Q303;
            Q303=makeQuery(id+"F1.opExtrude","SWEPT_EDGE",EDGE,{"disambiguationData":[OSD([sQuery(id+"F0.wireOp",EDGE,"E14.top"),sQuery(id+"F0.wireOp",EDGE,"E16")])]});
            var Q304;
            Q304=makeQuery(id+"F1.opExtrude","SWEPT_EDGE",EDGE,{"disambiguationData":[OSD([sQuery(id+"F0.wireOp",EDGE,"E2.left"),sQuery(id+"F0.wireOp",EDGE,"E14.bottom")])]});
            var Q305;
            Q305=makeQuery(id+"F1.opExtrude","SWEPT_EDGE",EDGE,{"disambiguationData":[OSD([sQuery(id+"F0.wireOp",EDGE,"E10.bottom"),sQuery(id+"F0.wireOp",EDGE,"E10.left")])]});
            var Q306;
            Q306=makeQuery(id+"F1.opExtrude","SWEPT_EDGE",EDGE,{"disambiguationData":[OSD([sQuery(id+"F0.wireOp",EDGE,"E1.right"),sQuery(id+"F0.wireOp",EDGE,"E13.bottom")])]});
            var Q307;
            Q307=makeQuery(id+"F1.opExtrude","SWEPT_EDGE",EDGE,{"disambiguationData":[OSD([sQuery(id+"F0.wireOp",EDGE,"E15"),sQuery(id+"F0.wireOp",EDGE,"E26")])]});
            var Q308;
            Q308=makeQuery(id+"F1.opExtrude","SWEPT_EDGE",EDGE,{"disambiguationData":[OSD([sQuery(id+"F0.wireOp",EDGE,"E3.right"),sQuery(id+"F0.wireOp",EDGE,"E13.top")])]});
            var Q309;
            Q309=makeQuery(id+"F1.opExtrude","SWEPT_EDGE",EDGE,{"disambiguationData":[OSD([sQuery(id+"F0.wireOp",EDGE,"E1.left"),sQuery(id+"F0.wireOp",EDGE,"E14.bottom")])]});
            var Q310;
            Q310=makeQuery(id+"F1.opExtrude","SWEPT_EDGE",EDGE,{"disambiguationData":[OSD([sQuery(id+"F0.wireOp",EDGE,"E8.left"),sQuery(id+"F0.wireOp",EDGE,"E17")])]});
            var Q311;
            Q311=makeQuery(id+"F1.opExtrude","SWEPT_EDGE",EDGE,{"disambiguationData":[OSD([sQuery(id+"F0.wireOp",EDGE,"E7.right"),sQuery(id+"F0.wireOp",EDGE,"E14.bottom")])]});
            var Q312;
            Q312=makeQuery(id+"F1.opExtrude","SWEPT_EDGE",EDGE,{"disambiguationData":[OSD([sQuery(id+"F0.wireOp",EDGE,"E4.right"),sQuery(id+"F0.wireOp",EDGE,"E13.bottom")])]});
            var Q313;
            {var subQ0=sQuery(id+"F0.wireOp",EDGE,"E14.bottom");Q313=makeQuery(id+"F1.opExtrude","CAP_EDGE",EDGE,{"disambiguationData":[OSD([subQ0]),TDD([makeQuery(id+"F0.imprint","IMPRINT",EDGE,{"disambiguationData":[TD([[makeQuery(id+"F0.imprint","INTERSECT",VERTEX,{"derivedFrom":[sQuery(id+"F0.wireOp",EDGE,"E5.right"),subQ0]}),1.0]])],"derivedFrom":subQ0})])],"isStart":true});}
            var Q314;
            {var subQ0=sQuery(id+"F0.wireOp",EDGE,"E14.top");Q314=makeQuery(id+"F1.opExtrude","CAP_EDGE",EDGE,{"disambiguationData":[OSD([subQ0]),TDD([makeQuery(id+"F0.imprint","IMPRINT",EDGE,{"disambiguationData":[TD([[makeQuery(id+"F0.imprint","INTERSECT",VERTEX,{"derivedFrom":[sQuery(id+"F0.wireOp",EDGE,"E1.left"),subQ0]}),-1.0]])],"derivedFrom":subQ0})])],"isStart":false});}
            var Q315;
            {var subQ0=sQuery(id+"F0.wireOp",EDGE,"E7.right");Q315=makeQuery(id+"F1.opExtrude","CAP_EDGE",EDGE,{"disambiguationData":[OSD([subQ0]),TDD([makeQuery(id+"F0.imprint","IMPRINT",EDGE,{"disambiguationData":[TD([[makeQuery(id+"F0.imprint","INTERSECT",VERTEX,{"derivedFrom":[subQ0,sQuery(id+"F0.wireOp",EDGE,"E13.top")]}),-1.0]])],"derivedFrom":subQ0})])],"isStart":true});}
            var Q316;
            Q316=makeQuery(id+"F1.opExtrude","SWEPT_EDGE",EDGE,{"disambiguationData":[OSD([sQuery(id+"F0.wireOp",EDGE,"E10.left"),sQuery(id+"F0.wireOp",EDGE,"E14.bottom")])]});
            var Q317;
            {var subQ0=sQuery(id+"F0.wireOp",EDGE,"E3.right");Q317=makeQuery(id+"F1.opExtrude","CAP_EDGE",EDGE,{"disambiguationData":[OSD([subQ0]),TDD([makeQuery(id+"F0.imprint","IMPRINT",EDGE,{"disambiguationData":[TD([[makeQuery(id+"F0.imprint","INTERSECT",VERTEX,{"derivedFrom":[subQ0,sQuery(id+"F0.wireOp",EDGE,"E13.bottom")]}),-1.0]])],"derivedFrom":subQ0})])],"isStart":true});}
            var Q318;
            Q318=makeQuery(id+"F1.opExtrude","SWEPT_EDGE",EDGE,{"disambiguationData":[OSD([sQuery(id+"F0.wireOp",EDGE,"E23"),sQuery(id+"F0.wireOp",EDGE,"E25")])]});
            var Q319;
            Q319=makeQuery(id+"F1.opExtrude","SWEPT_EDGE",EDGE,{"disambiguationData":[OSD([sQuery(id+"F0.wireOp",EDGE,"E6.top"),sQuery(id+"F0.wireOp",EDGE,"E6.left")])]});
            var Q320;
            {var subQ0=sQuery(id+"F0.wireOp",EDGE,"E13.top");Q320=makeQuery(id+"F1.opExtrude","CAP_EDGE",EDGE,{"disambiguationData":[OSD([subQ0]),TDD([makeQuery(id+"F0.imprint","IMPRINT",EDGE,{"disambiguationData":[TD([[makeQuery(id+"F0.imprint","INTERSECT",VERTEX,{"derivedFrom":[sQuery(id+"F0.wireOp",EDGE,"E11.left"),subQ0]}),-1.0]])],"derivedFrom":subQ0})])],"isStart":true});}
            var Q321;
            {var subQ0=sQuery(id+"F0.wireOp",EDGE,"E10.left");Q321=makeQuery(id+"F1.opExtrude","CAP_EDGE",EDGE,{"disambiguationData":[OSD([subQ0]),TDD([makeQuery(id+"F0.imprint","IMPRINT",EDGE,{"disambiguationData":[TD([[makeQuery(id+"F0.imprint","INTERSECT",VERTEX,{"derivedFrom":[sQuery(id+"F0.wireOp",EDGE,"E10.bottom"),subQ0]}),-1.0]])],"derivedFrom":subQ0})])],"isStart":true});}
            var Q322;
            {var subQ0=sQuery(id+"F0.wireOp",EDGE,"E6.left");Q322=makeQuery(id+"F1.opExtrude","CAP_EDGE",EDGE,{"disambiguationData":[OSD([subQ0]),TDD([makeQuery(id+"F0.imprint","IMPRINT",EDGE,{"disambiguationData":[TD([[makeQuery(id+"F0.imprint","INTERSECT",VERTEX,{"derivedFrom":[subQ0,sQuery(id+"F0.wireOp",EDGE,"E21")]}),-1.0]])],"derivedFrom":subQ0})])],"isStart":true});}
            var Q323;
            Q323=makeQuery(id+"F1.opExtrude","SWEPT_EDGE",EDGE,{"disambiguationData":[OSD([sQuery(id+"F0.wireOp",EDGE,"E7.right"),sQuery(id+"F0.wireOp",EDGE,"E13.top")])]});
            var Q324;
            Q324=makeQuery(id+"F1.opExtrude","SWEPT_EDGE",EDGE,{"disambiguationData":[OSD([sQuery(id+"F0.wireOp",EDGE,"E11.top"),sQuery(id+"F0.wireOp",EDGE,"E11.right")])]});
            var Q325;
            Q325=makeQuery(id+"F1.opExtrude","SWEPT_EDGE",EDGE,{"disambiguationData":[OSD([sQuery(id+"F0.wireOp",EDGE,"E2.right"),sQuery(id+"F0.wireOp",EDGE,"E19")])]});
            var Q326;
            {var subQ0=sQuery(id+"F0.wireOp",EDGE,"E2.left");Q326=makeQuery(id+"F1.opExtrude","CAP_EDGE",EDGE,{"disambiguationData":[OSD([subQ0]),TDD([makeQuery(id+"F0.imprint","IMPRINT",EDGE,{"disambiguationData":[TD([[makeQuery(id+"F0.imprint","INTERSECT",VERTEX,{"derivedFrom":[subQ0,sQuery(id+"F0.wireOp",EDGE,"E13.top")]}),-1.0]])],"derivedFrom":subQ0})])],"isStart":true});}
            var Q327;
            {var subQ0=sQuery(id+"F0.wireOp",EDGE,"E14.top");Q327=makeQuery(id+"F1.opExtrude","CAP_EDGE",EDGE,{"disambiguationData":[OSD([subQ0]),TDD([makeQuery(id+"F0.imprint","IMPRINT",EDGE,{"disambiguationData":[TD([[makeQuery(id+"F0.imprint","INTERSECT",VERTEX,{"derivedFrom":[sQuery(id+"F0.wireOp",EDGE,"E10.left"),subQ0]}),-1.0]])],"derivedFrom":subQ0})])],"isStart":true});}
            var Q328;
            Q328=makeQuery(id+"F1.opExtrude","SWEPT_EDGE",EDGE,{"disambiguationData":[OSD([sQuery(id+"F0.wireOp",EDGE,"E1.left"),sQuery(id+"F0.wireOp",EDGE,"E29")])]});
            var Q329;
            Q329=makeQuery(id+"F1.opExtrude","SWEPT_EDGE",EDGE,{"disambiguationData":[OSD([sQuery(id+"F0.wireOp",EDGE,"E16"),sQuery(id+"F0.wireOp",EDGE,"E17")])]});
            var Q330;
            {var subQ0=sQuery(id+"F0.wireOp",EDGE,"E14.top");Q330=makeQuery(id+"F1.opExtrude","CAP_EDGE",EDGE,{"disambiguationData":[OSD([subQ0]),TDD([makeQuery(id+"F0.imprint","IMPRINT",EDGE,{"disambiguationData":[TD([[makeQuery(id+"F0.imprint","INTERSECT",VERTEX,{"derivedFrom":[sQuery(id+"F0.wireOp",EDGE,"E8.left"),subQ0]}),-1.0]])],"derivedFrom":subQ0})])],"isStart":true});}
            var Q331;
            Q331=makeQuery(id+"F1.opExtrude","SWEPT_EDGE",EDGE,{"disambiguationData":[OSD([sQuery(id+"F0.wireOp",EDGE,"E1.right"),sQuery(id+"F0.wireOp",EDGE,"E32")])]});
            var Q332;
            Q332=makeQuery(id+"F1.opExtrude","SWEPT_EDGE",EDGE,{"disambiguationData":[OSD([sQuery(id+"F0.wireOp",EDGE,"E14.top"),sQuery(id+"F0.wireOp",EDGE,"E24")])]});
            var Q333;
            {var subQ0=sQuery(id+"F0.wireOp",EDGE,"E10.right");Q333=makeQuery(id+"F1.opExtrude","CAP_EDGE",EDGE,{"disambiguationData":[OSD([subQ0]),TDD([makeQuery(id+"F0.imprint","IMPRINT",EDGE,{"disambiguationData":[TD([[makeQuery(id+"F0.imprint","INTERSECT",VERTEX,{"derivedFrom":[subQ0,sQuery(id+"F0.wireOp",EDGE,"E14.bottom")]}),-1.0]])],"derivedFrom":subQ0})])],"isStart":true});}
            var Q334;
            {var subQ0=sQuery(id+"F0.wireOp",EDGE,"E16");Q334=makeQuery(id+"F1.opExtrude","CAP_EDGE",EDGE,{"disambiguationData":[OSD([subQ0]),TDD([makeQuery(id+"F0.imprint","IMPRINT",EDGE,{"disambiguationData":[TD([[makeQuery(id+"F0.imprint","INTERSECT",VERTEX,{"derivedFrom":[subQ0,sQuery(id+"F0.wireOp",EDGE,"E17")]}),-1.0]])],"derivedFrom":subQ0})])],"isStart":true});}
            var Q335;
            Q335=makeQuery(id+"F1.opExtrude","SWEPT_EDGE",EDGE,{"disambiguationData":[OSD([sQuery(id+"F0.wireOp",EDGE,"E11.top"),sQuery(id+"F0.wireOp",EDGE,"E11.left")])]});
            var Q336;
            {var subQ0=sQuery(id+"F0.wireOp",EDGE,"E11.right");Q336=makeQuery(id+"F1.opExtrude","CAP_EDGE",EDGE,{"disambiguationData":[OSD([subQ0]),TDD([makeQuery(id+"F0.imprint","IMPRINT",EDGE,{"disambiguationData":[TD([[makeQuery(id+"F0.imprint","INTERSECT",VERTEX,{"derivedFrom":[sQuery(id+"F0.wireOp",EDGE,"E11.top"),subQ0]}),1.0]])],"derivedFrom":subQ0})])],"isStart":true});}
            var Q337;
            {var subQ0=sQuery(id+"F0.wireOp",EDGE,"E13.bottom");Q337=makeQuery(id+"F1.opExtrude","CAP_EDGE",EDGE,{"disambiguationData":[OSD([subQ0]),TDD([makeQuery(id+"F0.imprint","IMPRINT",EDGE,{"disambiguationData":[TD([[makeQuery(id+"F0.imprint","INTERSECT",VERTEX,{"derivedFrom":[sQuery(id+"F0.wireOp",EDGE,"E1.left"),subQ0]}),-1.0]])],"derivedFrom":subQ0})])],"isStart":false});}
            var Q338;
            {var subQ0=sQuery(id+"F0.wireOp",EDGE,"E13.top");Q338=makeQuery(id+"F1.opExtrude","CAP_EDGE",EDGE,{"disambiguationData":[OSD([subQ0]),TDD([makeQuery(id+"F0.imprint","IMPRINT",EDGE,{"disambiguationData":[TD([[makeQuery(id+"F0.imprint","INTERSECT",VERTEX,{"derivedFrom":[sQuery(id+"F0.wireOp",EDGE,"E6.left"),subQ0]}),-1.0]])],"derivedFrom":subQ0})])],"isStart":true});}
            var Q339;
            {var subQ0=sQuery(id+"F0.wireOp",EDGE,"E13.top");Q339=makeQuery(id+"F1.opExtrude","CAP_EDGE",EDGE,{"disambiguationData":[OSD([subQ0]),TDD([makeQuery(id+"F0.imprint","IMPRINT",EDGE,{"disambiguationData":[TD([[makeQuery(id+"F0.imprint","INTERSECT",VERTEX,{"derivedFrom":[sQuery(id+"F0.wireOp",EDGE,"E8.left"),subQ0]}),-1.0]])],"derivedFrom":subQ0})])],"isStart":true});}
            var Q340;
            {var subQ0=sQuery(id+"F0.wireOp",EDGE,"E16");Q340=makeQuery(id+"F1.opExtrude","CAP_EDGE",EDGE,{"disambiguationData":[OSD([subQ0]),TDD([makeQuery(id+"F0.imprint","IMPRINT",EDGE,{"disambiguationData":[TD([[makeQuery(id+"F0.imprint","INTERSECT",VERTEX,{"derivedFrom":[subQ0,sQuery(id+"F0.wireOp",EDGE,"E27")]}),1.0]])],"derivedFrom":subQ0})])],"isStart":true});}
            var Q341;
            {var subQ0=sQuery(id+"F0.wireOp",EDGE,"E14.bottom");Q341=makeQuery(id+"F1.opExtrude","CAP_EDGE",EDGE,{"disambiguationData":[OSD([subQ0]),TDD([makeQuery(id+"F0.imprint","IMPRINT",EDGE,{"disambiguationData":[TD([[makeQuery(id+"F0.imprint","INTERSECT",VERTEX,{"derivedFrom":[sQuery(id+"F0.wireOp",EDGE,"E1.right"),subQ0]}),1.0]])],"derivedFrom":subQ0})])],"isStart":true});}
            var Q342;
            {var subQ0=sQuery(id+"F0.wireOp",EDGE,"E14.bottom");Q342=makeQuery(id+"F1.opExtrude","CAP_EDGE",EDGE,{"disambiguationData":[OSD([subQ0]),TDD([makeQuery(id+"F0.imprint","IMPRINT",EDGE,{"disambiguationData":[TD([[makeQuery(id+"F0.imprint","INTERSECT",VERTEX,{"derivedFrom":[sQuery(id+"F0.wireOp",EDGE,"E6.left"),subQ0]}),-1.0]])],"derivedFrom":subQ0})])],"isStart":true});}
            var Q343;
            Q343=makeQuery(id+"F1.opExtrude","SWEPT_EDGE",EDGE,{"disambiguationData":[OSD([sQuery(id+"F0.wireOp",EDGE,"E1.right"),sQuery(id+"F0.wireOp",EDGE,"E22")])]});
            var Q344;
            Q344=makeQuery(id+"F1.opExtrude","SWEPT_EDGE",EDGE,{"disambiguationData":[OSD([sQuery(id+"F0.wireOp",EDGE,"E13.top"),sQuery(id+"F0.wireOp",EDGE,"E16")])]});
            var Q345;
            Q345=makeQuery(id+"F1.opExtrude","SWEPT_EDGE",EDGE,{"disambiguationData":[OSD([sQuery(id+"F0.wireOp",EDGE,"E2.left"),sQuery(id+"F0.wireOp",EDGE,"E13.bottom")])]});
            var Q346;
            Q346=makeQuery(id+"F1.opExtrude","CAP_EDGE",EDGE,{"disambiguationData":[OSD([sQuery(id+"F0.wireOp",EDGE,"E27")])],"isStart":true});
            var Q347;
            Q347=makeQuery(id+"F1.opExtrude","SWEPT_EDGE",EDGE,{"disambiguationData":[OSD([sQuery(id+"F0.wireOp",EDGE,"E1.left"),sQuery(id+"F0.wireOp",EDGE,"E14.top")])]});
            var Q348;
            Q348=makeQuery(id+"F1.opExtrude","SWEPT_EDGE",EDGE,{"disambiguationData":[OSD([sQuery(id+"F0.wireOp",EDGE,"E2.left"),sQuery(id+"F0.wireOp",EDGE,"E14.top")])]});
            var Q349;
            Q349=makeQuery(id+"F1.opExtrude","SWEPT_EDGE",EDGE,{"disambiguationData":[OSD([sQuery(id+"F0.wireOp",EDGE,"E1.right"),sQuery(id+"F0.wireOp",EDGE,"E14.bottom")])]});
            var Q350;
            {var subQ0=sQuery(id+"F0.wireOp",EDGE,"E1.right");Q350=makeQuery(id+"F1.opExtrude","CAP_EDGE",EDGE,{"disambiguationData":[OSD([subQ0]),TDD([makeQuery(id+"F0.imprint","IMPRINT",EDGE,{"disambiguationData":[TD([[makeQuery(id+"F0.imprint","INTERSECT",VERTEX,{"derivedFrom":[subQ0,sQuery(id+"F0.wireOp",EDGE,"E22")]}),-1.0]])],"derivedFrom":subQ0})])],"isStart":true});}
            var Q351;
            {var subQ0=sQuery(id+"F0.wireOp",EDGE,"E14.top");Q351=makeQuery(id+"F1.opExtrude","CAP_EDGE",EDGE,{"disambiguationData":[OSD([subQ0]),TDD([makeQuery(id+"F0.imprint","IMPRINT",EDGE,{"disambiguationData":[TD([[makeQuery(id+"F0.imprint","INTERSECT",VERTEX,{"derivedFrom":[sQuery(id+"F0.wireOp",EDGE,"E7.right"),subQ0]}),-1.0]])],"derivedFrom":subQ0})])],"isStart":true});}
            var Q352;
            Q352=makeQuery(id+"F1.opExtrude","SWEPT_EDGE",EDGE,{"disambiguationData":[OSD([sQuery(id+"F0.wireOp",EDGE,"E1.left"),sQuery(id+"F0.wireOp",EDGE,"E13.bottom")])]});
            var Q353;
            {var subQ0=sQuery(id+"F0.wireOp",EDGE,"E16");Q353=makeQuery(id+"F1.opExtrude","CAP_EDGE",EDGE,{"disambiguationData":[OSD([subQ0]),TDD([makeQuery(id+"F0.imprint","IMPRINT",EDGE,{"disambiguationData":[TD([[makeQuery(id+"F0.imprint","INTERSECT",VERTEX,{"derivedFrom":[sQuery(id+"F0.wireOp",EDGE,"E14.bottom"),subQ0]}),-1.0]])],"derivedFrom":subQ0})])],"isStart":true});}
            var Q354;
            Q354=makeQuery(id+"F1.opExtrude","SWEPT_EDGE",EDGE,{"disambiguationData":[OSD([sQuery(id+"F0.wireOp",EDGE,"E14.top"),sQuery(id+"F0.wireOp",EDGE,"E23")])]});
            var Q355;
            {var subQ0=sQuery(id+"F0.wireOp",EDGE,"E14.top");Q355=makeQuery(id+"F1.opExtrude","CAP_EDGE",EDGE,{"disambiguationData":[OSD([subQ0]),TDD([makeQuery(id+"F0.imprint","IMPRINT",EDGE,{"disambiguationData":[TD([[makeQuery(id+"F0.imprint","INTERSECT",VERTEX,{"derivedFrom":[sQuery(id+"F0.wireOp",EDGE,"E9.right"),subQ0]}),-1.0]])],"derivedFrom":subQ0})])],"isStart":true});}
            var Q356;
            Q356=makeQuery(id+"F1.opExtrude","SWEPT_EDGE",EDGE,{"disambiguationData":[OSD([sQuery(id+"F0.wireOp",EDGE,"E6.left"),sQuery(id+"F0.wireOp",EDGE,"E13.top")])]});
            var Q357;
            {var subQ0=sQuery(id+"F0.wireOp",EDGE,"E13.bottom");Q357=makeQuery(id+"F1.opExtrude","CAP_EDGE",EDGE,{"disambiguationData":[OSD([subQ0]),TDD([makeQuery(id+"F0.imprint","IMPRINT",EDGE,{"disambiguationData":[TD([[makeQuery(id+"F0.imprint","INTERSECT",VERTEX,{"derivedFrom":[sQuery(id+"F0.wireOp",EDGE,"E8.left"),subQ0]}),-1.0]])],"derivedFrom":subQ0})])],"isStart":true});}
            var Q358;
            Q358=makeQuery(id+"F1.opExtrude","SWEPT_EDGE",EDGE,{"disambiguationData":[OSD([sQuery(id+"F0.wireOp",EDGE,"E13.bottom"),sQuery(id+"F0.wireOp",EDGE,"E16")])]});
            var Q359;
            {var subQ0=sQuery(id+"F0.wireOp",EDGE,"E13.bottom");Q359=makeQuery(id+"F1.opExtrude","CAP_EDGE",EDGE,{"disambiguationData":[OSD([subQ0]),TDD([makeQuery(id+"F0.imprint","IMPRINT",EDGE,{"disambiguationData":[TD([[makeQuery(id+"F0.imprint","INTERSECT",VERTEX,{"derivedFrom":[sQuery(id+"F0.wireOp",EDGE,"E1.left"),subQ0]}),-1.0]])],"derivedFrom":subQ0})])],"isStart":true});}
            var Q360;
            Q360=makeQuery(id+"F1.opExtrude","SWEPT_EDGE",EDGE,{"disambiguationData":[OSD([sQuery(id+"F0.wireOp",EDGE,"E9.right"),sQuery(id+"F0.wireOp",EDGE,"E14.top")])]});
            var Q361;
            Q361=makeQuery(id+"F1.opExtrude","CAP_EDGE",EDGE,{"disambiguationData":[OSD([sQuery(id+"F0.wireOp",EDGE,"E21")])],"isStart":true});
            var Q362;
            {var subQ0=sQuery(id+"F0.wireOp",EDGE,"E14.top");Q362=makeQuery(id+"F1.opExtrude","CAP_EDGE",EDGE,{"disambiguationData":[OSD([subQ0]),TDD([makeQuery(id+"F0.imprint","IMPRINT",EDGE,{"disambiguationData":[TD([[makeQuery(id+"F0.imprint","INTERSECT",VERTEX,{"derivedFrom":[sQuery(id+"F0.wireOp",EDGE,"E1.left"),subQ0]}),-1.0]])],"derivedFrom":subQ0})])],"isStart":true});}
            var Q363;
            Q363=makeQuery(id+"F1.opExtrude","SWEPT_EDGE",EDGE,{"disambiguationData":[OSD([sQuery(id+"F0.wireOp",EDGE,"E16"),sQuery(id+"F0.wireOp",EDGE,"E27")])]});
            chamfer(context, id + "F2", {"entities" : qUnion([Q0, Q1, Q2, Q3, Q4, Q5, Q6, Q7, Q8, Q9, Q10, Q11, Q12, Q13, Q14, Q15, Q16, Q17, Q18, Q19, Q20, Q21, Q22, Q23, Q24, Q25, Q26, Q27, Q28, Q29, Q30, Q31, Q32, Q33, Q34, Q35, Q36, Q37, Q38, Q39, Q40, Q41, Q42, Q43, Q44, Q45, Q46, Q47, Q48, Q49, Q50, Q51, Q52, Q53, Q54, Q55, Q56, Q57, Q58, Q59, Q60, Q61, Q62, Q63, Q64, Q65, Q66, Q67, Q68, Q69, Q70, Q71, Q72, Q73, Q74, Q75, Q76, Q77, Q78, Q79, Q80, Q81, Q82, Q83, Q84, Q85, Q86, Q87, Q88, Q89, Q90, Q91, Q92, Q93, Q94, Q95, Q96, Q97, Q98, Q99, Q100, Q101, Q102, Q103, Q104, Q105, Q106, Q107, Q108, Q109, Q110, Q111, Q112, Q113, Q114, Q115, Q116, Q117, Q118, Q119, Q120, Q121, Q122, Q123, Q124, Q125, Q126, Q127, Q128, Q129, Q130, Q131, Q132, Q133, Q134, Q135, Q136, Q137, Q138, Q139, Q140, Q141, Q142, Q143, Q144, Q145, Q146, Q147, Q148, Q149, Q150, Q151, Q152, Q153, Q154, Q155, Q156, Q157, Q158, Q159, Q160, Q161, Q162, Q163, Q164, Q165, Q166, Q167, Q168, Q169, Q170, Q171, Q172, Q173, Q174, Q175, Q176, Q177, Q178, Q179, Q180, Q181, Q182, Q183, Q184, Q185, Q186, Q187, Q188, Q189, Q190, Q191, Q192, Q193, Q194, Q195, Q196, Q197, Q198, Q199, Q200, Q201, Q202, Q203, Q204, Q205, Q206, Q207, Q208, Q209, Q210, Q211, Q212, Q213, Q214, Q215, Q216, Q217, Q218, Q219, Q220, Q221, Q222, Q223, Q224, Q225, Q226, Q227, Q228, Q229, Q230, Q231, Q232, Q233, Q234, Q235, Q236, Q237, Q238, Q239, Q240, Q241, Q242, Q243, Q244, Q245, Q246, Q247, Q248, Q249, Q250, Q251, Q252, Q253, Q254, Q255, Q256, Q257, Q258, Q259, Q260, Q261, Q262, Q263, Q264, Q265, Q266, Q267, Q268, Q269, Q270, Q271, Q272, Q273, Q274, Q275, Q276, Q277, Q278, Q279, Q280, Q281, Q282, Q283, Q284, Q285, Q286, Q287, Q288, Q289, Q290, Q291, Q292, Q293, Q294, Q295, Q296, Q297, Q298, Q299, Q300, Q301, Q302, Q303, Q304, Q305, Q306, Q307, Q308, Q309, Q310, Q311, Q312, Q313, Q314, Q315, Q316, Q317, Q318, Q319, Q320, Q321, Q322, Q323, Q324, Q325, Q326, Q327, Q328, Q329, Q330, Q331, Q332, Q333, Q334, Q335, Q336, Q337, Q338, Q339, Q340, Q341, Q342, Q343, Q344, Q345, Q346, Q347, Q348, Q349, Q350, Q351, Q352, Q353, Q354, Q355, Q356, Q357, Q358, Q359, Q360, Q361, Q362, Q363]), "width" : 1 * mm, "tangentPropagation" : true});
        }
        {
            var Q0;
            Q0=qCreatedBy(makeId("Right.planeOp"),FACE);
            var sketch = newSketch(context, id + "F3", { "sketchPlane" : qUnion([Q0])});
            skLineSegment(sketch, "E33.bottom", {"start": v(0, 42) * mm, "end": v(-7, 42) * mm});
            skLineSegment(sketch, "E33.top", {"start": v(0, 38) * mm, "end": v(-7, 38) * mm});
            skLineSegment(sketch, "E33.left", {"start": v(0, 42) * mm, "end": v(0, 38) * mm});
            skLineSegment(sketch, "E33.right", {"start": v(-7, 42) * mm, "end": v(-7, 38) * mm});
            skSolve(sketch);
        }
        {
            var Q0;
            Q0=makeQuery(id+"F3.imprint","IMPRINT",FACE,{"disambiguationData":[TD([[makeQuery(id+"F3.imprint","IMPRINT",EDGE,{"derivedFrom":sQuery(id+"F3.wireOp",EDGE,"E33.bottom")}),1.0]])]});
            extrude(context, id + "F4", {"entities" : qUnion([Q0]), "operationType" : NewBodyOperationType.ADD, "depth" : 110 * mm, "offsetDistance" : 25 * mm});
        }
        {
            var Q0;
            Q0=makeQuery(id+"F4.opExtrude","SWEPT_EDGE",EDGE,{"disambiguationData":[OSD([sQuery(id+"F3.wireOp",EDGE,"E33.top"),sQuery(id+"F3.wireOp",EDGE,"E33.right")])]});
            var Q1;
            Q1=makeQuery(id+"F4.opExtrude","SWEPT_EDGE",EDGE,{"disambiguationData":[OSD([sQuery(id+"F3.wireOp",EDGE,"E33.bottom"),sQuery(id+"F3.wireOp",EDGE,"E33.right")])]});
            var Q2;
            Q2=makeQuery(id+"F4.opExtrude","CAP_EDGE",EDGE,{"disambiguationData":[OSD([sQuery(id+"F3.wireOp",EDGE,"E33.right")])],"isStart":true});
            var Q3;
            Q3=makeQuery(id+"F4.opExtrude","CAP_EDGE",EDGE,{"disambiguationData":[OSD([sQuery(id+"F3.wireOp",EDGE,"E33.right")])],"isStart":false});
            fillet(context, id + "F5", {"entities" : qUnion([Q0, Q1, Q2, Q3]), "radius" : 2 * mm, "tangentPropagation" : true, "allowEdgeOverflow" : false});
        }
    });
